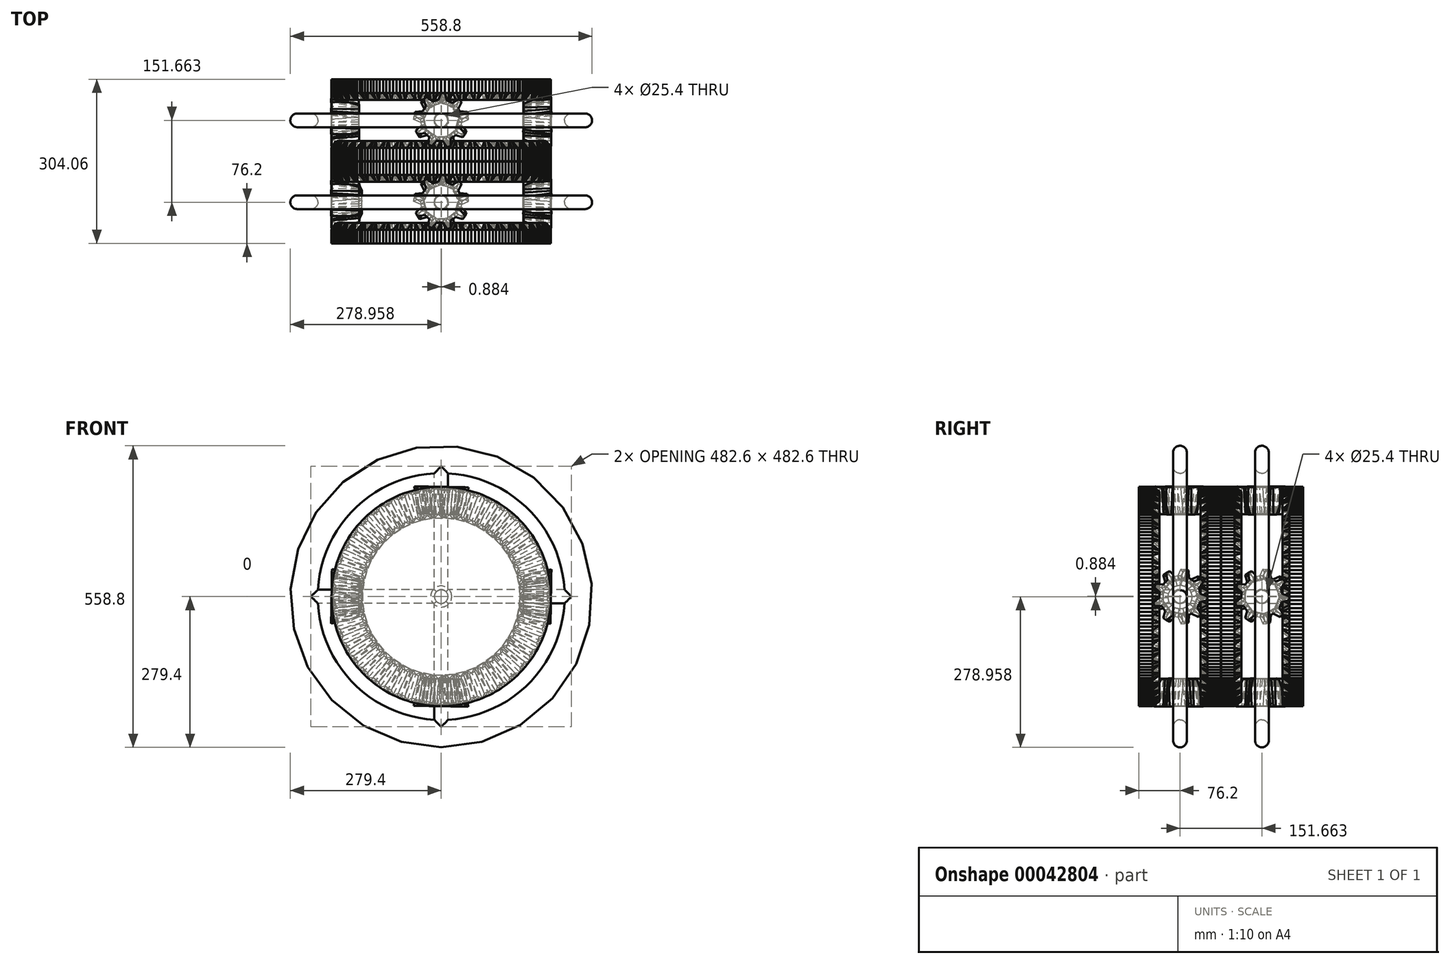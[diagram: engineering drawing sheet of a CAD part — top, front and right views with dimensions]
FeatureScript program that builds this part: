
annotation { "Feature Type Name" : "Feature", "Feature Type Description" : "" }
export const myFeature = defineFeature(function(context is Context, id is Id, definition is map)
    precondition{}
    {
        {
            var Q0;
            Q0=qCreatedBy(makeId("Front.planeOp"),FACE);
            var sketch = newSketch(context, id + "F0", { "sketchPlane" : qUnion([Q0])});
            skLineSegment(sketch, "E0", {"start": v(0, 0) * mm, "end": v(-203.2, 0) * mm, "construction": true});
            skLineSegment(sketch, "E1", {"start": v(-203.2, 0) * mm, "end": v(-152.4, 0) * mm});
            skLineSegment(sketch, "E2.1.0", {"start": v(-203.08, -7.1) * mm, "end": v(-152.3, -5.32) * mm});
            skLineSegment(sketch, "E2.2.0", {"start": v(-202.7, -14.17) * mm, "end": v(-152.03, -10.63) * mm});
            skLineSegment(sketch, "E2.3.0", {"start": v(-202.09, -21.24) * mm, "end": v(-151.57, -15.93) * mm});
            skLineSegment(sketch, "E2.4.0", {"start": v(-201.22, -28.28) * mm, "end": v(-150.92, -21.2) * mm});
            skLineSegment(sketch, "E2.5.0", {"start": v(-200.11, -35.29) * mm, "end": v(-150.08, -26.46) * mm});
            skLineSegment(sketch, "E2.6.0", {"start": v(-198.76, -42.25) * mm, "end": v(-149.07, -31.69) * mm});
            skLineSegment(sketch, "E2.7.0", {"start": v(-197.16, -49.16) * mm, "end": v(-147.87, -36.87) * mm});
            skLineSegment(sketch, "E2.8.0", {"start": v(-195.33, -56) * mm, "end": v(-146.5, -42) * mm});
            skLineSegment(sketch, "E2.9.0", {"start": v(-193.25, -62.8) * mm, "end": v(-144.94, -47.1) * mm});
            skLineSegment(sketch, "E2.10.0", {"start": v(-190.95, -69.5) * mm, "end": v(-143.2, -52.12) * mm});
            skLineSegment(sketch, "E2.11.0", {"start": v(-188.4, -76.12) * mm, "end": v(-141.3, -57.1) * mm});
            skLineSegment(sketch, "E2.12.0", {"start": v(-185.63, -82.65) * mm, "end": v(-139.22, -61.99) * mm});
            skLineSegment(sketch, "E2.13.0", {"start": v(-182.63, -89.08) * mm, "end": v(-136.98, -66.8) * mm});
            skLineSegment(sketch, "E2.14.0", {"start": v(-179.41, -95.4) * mm, "end": v(-134.56, -71.55) * mm});
            skLineSegment(sketch, "E2.15.0", {"start": v(-175.98, -101.6) * mm, "end": v(-131.98, -76.2) * mm});
            skLineSegment(sketch, "E2.16.0", {"start": v(-172.32, -107.68) * mm, "end": v(-129.24, -80.76) * mm});
            skLineSegment(sketch, "E2.17.0", {"start": v(-168.46, -113.63) * mm, "end": v(-126.35, -85.22) * mm});
            skLineSegment(sketch, "E2.18.0", {"start": v(-164.4, -119.44) * mm, "end": v(-123.3, -89.58) * mm});
            skLineSegment(sketch, "E2.19.0", {"start": v(-160.12, -125.1) * mm, "end": v(-120.1, -93.83) * mm});
            skLineSegment(sketch, "E2.20.0", {"start": v(-155.66, -130.61) * mm, "end": v(-116.75, -97.96) * mm});
            skLineSegment(sketch, "E2.21.0", {"start": v(-151, -135.97) * mm, "end": v(-113.26, -101.98) * mm});
            skLineSegment(sketch, "E2.22.0", {"start": v(-146.17, -141.15) * mm, "end": v(-109.63, -105.87) * mm});
            skLineSegment(sketch, "E2.23.0", {"start": v(-141.15, -146.17) * mm, "end": v(-105.87, -109.63) * mm});
            skLineSegment(sketch, "E2.24.0", {"start": v(-135.97, -151) * mm, "end": v(-101.98, -113.26) * mm});
            skLineSegment(sketch, "E2.25.0", {"start": v(-130.61, -155.66) * mm, "end": v(-97.96, -116.75) * mm});
            skLineSegment(sketch, "E2.26.0", {"start": v(-125.1, -160.12) * mm, "end": v(-93.83, -120.1) * mm});
            skLineSegment(sketch, "E2.27.0", {"start": v(-119.44, -164.4) * mm, "end": v(-89.58, -123.3) * mm});
            skLineSegment(sketch, "E2.28.0", {"start": v(-113.63, -168.46) * mm, "end": v(-85.22, -126.35) * mm});
            skLineSegment(sketch, "E2.29.0", {"start": v(-107.68, -172.32) * mm, "end": v(-80.76, -129.24) * mm});
            skLineSegment(sketch, "E2.30.0", {"start": v(-101.6, -175.98) * mm, "end": v(-76.2, -131.98) * mm});
            skLineSegment(sketch, "E2.31.0", {"start": v(-95.4, -179.41) * mm, "end": v(-71.55, -134.56) * mm});
            skLineSegment(sketch, "E2.32.0", {"start": v(-89.08, -182.63) * mm, "end": v(-66.8, -136.98) * mm});
            skLineSegment(sketch, "E2.33.0", {"start": v(-82.65, -185.63) * mm, "end": v(-61.99, -139.22) * mm});
            skLineSegment(sketch, "E2.34.0", {"start": v(-76.12, -188.4) * mm, "end": v(-57.1, -141.3) * mm});
            skLineSegment(sketch, "E2.35.0", {"start": v(-69.5, -190.95) * mm, "end": v(-52.12, -143.2) * mm});
            skLineSegment(sketch, "E2.36.0", {"start": v(-62.8, -193.25) * mm, "end": v(-47.1, -144.94) * mm});
            skLineSegment(sketch, "E2.37.0", {"start": v(-56, -195.33) * mm, "end": v(-42, -146.5) * mm});
            skLineSegment(sketch, "E2.38.0", {"start": v(-49.16, -197.16) * mm, "end": v(-36.87, -147.87) * mm});
            skLineSegment(sketch, "E2.39.0", {"start": v(-42.25, -198.76) * mm, "end": v(-31.69, -149.07) * mm});
            skLineSegment(sketch, "E2.40.0", {"start": v(-35.29, -200.11) * mm, "end": v(-26.46, -150.08) * mm});
            skLineSegment(sketch, "E2.41.0", {"start": v(-28.28, -201.22) * mm, "end": v(-21.2, -150.92) * mm});
            skLineSegment(sketch, "E2.42.0", {"start": v(-21.24, -202.09) * mm, "end": v(-15.93, -151.57) * mm});
            skLineSegment(sketch, "E2.43.0", {"start": v(-14.17, -202.7) * mm, "end": v(-10.63, -152.03) * mm});
            skLineSegment(sketch, "E2.44.0", {"start": v(-7.1, -203.08) * mm, "end": v(-5.32, -152.3) * mm});
            skLineSegment(sketch, "E2.45.0", {"start": v(0, -203.2) * mm, "end": v(0, -152.4) * mm});
            skLineSegment(sketch, "E2.46.0", {"start": v(7.1, -203.08) * mm, "end": v(5.32, -152.3) * mm});
            skLineSegment(sketch, "E2.47.0", {"start": v(14.17, -202.7) * mm, "end": v(10.63, -152.03) * mm});
            skLineSegment(sketch, "E2.48.0", {"start": v(21.24, -202.09) * mm, "end": v(15.93, -151.57) * mm});
            skLineSegment(sketch, "E2.49.0", {"start": v(28.28, -201.22) * mm, "end": v(21.2, -150.92) * mm});
            skLineSegment(sketch, "E2.50.0", {"start": v(35.29, -200.11) * mm, "end": v(26.46, -150.08) * mm});
            skLineSegment(sketch, "E2.51.0", {"start": v(42.25, -198.76) * mm, "end": v(31.69, -149.07) * mm});
            skLineSegment(sketch, "E2.52.0", {"start": v(49.16, -197.16) * mm, "end": v(36.87, -147.87) * mm});
            skLineSegment(sketch, "E2.53.0", {"start": v(56, -195.33) * mm, "end": v(42, -146.5) * mm});
            skLineSegment(sketch, "E2.54.0", {"start": v(62.8, -193.25) * mm, "end": v(47.1, -144.94) * mm});
            skLineSegment(sketch, "E2.55.0", {"start": v(69.5, -190.95) * mm, "end": v(52.12, -143.2) * mm});
            skLineSegment(sketch, "E2.56.0", {"start": v(76.12, -188.4) * mm, "end": v(57.1, -141.3) * mm});
            skLineSegment(sketch, "E2.57.0", {"start": v(82.65, -185.63) * mm, "end": v(61.99, -139.22) * mm});
            skLineSegment(sketch, "E2.58.0", {"start": v(89.08, -182.63) * mm, "end": v(66.8, -136.98) * mm});
            skLineSegment(sketch, "E2.59.0", {"start": v(95.4, -179.41) * mm, "end": v(71.55, -134.56) * mm});
            skLineSegment(sketch, "E2.60.0", {"start": v(101.6, -175.98) * mm, "end": v(76.2, -131.98) * mm});
            skLineSegment(sketch, "E2.61.0", {"start": v(107.68, -172.32) * mm, "end": v(80.76, -129.24) * mm});
            skLineSegment(sketch, "E2.62.0", {"start": v(113.63, -168.46) * mm, "end": v(85.22, -126.35) * mm});
            skLineSegment(sketch, "E2.63.0", {"start": v(119.44, -164.4) * mm, "end": v(89.58, -123.3) * mm});
            skLineSegment(sketch, "E2.64.0", {"start": v(125.1, -160.12) * mm, "end": v(93.83, -120.1) * mm});
            skLineSegment(sketch, "E2.65.0", {"start": v(130.61, -155.66) * mm, "end": v(97.96, -116.75) * mm});
            skLineSegment(sketch, "E2.66.0", {"start": v(135.97, -151) * mm, "end": v(101.98, -113.26) * mm});
            skLineSegment(sketch, "E2.67.0", {"start": v(141.15, -146.17) * mm, "end": v(105.87, -109.63) * mm});
            skLineSegment(sketch, "E2.68.0", {"start": v(146.17, -141.15) * mm, "end": v(109.63, -105.87) * mm});
            skLineSegment(sketch, "E2.69.0", {"start": v(151, -135.97) * mm, "end": v(113.26, -101.98) * mm});
            skLineSegment(sketch, "E2.70.0", {"start": v(155.66, -130.61) * mm, "end": v(116.75, -97.96) * mm});
            skLineSegment(sketch, "E2.71.0", {"start": v(160.12, -125.1) * mm, "end": v(120.1, -93.83) * mm});
            skLineSegment(sketch, "E2.72.0", {"start": v(164.4, -119.44) * mm, "end": v(123.3, -89.58) * mm});
            skLineSegment(sketch, "E2.73.0", {"start": v(168.46, -113.63) * mm, "end": v(126.35, -85.22) * mm});
            skLineSegment(sketch, "E2.74.0", {"start": v(172.32, -107.68) * mm, "end": v(129.24, -80.76) * mm});
            skLineSegment(sketch, "E2.75.0", {"start": v(175.98, -101.6) * mm, "end": v(131.98, -76.2) * mm});
            skLineSegment(sketch, "E2.76.0", {"start": v(179.41, -95.4) * mm, "end": v(134.56, -71.55) * mm});
            skLineSegment(sketch, "E2.77.0", {"start": v(182.63, -89.08) * mm, "end": v(136.98, -66.8) * mm});
            skLineSegment(sketch, "E2.78.0", {"start": v(185.63, -82.65) * mm, "end": v(139.22, -61.99) * mm});
            skLineSegment(sketch, "E2.79.0", {"start": v(188.4, -76.12) * mm, "end": v(141.3, -57.1) * mm});
            skLineSegment(sketch, "E2.80.0", {"start": v(190.95, -69.5) * mm, "end": v(143.2, -52.12) * mm});
            skLineSegment(sketch, "E2.81.0", {"start": v(193.25, -62.8) * mm, "end": v(144.94, -47.1) * mm});
            skLineSegment(sketch, "E2.82.0", {"start": v(195.33, -56) * mm, "end": v(146.5, -42) * mm});
            skLineSegment(sketch, "E2.83.0", {"start": v(197.16, -49.16) * mm, "end": v(147.87, -36.87) * mm});
            skLineSegment(sketch, "E2.84.0", {"start": v(198.76, -42.25) * mm, "end": v(149.07, -31.69) * mm});
            skLineSegment(sketch, "E2.85.0", {"start": v(200.11, -35.29) * mm, "end": v(150.08, -26.46) * mm});
            skLineSegment(sketch, "E2.86.0", {"start": v(201.22, -28.28) * mm, "end": v(150.92, -21.2) * mm});
            skLineSegment(sketch, "E2.87.0", {"start": v(202.09, -21.24) * mm, "end": v(151.57, -15.93) * mm});
            skLineSegment(sketch, "E2.88.0", {"start": v(202.7, -14.17) * mm, "end": v(152.03, -10.63) * mm});
            skLineSegment(sketch, "E2.89.0", {"start": v(203.08, -7.1) * mm, "end": v(152.3, -5.32) * mm});
            skLineSegment(sketch, "E2.90.0", {"start": v(203.2, 0) * mm, "end": v(152.4, 0) * mm});
            skLineSegment(sketch, "E2.91.0", {"start": v(203.08, 7.1) * mm, "end": v(152.3, 5.32) * mm});
            skLineSegment(sketch, "E2.92.0", {"start": v(202.7, 14.17) * mm, "end": v(152.03, 10.63) * mm});
            skLineSegment(sketch, "E2.93.0", {"start": v(202.09, 21.24) * mm, "end": v(151.57, 15.93) * mm});
            skLineSegment(sketch, "E2.94.0", {"start": v(201.22, 28.28) * mm, "end": v(150.92, 21.2) * mm});
            skLineSegment(sketch, "E2.95.0", {"start": v(200.11, 35.29) * mm, "end": v(150.08, 26.46) * mm});
            skLineSegment(sketch, "E2.96.0", {"start": v(198.76, 42.25) * mm, "end": v(149.07, 31.69) * mm});
            skLineSegment(sketch, "E2.97.0", {"start": v(197.16, 49.16) * mm, "end": v(147.87, 36.87) * mm});
            skLineSegment(sketch, "E2.98.0", {"start": v(195.33, 56) * mm, "end": v(146.5, 42) * mm});
            skLineSegment(sketch, "E2.99.0", {"start": v(193.25, 62.8) * mm, "end": v(144.94, 47.1) * mm});
            skLineSegment(sketch, "E2.100.0", {"start": v(190.95, 69.5) * mm, "end": v(143.2, 52.12) * mm});
            skLineSegment(sketch, "E2.101.0", {"start": v(188.4, 76.12) * mm, "end": v(141.3, 57.1) * mm});
            skLineSegment(sketch, "E2.102.0", {"start": v(185.63, 82.65) * mm, "end": v(139.22, 61.99) * mm});
            skLineSegment(sketch, "E2.103.0", {"start": v(182.63, 89.08) * mm, "end": v(136.98, 66.8) * mm});
            skLineSegment(sketch, "E2.104.0", {"start": v(179.41, 95.4) * mm, "end": v(134.56, 71.55) * mm});
            skLineSegment(sketch, "E2.105.0", {"start": v(175.98, 101.6) * mm, "end": v(131.98, 76.2) * mm});
            skLineSegment(sketch, "E2.106.0", {"start": v(172.32, 107.68) * mm, "end": v(129.24, 80.76) * mm});
            skLineSegment(sketch, "E2.107.0", {"start": v(168.46, 113.63) * mm, "end": v(126.35, 85.22) * mm});
            skLineSegment(sketch, "E2.108.0", {"start": v(164.4, 119.44) * mm, "end": v(123.3, 89.58) * mm});
            skLineSegment(sketch, "E2.109.0", {"start": v(160.12, 125.1) * mm, "end": v(120.1, 93.83) * mm});
            skLineSegment(sketch, "E2.110.0", {"start": v(155.66, 130.61) * mm, "end": v(116.75, 97.96) * mm});
            skLineSegment(sketch, "E2.111.0", {"start": v(151, 135.97) * mm, "end": v(113.26, 101.98) * mm});
            skLineSegment(sketch, "E2.112.0", {"start": v(146.17, 141.15) * mm, "end": v(109.63, 105.87) * mm});
            skLineSegment(sketch, "E2.113.0", {"start": v(141.15, 146.17) * mm, "end": v(105.87, 109.63) * mm});
            skLineSegment(sketch, "E2.114.0", {"start": v(135.97, 151) * mm, "end": v(101.98, 113.26) * mm});
            skLineSegment(sketch, "E2.115.0", {"start": v(130.61, 155.66) * mm, "end": v(97.96, 116.75) * mm});
            skLineSegment(sketch, "E2.116.0", {"start": v(125.1, 160.12) * mm, "end": v(93.83, 120.1) * mm});
            skLineSegment(sketch, "E2.117.0", {"start": v(119.44, 164.4) * mm, "end": v(89.58, 123.3) * mm});
            skLineSegment(sketch, "E2.118.0", {"start": v(113.63, 168.46) * mm, "end": v(85.22, 126.35) * mm});
            skLineSegment(sketch, "E2.119.0", {"start": v(107.68, 172.32) * mm, "end": v(80.76, 129.24) * mm});
            skLineSegment(sketch, "E2.120.0", {"start": v(101.6, 175.98) * mm, "end": v(76.2, 131.98) * mm});
            skLineSegment(sketch, "E2.121.0", {"start": v(95.4, 179.41) * mm, "end": v(71.55, 134.56) * mm});
            skLineSegment(sketch, "E2.122.0", {"start": v(89.08, 182.63) * mm, "end": v(66.8, 136.98) * mm});
            skLineSegment(sketch, "E2.123.0", {"start": v(82.65, 185.63) * mm, "end": v(61.99, 139.22) * mm});
            skLineSegment(sketch, "E2.124.0", {"start": v(76.12, 188.4) * mm, "end": v(57.1, 141.3) * mm});
            skLineSegment(sketch, "E2.125.0", {"start": v(69.5, 190.95) * mm, "end": v(52.12, 143.2) * mm});
            skLineSegment(sketch, "E2.126.0", {"start": v(62.8, 193.25) * mm, "end": v(47.1, 144.94) * mm});
            skLineSegment(sketch, "E2.127.0", {"start": v(56, 195.33) * mm, "end": v(42, 146.5) * mm});
            skLineSegment(sketch, "E2.128.0", {"start": v(49.16, 197.16) * mm, "end": v(36.87, 147.87) * mm});
            skLineSegment(sketch, "E2.129.0", {"start": v(42.25, 198.76) * mm, "end": v(31.69, 149.07) * mm});
            skLineSegment(sketch, "E2.130.0", {"start": v(35.29, 200.11) * mm, "end": v(26.46, 150.08) * mm});
            skLineSegment(sketch, "E2.131.0", {"start": v(28.28, 201.22) * mm, "end": v(21.2, 150.92) * mm});
            skLineSegment(sketch, "E2.132.0", {"start": v(21.24, 202.09) * mm, "end": v(15.93, 151.57) * mm});
            skLineSegment(sketch, "E2.133.0", {"start": v(14.17, 202.7) * mm, "end": v(10.63, 152.03) * mm});
            skLineSegment(sketch, "E2.134.0", {"start": v(7.1, 203.08) * mm, "end": v(5.32, 152.3) * mm});
            skLineSegment(sketch, "E2.135.0", {"start": v(0, 203.2) * mm, "end": v(0, 152.4) * mm});
            skLineSegment(sketch, "E2.136.0", {"start": v(-7.1, 203.08) * mm, "end": v(-5.32, 152.3) * mm});
            skLineSegment(sketch, "E2.137.0", {"start": v(-14.17, 202.7) * mm, "end": v(-10.63, 152.03) * mm});
            skLineSegment(sketch, "E2.138.0", {"start": v(-21.24, 202.09) * mm, "end": v(-15.93, 151.57) * mm});
            skLineSegment(sketch, "E2.139.0", {"start": v(-28.28, 201.22) * mm, "end": v(-21.2, 150.92) * mm});
            skLineSegment(sketch, "E2.140.0", {"start": v(-35.29, 200.11) * mm, "end": v(-26.46, 150.08) * mm});
            skLineSegment(sketch, "E2.141.0", {"start": v(-42.25, 198.76) * mm, "end": v(-31.69, 149.07) * mm});
            skLineSegment(sketch, "E2.142.0", {"start": v(-49.16, 197.16) * mm, "end": v(-36.87, 147.87) * mm});
            skLineSegment(sketch, "E2.143.0", {"start": v(-56, 195.33) * mm, "end": v(-42, 146.5) * mm});
            skLineSegment(sketch, "E2.144.0", {"start": v(-62.8, 193.25) * mm, "end": v(-47.1, 144.94) * mm});
            skLineSegment(sketch, "E2.145.0", {"start": v(-69.5, 190.95) * mm, "end": v(-52.12, 143.2) * mm});
            skLineSegment(sketch, "E2.146.0", {"start": v(-76.12, 188.4) * mm, "end": v(-57.1, 141.3) * mm});
            skLineSegment(sketch, "E2.147.0", {"start": v(-82.65, 185.63) * mm, "end": v(-61.99, 139.22) * mm});
            skLineSegment(sketch, "E2.148.0", {"start": v(-89.08, 182.63) * mm, "end": v(-66.8, 136.98) * mm});
            skLineSegment(sketch, "E2.149.0", {"start": v(-95.4, 179.41) * mm, "end": v(-71.55, 134.56) * mm});
            skLineSegment(sketch, "E2.150.0", {"start": v(-101.6, 175.98) * mm, "end": v(-76.2, 131.98) * mm});
            skLineSegment(sketch, "E2.151.0", {"start": v(-107.68, 172.32) * mm, "end": v(-80.76, 129.24) * mm});
            skLineSegment(sketch, "E2.152.0", {"start": v(-113.63, 168.46) * mm, "end": v(-85.22, 126.35) * mm});
            skLineSegment(sketch, "E2.153.0", {"start": v(-119.44, 164.4) * mm, "end": v(-89.58, 123.3) * mm});
            skLineSegment(sketch, "E2.154.0", {"start": v(-125.1, 160.12) * mm, "end": v(-93.83, 120.1) * mm});
            skLineSegment(sketch, "E2.155.0", {"start": v(-130.61, 155.66) * mm, "end": v(-97.96, 116.75) * mm});
            skLineSegment(sketch, "E2.156.0", {"start": v(-135.97, 151) * mm, "end": v(-101.98, 113.26) * mm});
            skLineSegment(sketch, "E2.157.0", {"start": v(-141.15, 146.17) * mm, "end": v(-105.87, 109.63) * mm});
            skLineSegment(sketch, "E2.158.0", {"start": v(-146.17, 141.15) * mm, "end": v(-109.63, 105.87) * mm});
            skLineSegment(sketch, "E2.159.0", {"start": v(-151, 135.97) * mm, "end": v(-113.26, 101.98) * mm});
            skLineSegment(sketch, "E2.160.0", {"start": v(-155.66, 130.61) * mm, "end": v(-116.75, 97.96) * mm});
            skLineSegment(sketch, "E2.161.0", {"start": v(-160.12, 125.1) * mm, "end": v(-120.1, 93.83) * mm});
            skLineSegment(sketch, "E2.162.0", {"start": v(-164.4, 119.44) * mm, "end": v(-123.3, 89.58) * mm});
            skLineSegment(sketch, "E2.163.0", {"start": v(-168.46, 113.63) * mm, "end": v(-126.35, 85.22) * mm});
            skLineSegment(sketch, "E2.164.0", {"start": v(-172.32, 107.68) * mm, "end": v(-129.24, 80.76) * mm});
            skLineSegment(sketch, "E2.165.0", {"start": v(-175.98, 101.6) * mm, "end": v(-131.98, 76.2) * mm});
            skLineSegment(sketch, "E2.166.0", {"start": v(-179.41, 95.4) * mm, "end": v(-134.56, 71.55) * mm});
            skLineSegment(sketch, "E2.167.0", {"start": v(-182.63, 89.08) * mm, "end": v(-136.98, 66.8) * mm});
            skLineSegment(sketch, "E2.168.0", {"start": v(-185.63, 82.65) * mm, "end": v(-139.22, 61.99) * mm});
            skLineSegment(sketch, "E2.169.0", {"start": v(-188.4, 76.12) * mm, "end": v(-141.3, 57.1) * mm});
            skLineSegment(sketch, "E2.170.0", {"start": v(-190.95, 69.5) * mm, "end": v(-143.2, 52.12) * mm});
            skLineSegment(sketch, "E2.171.0", {"start": v(-193.25, 62.8) * mm, "end": v(-144.94, 47.1) * mm});
            skLineSegment(sketch, "E2.172.0", {"start": v(-195.33, 56) * mm, "end": v(-146.5, 42) * mm});
            skLineSegment(sketch, "E2.173.0", {"start": v(-197.16, 49.16) * mm, "end": v(-147.87, 36.87) * mm});
            skLineSegment(sketch, "E2.174.0", {"start": v(-198.76, 42.25) * mm, "end": v(-149.07, 31.69) * mm});
            skLineSegment(sketch, "E2.175.0", {"start": v(-200.11, 35.29) * mm, "end": v(-150.08, 26.46) * mm});
            skLineSegment(sketch, "E2.176.0", {"start": v(-201.22, 28.28) * mm, "end": v(-150.92, 21.2) * mm});
            skLineSegment(sketch, "E2.177.0", {"start": v(-202.09, 21.24) * mm, "end": v(-151.57, 15.93) * mm});
            skLineSegment(sketch, "E2.178.0", {"start": v(-202.7, 14.17) * mm, "end": v(-152.03, 10.63) * mm});
            skLineSegment(sketch, "E2.179.0", {"start": v(-203.08, 7.1) * mm, "end": v(-152.3, 5.32) * mm});
            skPoint(sketch, "E2.center", {"position": v(0, 0) * mm});
            skLineSegment(sketch, "E3", {"start": v(-203.2, 0) * mm, "end": v(-203.08, 7.1) * mm});
            skLineSegment(sketch, "E4.1.0", {"start": v(-203.08, -7.1) * mm, "end": v(-203.2, 0) * mm});
            skLineSegment(sketch, "E4.2.0", {"start": v(-202.7, -14.17) * mm, "end": v(-203.08, -7.1) * mm});
            skLineSegment(sketch, "E4.3.0", {"start": v(-202.09, -21.24) * mm, "end": v(-202.7, -14.17) * mm});
            skLineSegment(sketch, "E4.4.0", {"start": v(-201.22, -28.28) * mm, "end": v(-202.09, -21.24) * mm});
            skLineSegment(sketch, "E4.5.0", {"start": v(-200.11, -35.29) * mm, "end": v(-201.22, -28.28) * mm});
            skLineSegment(sketch, "E4.6.0", {"start": v(-198.76, -42.25) * mm, "end": v(-200.11, -35.29) * mm});
            skLineSegment(sketch, "E4.7.0", {"start": v(-197.16, -49.16) * mm, "end": v(-198.76, -42.25) * mm});
            skLineSegment(sketch, "E4.8.0", {"start": v(-195.33, -56) * mm, "end": v(-197.16, -49.16) * mm});
            skLineSegment(sketch, "E4.9.0", {"start": v(-193.25, -62.8) * mm, "end": v(-195.33, -56) * mm});
            skLineSegment(sketch, "E4.10.0", {"start": v(-190.95, -69.5) * mm, "end": v(-193.25, -62.8) * mm});
            skLineSegment(sketch, "E4.11.0", {"start": v(-188.4, -76.12) * mm, "end": v(-190.95, -69.5) * mm});
            skLineSegment(sketch, "E4.12.0", {"start": v(-185.63, -82.65) * mm, "end": v(-188.4, -76.12) * mm});
            skLineSegment(sketch, "E4.13.0", {"start": v(-182.63, -89.08) * mm, "end": v(-185.63, -82.65) * mm});
            skLineSegment(sketch, "E4.14.0", {"start": v(-179.41, -95.4) * mm, "end": v(-182.63, -89.08) * mm});
            skLineSegment(sketch, "E4.15.0", {"start": v(-175.98, -101.6) * mm, "end": v(-179.41, -95.4) * mm});
            skLineSegment(sketch, "E4.16.0", {"start": v(-172.32, -107.68) * mm, "end": v(-175.98, -101.6) * mm});
            skLineSegment(sketch, "E4.17.0", {"start": v(-168.46, -113.63) * mm, "end": v(-172.32, -107.68) * mm});
            skLineSegment(sketch, "E4.18.0", {"start": v(-164.4, -119.44) * mm, "end": v(-168.46, -113.63) * mm});
            skLineSegment(sketch, "E4.19.0", {"start": v(-160.12, -125.1) * mm, "end": v(-164.4, -119.44) * mm});
            skLineSegment(sketch, "E4.20.0", {"start": v(-155.66, -130.61) * mm, "end": v(-160.12, -125.1) * mm});
            skLineSegment(sketch, "E4.21.0", {"start": v(-151, -135.97) * mm, "end": v(-155.66, -130.61) * mm});
            skLineSegment(sketch, "E4.22.0", {"start": v(-146.17, -141.15) * mm, "end": v(-151, -135.97) * mm});
            skLineSegment(sketch, "E4.23.0", {"start": v(-141.15, -146.17) * mm, "end": v(-146.17, -141.15) * mm});
            skLineSegment(sketch, "E4.24.0", {"start": v(-135.97, -151) * mm, "end": v(-141.15, -146.17) * mm});
            skLineSegment(sketch, "E4.25.0", {"start": v(-130.61, -155.66) * mm, "end": v(-135.97, -151) * mm});
            skLineSegment(sketch, "E4.26.0", {"start": v(-125.1, -160.12) * mm, "end": v(-130.61, -155.66) * mm});
            skLineSegment(sketch, "E4.27.0", {"start": v(-119.44, -164.4) * mm, "end": v(-125.1, -160.12) * mm});
            skLineSegment(sketch, "E4.28.0", {"start": v(-113.63, -168.46) * mm, "end": v(-119.44, -164.4) * mm});
            skLineSegment(sketch, "E4.29.0", {"start": v(-107.68, -172.32) * mm, "end": v(-113.63, -168.46) * mm});
            skLineSegment(sketch, "E4.30.0", {"start": v(-101.6, -175.98) * mm, "end": v(-107.68, -172.32) * mm});
            skLineSegment(sketch, "E4.31.0", {"start": v(-95.4, -179.41) * mm, "end": v(-101.6, -175.98) * mm});
            skLineSegment(sketch, "E4.32.0", {"start": v(-89.08, -182.63) * mm, "end": v(-95.4, -179.41) * mm});
            skLineSegment(sketch, "E4.33.0", {"start": v(-82.65, -185.63) * mm, "end": v(-89.08, -182.63) * mm});
            skLineSegment(sketch, "E4.34.0", {"start": v(-76.12, -188.4) * mm, "end": v(-82.65, -185.63) * mm});
            skLineSegment(sketch, "E4.35.0", {"start": v(-69.5, -190.95) * mm, "end": v(-76.12, -188.4) * mm});
            skLineSegment(sketch, "E4.36.0", {"start": v(-62.8, -193.25) * mm, "end": v(-69.5, -190.95) * mm});
            skLineSegment(sketch, "E4.37.0", {"start": v(-56, -195.33) * mm, "end": v(-62.8, -193.25) * mm});
            skLineSegment(sketch, "E4.38.0", {"start": v(-49.16, -197.16) * mm, "end": v(-56, -195.33) * mm});
            skLineSegment(sketch, "E4.39.0", {"start": v(-42.25, -198.76) * mm, "end": v(-49.16, -197.16) * mm});
            skLineSegment(sketch, "E4.40.0", {"start": v(-35.29, -200.11) * mm, "end": v(-42.25, -198.76) * mm});
            skLineSegment(sketch, "E4.41.0", {"start": v(-28.28, -201.22) * mm, "end": v(-35.29, -200.11) * mm});
            skLineSegment(sketch, "E4.42.0", {"start": v(-21.24, -202.09) * mm, "end": v(-28.28, -201.22) * mm});
            skLineSegment(sketch, "E4.43.0", {"start": v(-14.17, -202.7) * mm, "end": v(-21.24, -202.09) * mm});
            skLineSegment(sketch, "E4.44.0", {"start": v(-7.1, -203.08) * mm, "end": v(-14.17, -202.7) * mm});
            skLineSegment(sketch, "E4.45.0", {"start": v(0, -203.2) * mm, "end": v(-7.1, -203.08) * mm});
            skLineSegment(sketch, "E4.46.0", {"start": v(7.1, -203.08) * mm, "end": v(0, -203.2) * mm});
            skLineSegment(sketch, "E4.47.0", {"start": v(14.17, -202.7) * mm, "end": v(7.1, -203.08) * mm});
            skLineSegment(sketch, "E4.48.0", {"start": v(21.24, -202.09) * mm, "end": v(14.17, -202.7) * mm});
            skLineSegment(sketch, "E4.49.0", {"start": v(28.28, -201.22) * mm, "end": v(21.24, -202.09) * mm});
            skLineSegment(sketch, "E4.50.0", {"start": v(35.29, -200.11) * mm, "end": v(28.28, -201.22) * mm});
            skLineSegment(sketch, "E4.51.0", {"start": v(42.25, -198.76) * mm, "end": v(35.29, -200.11) * mm});
            skLineSegment(sketch, "E4.52.0", {"start": v(49.16, -197.16) * mm, "end": v(42.25, -198.76) * mm});
            skLineSegment(sketch, "E4.53.0", {"start": v(56, -195.33) * mm, "end": v(49.16, -197.16) * mm});
            skLineSegment(sketch, "E4.54.0", {"start": v(62.8, -193.25) * mm, "end": v(56, -195.33) * mm});
            skLineSegment(sketch, "E4.55.0", {"start": v(69.5, -190.95) * mm, "end": v(62.8, -193.25) * mm});
            skLineSegment(sketch, "E4.56.0", {"start": v(76.12, -188.4) * mm, "end": v(69.5, -190.95) * mm});
            skLineSegment(sketch, "E4.57.0", {"start": v(82.65, -185.63) * mm, "end": v(76.12, -188.4) * mm});
            skLineSegment(sketch, "E4.58.0", {"start": v(89.08, -182.63) * mm, "end": v(82.65, -185.63) * mm});
            skLineSegment(sketch, "E4.59.0", {"start": v(95.4, -179.41) * mm, "end": v(89.08, -182.63) * mm});
            skLineSegment(sketch, "E4.60.0", {"start": v(101.6, -175.98) * mm, "end": v(95.4, -179.41) * mm});
            skLineSegment(sketch, "E4.61.0", {"start": v(107.68, -172.32) * mm, "end": v(101.6, -175.98) * mm});
            skLineSegment(sketch, "E4.62.0", {"start": v(113.63, -168.46) * mm, "end": v(107.68, -172.32) * mm});
            skLineSegment(sketch, "E4.63.0", {"start": v(119.44, -164.4) * mm, "end": v(113.63, -168.46) * mm});
            skLineSegment(sketch, "E4.64.0", {"start": v(125.1, -160.12) * mm, "end": v(119.44, -164.4) * mm});
            skLineSegment(sketch, "E4.65.0", {"start": v(130.61, -155.66) * mm, "end": v(125.1, -160.12) * mm});
            skLineSegment(sketch, "E4.66.0", {"start": v(135.97, -151) * mm, "end": v(130.61, -155.66) * mm});
            skLineSegment(sketch, "E4.67.0", {"start": v(141.15, -146.17) * mm, "end": v(135.97, -151) * mm});
            skLineSegment(sketch, "E4.68.0", {"start": v(146.17, -141.15) * mm, "end": v(141.15, -146.17) * mm});
            skLineSegment(sketch, "E4.69.0", {"start": v(151, -135.97) * mm, "end": v(146.17, -141.15) * mm});
            skLineSegment(sketch, "E4.70.0", {"start": v(155.66, -130.61) * mm, "end": v(151, -135.97) * mm});
            skLineSegment(sketch, "E4.71.0", {"start": v(160.12, -125.1) * mm, "end": v(155.66, -130.61) * mm});
            skLineSegment(sketch, "E4.72.0", {"start": v(164.4, -119.44) * mm, "end": v(160.12, -125.1) * mm});
            skLineSegment(sketch, "E4.73.0", {"start": v(168.46, -113.63) * mm, "end": v(164.4, -119.44) * mm});
            skLineSegment(sketch, "E4.74.0", {"start": v(172.32, -107.68) * mm, "end": v(168.46, -113.63) * mm});
            skLineSegment(sketch, "E4.75.0", {"start": v(175.98, -101.6) * mm, "end": v(172.32, -107.68) * mm});
            skLineSegment(sketch, "E4.76.0", {"start": v(179.41, -95.4) * mm, "end": v(175.98, -101.6) * mm});
            skLineSegment(sketch, "E4.77.0", {"start": v(182.63, -89.08) * mm, "end": v(179.41, -95.4) * mm});
            skLineSegment(sketch, "E4.78.0", {"start": v(185.63, -82.65) * mm, "end": v(182.63, -89.08) * mm});
            skLineSegment(sketch, "E4.79.0", {"start": v(188.4, -76.12) * mm, "end": v(185.63, -82.65) * mm});
            skLineSegment(sketch, "E4.80.0", {"start": v(190.95, -69.5) * mm, "end": v(188.4, -76.12) * mm});
            skLineSegment(sketch, "E4.81.0", {"start": v(193.25, -62.8) * mm, "end": v(190.95, -69.5) * mm});
            skLineSegment(sketch, "E4.82.0", {"start": v(195.33, -56) * mm, "end": v(193.25, -62.8) * mm});
            skLineSegment(sketch, "E4.83.0", {"start": v(197.16, -49.16) * mm, "end": v(195.33, -56) * mm});
            skLineSegment(sketch, "E4.84.0", {"start": v(198.76, -42.25) * mm, "end": v(197.16, -49.16) * mm});
            skLineSegment(sketch, "E4.85.0", {"start": v(200.11, -35.29) * mm, "end": v(198.76, -42.25) * mm});
            skLineSegment(sketch, "E4.86.0", {"start": v(201.22, -28.28) * mm, "end": v(200.11, -35.29) * mm});
            skLineSegment(sketch, "E4.87.0", {"start": v(202.09, -21.24) * mm, "end": v(201.22, -28.28) * mm});
            skLineSegment(sketch, "E4.88.0", {"start": v(202.7, -14.17) * mm, "end": v(202.09, -21.24) * mm});
            skLineSegment(sketch, "E4.89.0", {"start": v(203.08, -7.1) * mm, "end": v(202.7, -14.17) * mm});
            skLineSegment(sketch, "E4.90.0", {"start": v(203.2, 0) * mm, "end": v(203.08, -7.1) * mm});
            skLineSegment(sketch, "E4.91.0", {"start": v(203.08, 7.1) * mm, "end": v(203.2, 0) * mm});
            skLineSegment(sketch, "E4.92.0", {"start": v(202.7, 14.17) * mm, "end": v(203.08, 7.1) * mm});
            skLineSegment(sketch, "E4.93.0", {"start": v(202.09, 21.24) * mm, "end": v(202.7, 14.17) * mm});
            skLineSegment(sketch, "E4.94.0", {"start": v(201.22, 28.28) * mm, "end": v(202.09, 21.24) * mm});
            skLineSegment(sketch, "E4.95.0", {"start": v(200.11, 35.29) * mm, "end": v(201.22, 28.28) * mm});
            skLineSegment(sketch, "E4.96.0", {"start": v(198.76, 42.25) * mm, "end": v(200.11, 35.29) * mm});
            skLineSegment(sketch, "E4.97.0", {"start": v(197.16, 49.16) * mm, "end": v(198.76, 42.25) * mm});
            skLineSegment(sketch, "E4.98.0", {"start": v(195.33, 56) * mm, "end": v(197.16, 49.16) * mm});
            skLineSegment(sketch, "E4.99.0", {"start": v(193.25, 62.8) * mm, "end": v(195.33, 56) * mm});
            skLineSegment(sketch, "E4.100.0", {"start": v(190.95, 69.5) * mm, "end": v(193.25, 62.8) * mm});
            skLineSegment(sketch, "E4.101.0", {"start": v(188.4, 76.12) * mm, "end": v(190.95, 69.5) * mm});
            skLineSegment(sketch, "E4.102.0", {"start": v(185.63, 82.65) * mm, "end": v(188.4, 76.12) * mm});
            skLineSegment(sketch, "E4.103.0", {"start": v(182.63, 89.08) * mm, "end": v(185.63, 82.65) * mm});
            skLineSegment(sketch, "E4.104.0", {"start": v(179.41, 95.4) * mm, "end": v(182.63, 89.08) * mm});
            skLineSegment(sketch, "E4.105.0", {"start": v(175.98, 101.6) * mm, "end": v(179.41, 95.4) * mm});
            skLineSegment(sketch, "E4.106.0", {"start": v(172.32, 107.68) * mm, "end": v(175.98, 101.6) * mm});
            skLineSegment(sketch, "E4.107.0", {"start": v(168.46, 113.63) * mm, "end": v(172.32, 107.68) * mm});
            skLineSegment(sketch, "E4.108.0", {"start": v(164.4, 119.44) * mm, "end": v(168.46, 113.63) * mm});
            skLineSegment(sketch, "E4.109.0", {"start": v(160.12, 125.1) * mm, "end": v(164.4, 119.44) * mm});
            skLineSegment(sketch, "E4.110.0", {"start": v(155.66, 130.61) * mm, "end": v(160.12, 125.1) * mm});
            skLineSegment(sketch, "E4.111.0", {"start": v(151, 135.97) * mm, "end": v(155.66, 130.61) * mm});
            skLineSegment(sketch, "E4.112.0", {"start": v(146.17, 141.15) * mm, "end": v(151, 135.97) * mm});
            skLineSegment(sketch, "E4.113.0", {"start": v(141.15, 146.17) * mm, "end": v(146.17, 141.15) * mm});
            skLineSegment(sketch, "E4.114.0", {"start": v(135.97, 151) * mm, "end": v(141.15, 146.17) * mm});
            skLineSegment(sketch, "E4.115.0", {"start": v(130.61, 155.66) * mm, "end": v(135.97, 151) * mm});
            skLineSegment(sketch, "E4.116.0", {"start": v(125.1, 160.12) * mm, "end": v(130.61, 155.66) * mm});
            skLineSegment(sketch, "E4.117.0", {"start": v(119.44, 164.4) * mm, "end": v(125.1, 160.12) * mm});
            skLineSegment(sketch, "E4.118.0", {"start": v(113.63, 168.46) * mm, "end": v(119.44, 164.4) * mm});
            skLineSegment(sketch, "E4.119.0", {"start": v(107.68, 172.32) * mm, "end": v(113.63, 168.46) * mm});
            skLineSegment(sketch, "E4.120.0", {"start": v(101.6, 175.98) * mm, "end": v(107.68, 172.32) * mm});
            skLineSegment(sketch, "E4.121.0", {"start": v(95.4, 179.41) * mm, "end": v(101.6, 175.98) * mm});
            skLineSegment(sketch, "E4.122.0", {"start": v(89.08, 182.63) * mm, "end": v(95.4, 179.41) * mm});
            skLineSegment(sketch, "E4.123.0", {"start": v(82.65, 185.63) * mm, "end": v(89.08, 182.63) * mm});
            skLineSegment(sketch, "E4.124.0", {"start": v(76.12, 188.4) * mm, "end": v(82.65, 185.63) * mm});
            skLineSegment(sketch, "E4.125.0", {"start": v(69.5, 190.95) * mm, "end": v(76.12, 188.4) * mm});
            skLineSegment(sketch, "E4.126.0", {"start": v(62.8, 193.25) * mm, "end": v(69.5, 190.95) * mm});
            skLineSegment(sketch, "E4.127.0", {"start": v(56, 195.33) * mm, "end": v(62.8, 193.25) * mm});
            skLineSegment(sketch, "E4.128.0", {"start": v(49.16, 197.16) * mm, "end": v(56, 195.33) * mm});
            skLineSegment(sketch, "E4.129.0", {"start": v(42.25, 198.76) * mm, "end": v(49.16, 197.16) * mm});
            skLineSegment(sketch, "E4.130.0", {"start": v(35.29, 200.11) * mm, "end": v(42.25, 198.76) * mm});
            skLineSegment(sketch, "E4.131.0", {"start": v(28.28, 201.22) * mm, "end": v(35.29, 200.11) * mm});
            skLineSegment(sketch, "E4.132.0", {"start": v(21.24, 202.09) * mm, "end": v(28.28, 201.22) * mm});
            skLineSegment(sketch, "E4.133.0", {"start": v(14.17, 202.7) * mm, "end": v(21.24, 202.09) * mm});
            skLineSegment(sketch, "E4.134.0", {"start": v(7.1, 203.08) * mm, "end": v(14.17, 202.7) * mm});
            skLineSegment(sketch, "E4.135.0", {"start": v(0, 203.2) * mm, "end": v(7.1, 203.08) * mm});
            skLineSegment(sketch, "E4.136.0", {"start": v(-7.1, 203.08) * mm, "end": v(0, 203.2) * mm});
            skLineSegment(sketch, "E4.137.0", {"start": v(-14.17, 202.7) * mm, "end": v(-7.1, 203.08) * mm});
            skLineSegment(sketch, "E4.138.0", {"start": v(-21.24, 202.09) * mm, "end": v(-14.17, 202.7) * mm});
            skLineSegment(sketch, "E4.139.0", {"start": v(-28.28, 201.22) * mm, "end": v(-21.24, 202.09) * mm});
            skLineSegment(sketch, "E4.140.0", {"start": v(-35.29, 200.11) * mm, "end": v(-28.28, 201.22) * mm});
            skLineSegment(sketch, "E4.141.0", {"start": v(-42.25, 198.76) * mm, "end": v(-35.29, 200.11) * mm});
            skLineSegment(sketch, "E4.142.0", {"start": v(-49.16, 197.16) * mm, "end": v(-42.25, 198.76) * mm});
            skLineSegment(sketch, "E4.143.0", {"start": v(-56, 195.33) * mm, "end": v(-49.16, 197.16) * mm});
            skLineSegment(sketch, "E4.144.0", {"start": v(-62.8, 193.25) * mm, "end": v(-56, 195.33) * mm});
            skLineSegment(sketch, "E4.145.0", {"start": v(-69.5, 190.95) * mm, "end": v(-62.8, 193.25) * mm});
            skLineSegment(sketch, "E4.146.0", {"start": v(-76.12, 188.4) * mm, "end": v(-69.5, 190.95) * mm});
            skLineSegment(sketch, "E4.147.0", {"start": v(-82.65, 185.63) * mm, "end": v(-76.12, 188.4) * mm});
            skLineSegment(sketch, "E4.148.0", {"start": v(-89.08, 182.63) * mm, "end": v(-82.65, 185.63) * mm});
            skLineSegment(sketch, "E4.149.0", {"start": v(-95.4, 179.41) * mm, "end": v(-89.08, 182.63) * mm});
            skLineSegment(sketch, "E4.150.0", {"start": v(-101.6, 175.98) * mm, "end": v(-95.4, 179.41) * mm});
            skLineSegment(sketch, "E4.151.0", {"start": v(-107.68, 172.32) * mm, "end": v(-101.6, 175.98) * mm});
            skLineSegment(sketch, "E4.152.0", {"start": v(-113.63, 168.46) * mm, "end": v(-107.68, 172.32) * mm});
            skLineSegment(sketch, "E4.153.0", {"start": v(-119.44, 164.4) * mm, "end": v(-113.63, 168.46) * mm});
            skLineSegment(sketch, "E4.154.0", {"start": v(-125.1, 160.12) * mm, "end": v(-119.44, 164.4) * mm});
            skLineSegment(sketch, "E4.155.0", {"start": v(-130.61, 155.66) * mm, "end": v(-125.1, 160.12) * mm});
            skLineSegment(sketch, "E4.156.0", {"start": v(-135.97, 151) * mm, "end": v(-130.61, 155.66) * mm});
            skLineSegment(sketch, "E4.157.0", {"start": v(-141.15, 146.17) * mm, "end": v(-135.97, 151) * mm});
            skLineSegment(sketch, "E4.158.0", {"start": v(-146.17, 141.15) * mm, "end": v(-141.15, 146.17) * mm});
            skLineSegment(sketch, "E4.159.0", {"start": v(-151, 135.97) * mm, "end": v(-146.17, 141.15) * mm});
            skLineSegment(sketch, "E4.160.0", {"start": v(-155.66, 130.61) * mm, "end": v(-151, 135.97) * mm});
            skLineSegment(sketch, "E4.161.0", {"start": v(-160.12, 125.1) * mm, "end": v(-155.66, 130.61) * mm});
            skLineSegment(sketch, "E4.162.0", {"start": v(-164.4, 119.44) * mm, "end": v(-160.12, 125.1) * mm});
            skLineSegment(sketch, "E4.163.0", {"start": v(-168.46, 113.63) * mm, "end": v(-164.4, 119.44) * mm});
            skLineSegment(sketch, "E4.164.0", {"start": v(-172.32, 107.68) * mm, "end": v(-168.46, 113.63) * mm});
            skLineSegment(sketch, "E4.165.0", {"start": v(-175.98, 101.6) * mm, "end": v(-172.32, 107.68) * mm});
            skLineSegment(sketch, "E4.166.0", {"start": v(-179.41, 95.4) * mm, "end": v(-175.98, 101.6) * mm});
            skLineSegment(sketch, "E4.167.0", {"start": v(-182.63, 89.08) * mm, "end": v(-179.41, 95.4) * mm});
            skLineSegment(sketch, "E4.168.0", {"start": v(-185.63, 82.65) * mm, "end": v(-182.63, 89.08) * mm});
            skLineSegment(sketch, "E4.169.0", {"start": v(-188.4, 76.12) * mm, "end": v(-185.63, 82.65) * mm});
            skLineSegment(sketch, "E4.170.0", {"start": v(-190.95, 69.5) * mm, "end": v(-188.4, 76.12) * mm});
            skLineSegment(sketch, "E4.171.0", {"start": v(-193.25, 62.8) * mm, "end": v(-190.95, 69.5) * mm});
            skLineSegment(sketch, "E4.172.0", {"start": v(-195.33, 56) * mm, "end": v(-193.25, 62.8) * mm});
            skLineSegment(sketch, "E4.173.0", {"start": v(-197.16, 49.16) * mm, "end": v(-195.33, 56) * mm});
            skLineSegment(sketch, "E4.174.0", {"start": v(-198.76, 42.25) * mm, "end": v(-197.16, 49.16) * mm});
            skLineSegment(sketch, "E4.175.0", {"start": v(-200.11, 35.29) * mm, "end": v(-198.76, 42.25) * mm});
            skLineSegment(sketch, "E4.176.0", {"start": v(-201.22, 28.28) * mm, "end": v(-200.11, 35.29) * mm});
            skLineSegment(sketch, "E4.177.0", {"start": v(-202.09, 21.24) * mm, "end": v(-201.22, 28.28) * mm});
            skLineSegment(sketch, "E4.178.0", {"start": v(-202.7, 14.17) * mm, "end": v(-202.09, 21.24) * mm});
            skLineSegment(sketch, "E4.179.0", {"start": v(-203.08, 7.1) * mm, "end": v(-202.7, 14.17) * mm});
            skLineSegment(sketch, "E5", {"start": v(-152.4, 0) * mm, "end": v(-152.3, 5.32) * mm});
            skLineSegment(sketch, "E6.1.0", {"start": v(-150.92, -21.2) * mm, "end": v(-151.57, -15.93) * mm});
            skLineSegment(sketch, "E6.2.0", {"start": v(-146.5, -42) * mm, "end": v(-147.87, -36.87) * mm});
            skLineSegment(sketch, "E6.3.0", {"start": v(-139.22, -61.99) * mm, "end": v(-141.3, -57.1) * mm});
            skLineSegment(sketch, "E6.4.0", {"start": v(-129.24, -80.76) * mm, "end": v(-131.98, -76.2) * mm});
            skLineSegment(sketch, "E6.5.0", {"start": v(-116.75, -97.96) * mm, "end": v(-120.1, -93.83) * mm});
            skLineSegment(sketch, "E6.6.0", {"start": v(-101.98, -113.26) * mm, "end": v(-105.87, -109.63) * mm});
            skLineSegment(sketch, "E6.7.0", {"start": v(-85.22, -126.35) * mm, "end": v(-89.58, -123.3) * mm});
            skLineSegment(sketch, "E6.8.0", {"start": v(-66.8, -136.98) * mm, "end": v(-71.55, -134.56) * mm});
            skLineSegment(sketch, "E6.9.0", {"start": v(-47.1, -144.94) * mm, "end": v(-52.12, -143.2) * mm});
            skLineSegment(sketch, "E6.10.0", {"start": v(-26.46, -150.08) * mm, "end": v(-31.69, -149.07) * mm});
            skLineSegment(sketch, "E6.11.0", {"start": v(-5.32, -152.3) * mm, "end": v(-10.63, -152.03) * mm});
            skLineSegment(sketch, "E6.12.0", {"start": v(15.93, -151.57) * mm, "end": v(10.63, -152.03) * mm});
            skLineSegment(sketch, "E6.13.0", {"start": v(36.87, -147.87) * mm, "end": v(31.69, -149.07) * mm});
            skLineSegment(sketch, "E6.14.0", {"start": v(57.1, -141.3) * mm, "end": v(52.12, -143.2) * mm});
            skLineSegment(sketch, "E6.15.0", {"start": v(76.2, -131.98) * mm, "end": v(71.55, -134.56) * mm});
            skLineSegment(sketch, "E6.16.0", {"start": v(93.83, -120.1) * mm, "end": v(89.58, -123.3) * mm});
            skLineSegment(sketch, "E6.17.0", {"start": v(109.63, -105.87) * mm, "end": v(105.87, -109.63) * mm});
            skLineSegment(sketch, "E6.18.0", {"start": v(123.3, -89.58) * mm, "end": v(120.1, -93.83) * mm});
            skLineSegment(sketch, "E6.19.0", {"start": v(134.56, -71.55) * mm, "end": v(131.98, -76.2) * mm});
            skLineSegment(sketch, "E6.20.0", {"start": v(143.2, -52.12) * mm, "end": v(141.3, -57.1) * mm});
            skLineSegment(sketch, "E6.21.0", {"start": v(149.07, -31.69) * mm, "end": v(147.87, -36.87) * mm});
            skLineSegment(sketch, "E6.22.0", {"start": v(152.03, -10.63) * mm, "end": v(151.57, -15.93) * mm});
            skLineSegment(sketch, "E6.23.0", {"start": v(152.03, 10.63) * mm, "end": v(152.3, 5.32) * mm});
            skLineSegment(sketch, "E6.24.0", {"start": v(149.07, 31.69) * mm, "end": v(150.08, 26.46) * mm});
            skLineSegment(sketch, "E6.25.0", {"start": v(143.2, 52.12) * mm, "end": v(144.94, 47.1) * mm});
            skLineSegment(sketch, "E6.26.0", {"start": v(134.56, 71.55) * mm, "end": v(136.98, 66.8) * mm});
            skLineSegment(sketch, "E6.27.0", {"start": v(123.3, 89.58) * mm, "end": v(126.35, 85.22) * mm});
            skLineSegment(sketch, "E6.28.0", {"start": v(109.63, 105.87) * mm, "end": v(113.26, 101.98) * mm});
            skLineSegment(sketch, "E6.29.0", {"start": v(93.83, 120.1) * mm, "end": v(97.96, 116.75) * mm});
            skLineSegment(sketch, "E6.30.0", {"start": v(76.2, 131.98) * mm, "end": v(80.76, 129.24) * mm});
            skLineSegment(sketch, "E6.31.0", {"start": v(57.1, 141.3) * mm, "end": v(61.99, 139.22) * mm});
            skLineSegment(sketch, "E6.32.0", {"start": v(36.87, 147.87) * mm, "end": v(42, 146.5) * mm});
            skLineSegment(sketch, "E6.33.0", {"start": v(15.93, 151.57) * mm, "end": v(21.2, 150.92) * mm});
            skLineSegment(sketch, "E6.34.0", {"start": v(-5.32, 152.3) * mm, "end": v(0, 152.4) * mm});
            skLineSegment(sketch, "E6.35.0", {"start": v(-26.46, 150.08) * mm, "end": v(-21.2, 150.92) * mm});
            skLineSegment(sketch, "E6.36.0", {"start": v(-47.1, 144.94) * mm, "end": v(-42, 146.5) * mm});
            skLineSegment(sketch, "E6.37.0", {"start": v(-66.8, 136.98) * mm, "end": v(-61.99, 139.22) * mm});
            skLineSegment(sketch, "E6.38.0", {"start": v(-85.22, 126.35) * mm, "end": v(-80.76, 129.24) * mm});
            skLineSegment(sketch, "E6.39.0", {"start": v(-101.98, 113.26) * mm, "end": v(-97.96, 116.75) * mm});
            skLineSegment(sketch, "E6.40.0", {"start": v(-116.75, 97.96) * mm, "end": v(-113.26, 101.98) * mm});
            skLineSegment(sketch, "E6.41.0", {"start": v(-129.24, 80.76) * mm, "end": v(-126.35, 85.22) * mm});
            skLineSegment(sketch, "E6.42.0", {"start": v(-139.22, 61.99) * mm, "end": v(-136.98, 66.8) * mm});
            skLineSegment(sketch, "E6.43.0", {"start": v(-146.5, 42) * mm, "end": v(-144.94, 47.1) * mm});
            skLineSegment(sketch, "E6.44.0", {"start": v(-150.92, 21.2) * mm, "end": v(-150.08, 26.46) * mm});
            skCircle(sketch, "E7", {"center": v(0, 0) * mm, "radius": 12.7 * mm});
            skSolve(sketch);
        }
        {
            var Q0;
            Q0=makeQuery(id+"F0.imprint","IMPRINT",FACE,{"disambiguationData":[TD([[makeQuery(id+"F0.imprint","IMPRINT",EDGE,{"derivedFrom":sQuery(id+"F0.wireOp",EDGE,"E1")}),-1.0]])]});
            extrude(context, id + "F1", {"entities" : qUnion([Q0]), "depth" : 12.7 * mm, "hasDraft" : true, "draftAngle" : 28.35 * degree, "draftPullDirection" : true});
        }
        {
            var Q0;
            Q0=makeQuery(id+"F0.imprint","IMPRINT",FACE,{"disambiguationData":[TD([[makeQuery(id+"F0.imprint","IMPRINT",EDGE,{"derivedFrom":sQuery(id+"F0.wireOp",EDGE,"E1")}),-1.0]])]});
            var Q1;
            Q1=makeQuery(id+"F1.opExtrude","CAP_FACE",FACE,{"disambiguationData":[OSD([sQuery(id+"F0.wireOp",EDGE,"E1"),sQuery(id+"F0.wireOp",EDGE,"E2.3.0"),sQuery(id+"F0.wireOp",EDGE,"E2.4.0"),sQuery(id+"F0.wireOp",EDGE,"E2.7.0"),sQuery(id+"F0.wireOp",EDGE,"E2.8.0"),sQuery(id+"F0.wireOp",EDGE,"E2.11.0"),sQuery(id+"F0.wireOp",EDGE,"E2.12.0"),sQuery(id+"F0.wireOp",EDGE,"E2.15.0"),sQuery(id+"F0.wireOp",EDGE,"E2.16.0"),sQuery(id+"F0.wireOp",EDGE,"E2.19.0"),sQuery(id+"F0.wireOp",EDGE,"E2.20.0"),sQuery(id+"F0.wireOp",EDGE,"E2.23.0"),sQuery(id+"F0.wireOp",EDGE,"E2.24.0"),sQuery(id+"F0.wireOp",EDGE,"E2.27.0"),sQuery(id+"F0.wireOp",EDGE,"E2.28.0"),sQuery(id+"F0.wireOp",EDGE,"E2.31.0"),sQuery(id+"F0.wireOp",EDGE,"E2.32.0"),sQuery(id+"F0.wireOp",EDGE,"E2.35.0"),sQuery(id+"F0.wireOp",EDGE,"E2.36.0"),sQuery(id+"F0.wireOp",EDGE,"E2.39.0"),sQuery(id+"F0.wireOp",EDGE,"E2.40.0"),sQuery(id+"F0.wireOp",EDGE,"E2.43.0"),sQuery(id+"F0.wireOp",EDGE,"E2.44.0"),sQuery(id+"F0.wireOp",EDGE,"E2.47.0"),sQuery(id+"F0.wireOp",EDGE,"E2.48.0"),sQuery(id+"F0.wireOp",EDGE,"E2.51.0"),sQuery(id+"F0.wireOp",EDGE,"E2.52.0"),sQuery(id+"F0.wireOp",EDGE,"E2.55.0"),sQuery(id+"F0.wireOp",EDGE,"E2.56.0"),sQuery(id+"F0.wireOp",EDGE,"E2.59.0"),sQuery(id+"F0.wireOp",EDGE,"E2.60.0"),sQuery(id+"F0.wireOp",EDGE,"E2.63.0"),sQuery(id+"F0.wireOp",EDGE,"E2.64.0"),sQuery(id+"F0.wireOp",EDGE,"E2.67.0"),sQuery(id+"F0.wireOp",EDGE,"E2.68.0"),sQuery(id+"F0.wireOp",EDGE,"E2.71.0"),sQuery(id+"F0.wireOp",EDGE,"E2.72.0"),sQuery(id+"F0.wireOp",EDGE,"E2.75.0"),sQuery(id+"F0.wireOp",EDGE,"E2.76.0"),sQuery(id+"F0.wireOp",EDGE,"E2.79.0"),sQuery(id+"F0.wireOp",EDGE,"E2.80.0"),sQuery(id+"F0.wireOp",EDGE,"E2.83.0"),sQuery(id+"F0.wireOp",EDGE,"E2.84.0"),sQuery(id+"F0.wireOp",EDGE,"E2.87.0"),sQuery(id+"F0.wireOp",EDGE,"E2.88.0"),sQuery(id+"F0.wireOp",EDGE,"E2.91.0"),sQuery(id+"F0.wireOp",EDGE,"E2.92.0"),sQuery(id+"F0.wireOp",EDGE,"E2.95.0"),sQuery(id+"F0.wireOp",EDGE,"E2.96.0"),sQuery(id+"F0.wireOp",EDGE,"E2.99.0"),sQuery(id+"F0.wireOp",EDGE,"E2.100.0"),sQuery(id+"F0.wireOp",EDGE,"E2.103.0"),sQuery(id+"F0.wireOp",EDGE,"E2.104.0"),sQuery(id+"F0.wireOp",EDGE,"E2.107.0"),sQuery(id+"F0.wireOp",EDGE,"E2.108.0"),sQuery(id+"F0.wireOp",EDGE,"E2.111.0"),sQuery(id+"F0.wireOp",EDGE,"E2.112.0"),sQuery(id+"F0.wireOp",EDGE,"E2.115.0"),sQuery(id+"F0.wireOp",EDGE,"E2.116.0"),sQuery(id+"F0.wireOp",EDGE,"E2.119.0"),sQuery(id+"F0.wireOp",EDGE,"E2.120.0"),sQuery(id+"F0.wireOp",EDGE,"E2.123.0"),sQuery(id+"F0.wireOp",EDGE,"E2.124.0"),sQuery(id+"F0.wireOp",EDGE,"E2.127.0"),sQuery(id+"F0.wireOp",EDGE,"E2.128.0"),sQuery(id+"F0.wireOp",EDGE,"E2.131.0"),sQuery(id+"F0.wireOp",EDGE,"E2.132.0"),sQuery(id+"F0.wireOp",EDGE,"E2.135.0"),sQuery(id+"F0.wireOp",EDGE,"E2.136.0"),sQuery(id+"F0.wireOp",EDGE,"E2.139.0"),sQuery(id+"F0.wireOp",EDGE,"E2.140.0"),sQuery(id+"F0.wireOp",EDGE,"E2.143.0"),sQuery(id+"F0.wireOp",EDGE,"E2.144.0"),sQuery(id+"F0.wireOp",EDGE,"E2.147.0"),sQuery(id+"F0.wireOp",EDGE,"E2.148.0"),sQuery(id+"F0.wireOp",EDGE,"E2.151.0"),sQuery(id+"F0.wireOp",EDGE,"E2.152.0"),sQuery(id+"F0.wireOp",EDGE,"E2.155.0"),sQuery(id+"F0.wireOp",EDGE,"E2.156.0"),sQuery(id+"F0.wireOp",EDGE,"E2.159.0"),sQuery(id+"F0.wireOp",EDGE,"E2.160.0"),sQuery(id+"F0.wireOp",EDGE,"E2.163.0"),sQuery(id+"F0.wireOp",EDGE,"E2.164.0"),sQuery(id+"F0.wireOp",EDGE,"E2.167.0"),sQuery(id+"F0.wireOp",EDGE,"E2.168.0"),sQuery(id+"F0.wireOp",EDGE,"E2.171.0"),sQuery(id+"F0.wireOp",EDGE,"E2.172.0"),sQuery(id+"F0.wireOp",EDGE,"E2.175.0"),sQuery(id+"F0.wireOp",EDGE,"E2.176.0"),sQuery(id+"F0.wireOp",EDGE,"E2.179.0"),sQuery(id+"F0.wireOp",EDGE,"E4.1.0"),sQuery(id+"F0.wireOp",EDGE,"E4.2.0"),sQuery(id+"F0.wireOp",EDGE,"E4.3.0"),sQuery(id+"F0.wireOp",EDGE,"E4.5.0"),sQuery(id+"F0.wireOp",EDGE,"E4.6.0"),sQuery(id+"F0.wireOp",EDGE,"E4.7.0"),sQuery(id+"F0.wireOp",EDGE,"E4.9.0"),sQuery(id+"F0.wireOp",EDGE,"E4.10.0"),sQuery(id+"F0.wireOp",EDGE,"E4.11.0"),sQuery(id+"F0.wireOp",EDGE,"E4.13.0"),sQuery(id+"F0.wireOp",EDGE,"E4.14.0"),sQuery(id+"F0.wireOp",EDGE,"E4.15.0"),sQuery(id+"F0.wireOp",EDGE,"E4.17.0"),sQuery(id+"F0.wireOp",EDGE,"E4.18.0"),sQuery(id+"F0.wireOp",EDGE,"E4.19.0"),sQuery(id+"F0.wireOp",EDGE,"E4.21.0"),sQuery(id+"F0.wireOp",EDGE,"E4.22.0"),sQuery(id+"F0.wireOp",EDGE,"E4.23.0"),sQuery(id+"F0.wireOp",EDGE,"E4.25.0"),sQuery(id+"F0.wireOp",EDGE,"E4.26.0"),sQuery(id+"F0.wireOp",EDGE,"E4.27.0"),sQuery(id+"F0.wireOp",EDGE,"E4.29.0"),sQuery(id+"F0.wireOp",EDGE,"E4.30.0"),sQuery(id+"F0.wireOp",EDGE,"E4.31.0"),sQuery(id+"F0.wireOp",EDGE,"E4.33.0"),sQuery(id+"F0.wireOp",EDGE,"E4.34.0"),sQuery(id+"F0.wireOp",EDGE,"E4.35.0"),sQuery(id+"F0.wireOp",EDGE,"E4.37.0"),sQuery(id+"F0.wireOp",EDGE,"E4.38.0"),sQuery(id+"F0.wireOp",EDGE,"E4.39.0"),sQuery(id+"F0.wireOp",EDGE,"E4.41.0"),sQuery(id+"F0.wireOp",EDGE,"E4.42.0"),sQuery(id+"F0.wireOp",EDGE,"E4.43.0"),sQuery(id+"F0.wireOp",EDGE,"E4.45.0"),sQuery(id+"F0.wireOp",EDGE,"E4.46.0"),sQuery(id+"F0.wireOp",EDGE,"E4.47.0"),sQuery(id+"F0.wireOp",EDGE,"E4.49.0"),sQuery(id+"F0.wireOp",EDGE,"E4.50.0"),sQuery(id+"F0.wireOp",EDGE,"E4.51.0"),sQuery(id+"F0.wireOp",EDGE,"E4.53.0"),sQuery(id+"F0.wireOp",EDGE,"E4.54.0"),sQuery(id+"F0.wireOp",EDGE,"E4.55.0"),sQuery(id+"F0.wireOp",EDGE,"E4.57.0"),sQuery(id+"F0.wireOp",EDGE,"E4.58.0"),sQuery(id+"F0.wireOp",EDGE,"E4.59.0"),sQuery(id+"F0.wireOp",EDGE,"E4.61.0"),sQuery(id+"F0.wireOp",EDGE,"E4.62.0"),sQuery(id+"F0.wireOp",EDGE,"E4.63.0"),sQuery(id+"F0.wireOp",EDGE,"E4.65.0"),sQuery(id+"F0.wireOp",EDGE,"E4.66.0"),sQuery(id+"F0.wireOp",EDGE,"E4.67.0"),sQuery(id+"F0.wireOp",EDGE,"E4.69.0"),sQuery(id+"F0.wireOp",EDGE,"E4.70.0"),sQuery(id+"F0.wireOp",EDGE,"E4.71.0"),sQuery(id+"F0.wireOp",EDGE,"E4.73.0"),sQuery(id+"F0.wireOp",EDGE,"E4.74.0"),sQuery(id+"F0.wireOp",EDGE,"E4.75.0"),sQuery(id+"F0.wireOp",EDGE,"E4.77.0"),sQuery(id+"F0.wireOp",EDGE,"E4.78.0"),sQuery(id+"F0.wireOp",EDGE,"E4.79.0"),sQuery(id+"F0.wireOp",EDGE,"E4.81.0"),sQuery(id+"F0.wireOp",EDGE,"E4.82.0"),sQuery(id+"F0.wireOp",EDGE,"E4.83.0"),sQuery(id+"F0.wireOp",EDGE,"E4.85.0"),sQuery(id+"F0.wireOp",EDGE,"E4.86.0"),sQuery(id+"F0.wireOp",EDGE,"E4.87.0"),sQuery(id+"F0.wireOp",EDGE,"E4.89.0"),sQuery(id+"F0.wireOp",EDGE,"E4.90.0"),sQuery(id+"F0.wireOp",EDGE,"E4.91.0"),sQuery(id+"F0.wireOp",EDGE,"E4.93.0"),sQuery(id+"F0.wireOp",EDGE,"E4.94.0"),sQuery(id+"F0.wireOp",EDGE,"E4.95.0"),sQuery(id+"F0.wireOp",EDGE,"E4.97.0"),sQuery(id+"F0.wireOp",EDGE,"E4.98.0"),sQuery(id+"F0.wireOp",EDGE,"E4.99.0"),sQuery(id+"F0.wireOp",EDGE,"E4.101.0"),sQuery(id+"F0.wireOp",EDGE,"E4.102.0"),sQuery(id+"F0.wireOp",EDGE,"E4.103.0"),sQuery(id+"F0.wireOp",EDGE,"E4.105.0"),sQuery(id+"F0.wireOp",EDGE,"E4.106.0"),sQuery(id+"F0.wireOp",EDGE,"E4.107.0"),sQuery(id+"F0.wireOp",EDGE,"E4.109.0"),sQuery(id+"F0.wireOp",EDGE,"E4.110.0"),sQuery(id+"F0.wireOp",EDGE,"E4.111.0"),sQuery(id+"F0.wireOp",EDGE,"E4.113.0"),sQuery(id+"F0.wireOp",EDGE,"E4.114.0"),sQuery(id+"F0.wireOp",EDGE,"E4.115.0"),sQuery(id+"F0.wireOp",EDGE,"E4.117.0"),sQuery(id+"F0.wireOp",EDGE,"E4.118.0"),sQuery(id+"F0.wireOp",EDGE,"E4.119.0"),sQuery(id+"F0.wireOp",EDGE,"E4.121.0"),sQuery(id+"F0.wireOp",EDGE,"E4.122.0"),sQuery(id+"F0.wireOp",EDGE,"E4.123.0"),sQuery(id+"F0.wireOp",EDGE,"E4.125.0"),sQuery(id+"F0.wireOp",EDGE,"E4.126.0"),sQuery(id+"F0.wireOp",EDGE,"E4.127.0"),sQuery(id+"F0.wireOp",EDGE,"E4.129.0"),sQuery(id+"F0.wireOp",EDGE,"E4.130.0"),sQuery(id+"F0.wireOp",EDGE,"E4.131.0"),sQuery(id+"F0.wireOp",EDGE,"E4.133.0"),sQuery(id+"F0.wireOp",EDGE,"E4.134.0"),sQuery(id+"F0.wireOp",EDGE,"E4.135.0"),sQuery(id+"F0.wireOp",EDGE,"E4.137.0"),sQuery(id+"F0.wireOp",EDGE,"E4.138.0"),sQuery(id+"F0.wireOp",EDGE,"E4.139.0"),sQuery(id+"F0.wireOp",EDGE,"E4.141.0"),sQuery(id+"F0.wireOp",EDGE,"E4.142.0"),sQuery(id+"F0.wireOp",EDGE,"E4.143.0"),sQuery(id+"F0.wireOp",EDGE,"E4.145.0"),sQuery(id+"F0.wireOp",EDGE,"E4.146.0"),sQuery(id+"F0.wireOp",EDGE,"E4.147.0"),sQuery(id+"F0.wireOp",EDGE,"E4.149.0"),sQuery(id+"F0.wireOp",EDGE,"E4.150.0"),sQuery(id+"F0.wireOp",EDGE,"E4.151.0"),sQuery(id+"F0.wireOp",EDGE,"E4.153.0"),sQuery(id+"F0.wireOp",EDGE,"E4.154.0"),sQuery(id+"F0.wireOp",EDGE,"E4.155.0"),sQuery(id+"F0.wireOp",EDGE,"E4.157.0"),sQuery(id+"F0.wireOp",EDGE,"E4.158.0"),sQuery(id+"F0.wireOp",EDGE,"E4.159.0"),sQuery(id+"F0.wireOp",EDGE,"E4.161.0"),sQuery(id+"F0.wireOp",EDGE,"E4.162.0"),sQuery(id+"F0.wireOp",EDGE,"E4.163.0"),sQuery(id+"F0.wireOp",EDGE,"E4.165.0"),sQuery(id+"F0.wireOp",EDGE,"E4.166.0"),sQuery(id+"F0.wireOp",EDGE,"E4.167.0"),sQuery(id+"F0.wireOp",EDGE,"E4.169.0"),sQuery(id+"F0.wireOp",EDGE,"E4.170.0"),sQuery(id+"F0.wireOp",EDGE,"E4.171.0"),sQuery(id+"F0.wireOp",EDGE,"E4.173.0"),sQuery(id+"F0.wireOp",EDGE,"E4.174.0"),sQuery(id+"F0.wireOp",EDGE,"E4.175.0"),sQuery(id+"F0.wireOp",EDGE,"E4.177.0"),sQuery(id+"F0.wireOp",EDGE,"E4.178.0"),sQuery(id+"F0.wireOp",EDGE,"E4.179.0"),sQuery(id+"F0.wireOp",EDGE,"E5"),sQuery(id+"F0.wireOp",EDGE,"E6.1.0"),sQuery(id+"F0.wireOp",EDGE,"E6.2.0"),sQuery(id+"F0.wireOp",EDGE,"E6.3.0"),sQuery(id+"F0.wireOp",EDGE,"E6.4.0"),sQuery(id+"F0.wireOp",EDGE,"E6.5.0"),sQuery(id+"F0.wireOp",EDGE,"E6.6.0"),sQuery(id+"F0.wireOp",EDGE,"E6.7.0"),sQuery(id+"F0.wireOp",EDGE,"E6.8.0"),sQuery(id+"F0.wireOp",EDGE,"E6.9.0"),sQuery(id+"F0.wireOp",EDGE,"E6.10.0"),sQuery(id+"F0.wireOp",EDGE,"E6.11.0"),sQuery(id+"F0.wireOp",EDGE,"E6.12.0"),sQuery(id+"F0.wireOp",EDGE,"E6.13.0"),sQuery(id+"F0.wireOp",EDGE,"E6.14.0"),sQuery(id+"F0.wireOp",EDGE,"E6.15.0"),sQuery(id+"F0.wireOp",EDGE,"E6.16.0"),sQuery(id+"F0.wireOp",EDGE,"E6.17.0"),sQuery(id+"F0.wireOp",EDGE,"E6.18.0"),sQuery(id+"F0.wireOp",EDGE,"E6.19.0"),sQuery(id+"F0.wireOp",EDGE,"E6.20.0"),sQuery(id+"F0.wireOp",EDGE,"E6.21.0"),sQuery(id+"F0.wireOp",EDGE,"E6.22.0"),sQuery(id+"F0.wireOp",EDGE,"E6.23.0"),sQuery(id+"F0.wireOp",EDGE,"E6.24.0"),sQuery(id+"F0.wireOp",EDGE,"E6.25.0"),sQuery(id+"F0.wireOp",EDGE,"E6.26.0"),sQuery(id+"F0.wireOp",EDGE,"E6.27.0"),sQuery(id+"F0.wireOp",EDGE,"E6.28.0"),sQuery(id+"F0.wireOp",EDGE,"E6.29.0"),sQuery(id+"F0.wireOp",EDGE,"E6.30.0"),sQuery(id+"F0.wireOp",EDGE,"E6.31.0"),sQuery(id+"F0.wireOp",EDGE,"E6.32.0"),sQuery(id+"F0.wireOp",EDGE,"E6.33.0"),sQuery(id+"F0.wireOp",EDGE,"E6.34.0"),sQuery(id+"F0.wireOp",EDGE,"E6.35.0"),sQuery(id+"F0.wireOp",EDGE,"E6.36.0"),sQuery(id+"F0.wireOp",EDGE,"E6.37.0"),sQuery(id+"F0.wireOp",EDGE,"E6.38.0"),sQuery(id+"F0.wireOp",EDGE,"E6.39.0"),sQuery(id+"F0.wireOp",EDGE,"E6.40.0"),sQuery(id+"F0.wireOp",EDGE,"E6.41.0"),sQuery(id+"F0.wireOp",EDGE,"E6.42.0"),sQuery(id+"F0.wireOp",EDGE,"E6.43.0"),sQuery(id+"F0.wireOp",EDGE,"E6.44.0")])],"isStart":true});
            var Q2;
            Q2=makeQuery(id+"F1.opExtrude","SWEPT_FACE",FACE,{"disambiguationData":[OSD([sQuery(id+"F0.wireOp",EDGE,"E4.94.0")])]});
            var Q3;
            Q3=makeQuery(id+"F0.imprint","IMPRINT",FACE,{"disambiguationData":[TD([[makeQuery(id+"F0.imprint","IMPRINT",EDGE,{"derivedFrom":sQuery(id+"F0.wireOp",EDGE,"E1")}),1.0]])]});
            var Q4;
            Q4=makeQuery(id+"F0.imprint","IMPRINT",FACE,{"disambiguationData":[TD([[makeQuery(id+"F0.imprint","IMPRINT",EDGE,{"derivedFrom":sQuery(id+"F0.wireOp",EDGE,"E2.175.0")}),-1.0]])]});
            var Q5;
            Q5=makeQuery(id+"F0.imprint","IMPRINT",FACE,{"disambiguationData":[TD([[makeQuery(id+"F0.imprint","IMPRINT",EDGE,{"derivedFrom":sQuery(id+"F0.wireOp",EDGE,"E2.87.0")}),-1.0]])]});
            var Q6;
            Q6=makeQuery(id+"F1.opExtrude","SWEPT_FACE",FACE,{"disambiguationData":[OSD([sQuery(id+"F0.wireOp",EDGE,"E4.95.0")])]});
            var Q7;
            Q7=makeQuery(id+"F0.imprint","IMPRINT",FACE,{"disambiguationData":[TD([[makeQuery(id+"F0.imprint","IMPRINT",EDGE,{"derivedFrom":sQuery(id+"F0.wireOp",EDGE,"E2.95.0")}),-1.0]])]});
            var Q8;
            Q8=makeQuery(id+"F0.imprint","IMPRINT",FACE,{"disambiguationData":[TD([[makeQuery(id+"F0.imprint","IMPRINT",EDGE,{"derivedFrom":sQuery(id+"F0.wireOp",EDGE,"E2.91.0")}),-1.0]])]});
            var Q9;
            Q9=makeQuery(id+"F1.opExtrude","SWEPT_FACE",FACE,{"disambiguationData":[OSD([sQuery(id+"F0.wireOp",EDGE,"E4.178.0")])]});
            var Q10;
            Q10=makeQuery(id+"F1.opExtrude","SWEPT_FACE",FACE,{"disambiguationData":[OSD([sQuery(id+"F0.wireOp",EDGE,"E2.96.0")])]});
            var Q11;
            Q11=makeQuery(id+"F1.opExtrude","SWEPT_FACE",FACE,{"disambiguationData":[OSD([sQuery(id+"F0.wireOp",EDGE,"E2.175.0")])]});
            var Q12;
            Q12=makeQuery(id+"F1.opExtrude","SWEPT_FACE",FACE,{"disambiguationData":[OSD([sQuery(id+"F0.wireOp",EDGE,"E4.2.0")])]});
            var Q13;
            Q13=makeQuery(id+"F1.opExtrude","SWEPT_FACE",FACE,{"disambiguationData":[OSD([sQuery(id+"F0.wireOp",EDGE,"E5")])]});
            var Q14;
            Q14=makeQuery(id+"F1.opExtrude","SWEPT_FACE",FACE,{"disambiguationData":[OSD([sQuery(id+"F0.wireOp",EDGE,"E4.90.0")])]});
            var Q15;
            Q15=makeQuery(id+"F1.opExtrude","SWEPT_FACE",FACE,{"disambiguationData":[OSD([sQuery(id+"F0.wireOp",EDGE,"E4.6.0")])]});
            var Q16;
            Q16=makeQuery(id+"F1.opExtrude","SWEPT_FACE",FACE,{"disambiguationData":[OSD([sQuery(id+"F0.wireOp",EDGE,"E2.3.0")])]});
            var Q17;
            Q17=makeQuery(id+"F0.imprint","IMPRINT",FACE,{"disambiguationData":[TD([[makeQuery(id+"F0.imprint","IMPRINT",EDGE,{"derivedFrom":sQuery(id+"F0.wireOp",EDGE,"E2.75.0")}),-1.0]])]});
            var Q18;
            Q18=makeQuery(id+"F0.imprint","IMPRINT",FACE,{"disambiguationData":[TD([[makeQuery(id+"F0.imprint","IMPRINT",EDGE,{"derivedFrom":sQuery(id+"F0.wireOp",EDGE,"E2.83.0")}),-1.0]])]});
            var Q19;
            Q19=makeQuery(id+"F0.imprint","IMPRINT",FACE,{"disambiguationData":[TD([[makeQuery(id+"F0.imprint","IMPRINT",EDGE,{"derivedFrom":sQuery(id+"F0.wireOp",EDGE,"E2.107.0")}),-1.0]])]});
            var Q20;
            Q20=makeQuery(id+"F0.imprint","IMPRINT",FACE,{"disambiguationData":[TD([[makeQuery(id+"F0.imprint","IMPRINT",EDGE,{"derivedFrom":sQuery(id+"F0.wireOp",EDGE,"E2.171.0")}),-1.0]])]});
            var Q21;
            Q21=makeQuery(id+"F0.imprint","IMPRINT",FACE,{"disambiguationData":[TD([[makeQuery(id+"F0.imprint","IMPRINT",EDGE,{"derivedFrom":sQuery(id+"F0.wireOp",EDGE,"E2.111.0")}),-1.0]])]});
            var Q22;
            Q22=makeQuery(id+"F1.opExtrude","SWEPT_FACE",FACE,{"disambiguationData":[OSD([sQuery(id+"F0.wireOp",EDGE,"E4.74.0")])]});
            var Q23;
            Q23=makeQuery(id+"F1.opExtrude","SWEPT_FACE",FACE,{"disambiguationData":[OSD([sQuery(id+"F0.wireOp",EDGE,"E2.95.0")])]});
            var Q24;
            Q24=makeQuery(id+"F1.opExtrude","SWEPT_FACE",FACE,{"disambiguationData":[OSD([sQuery(id+"F0.wireOp",EDGE,"E6.5.0")])]});
            var Q25;
            Q25=makeQuery(id+"F1.opExtrude","SWEPT_FACE",FACE,{"disambiguationData":[OSD([sQuery(id+"F0.wireOp",EDGE,"E4.10.0")])]});
            var Q26;
            Q26=makeQuery(id+"F0.imprint","IMPRINT",FACE,{"disambiguationData":[TD([[makeQuery(id+"F0.imprint","IMPRINT",EDGE,{"derivedFrom":sQuery(id+"F0.wireOp",EDGE,"E2.167.0")}),-1.0]])]});
            var Q27;
            Q27=makeQuery(id+"F0.imprint","IMPRINT",FACE,{"disambiguationData":[TD([[makeQuery(id+"F0.imprint","IMPRINT",EDGE,{"derivedFrom":sQuery(id+"F0.wireOp",EDGE,"E2.79.0")}),-1.0]])]});
            var Q28;
            Q28=makeQuery(id+"F1.opExtrude","SWEPT_FACE",FACE,{"disambiguationData":[OSD([sQuery(id+"F0.wireOp",EDGE,"E4.179.0")])]});
            var Q29;
            Q29=makeQuery(id+"F1.opExtrude","SWEPT_FACE",FACE,{"disambiguationData":[OSD([sQuery(id+"F0.wireOp",EDGE,"E6.20.0")])]});
            var Q30;
            Q30=makeQuery(id+"F1.opExtrude","SWEPT_FACE",FACE,{"disambiguationData":[OSD([sQuery(id+"F0.wireOp",EDGE,"E2.92.0")])]});
            var Q31;
            Q31=makeQuery(id+"F0.imprint","IMPRINT",FACE,{"disambiguationData":[TD([[makeQuery(id+"F0.imprint","IMPRINT",EDGE,{"derivedFrom":sQuery(id+"F0.wireOp",EDGE,"E2.159.0")}),-1.0]])]});
            var Q32;
            Q32=makeQuery(id+"F1.opExtrude","SWEPT_FACE",FACE,{"disambiguationData":[OSD([sQuery(id+"F0.wireOp",EDGE,"E4.93.0")])]});
            var Q33;
            Q33=makeQuery(id+"F1.opExtrude","SWEPT_FACE",FACE,{"disambiguationData":[OSD([sQuery(id+"F0.wireOp",EDGE,"E6.3.0")])]});
            var Q34;
            Q34=makeQuery(id+"F1.opExtrude","SWEPT_FACE",FACE,{"disambiguationData":[OSD([sQuery(id+"F0.wireOp",EDGE,"E6.22.0")])]});
            var Q35;
            Q35=makeQuery(id+"F1.opExtrude","SWEPT_FACE",FACE,{"disambiguationData":[OSD([sQuery(id+"F0.wireOp",EDGE,"E4.97.0")])]});
            var Q36;
            Q36=makeQuery(id+"F1.opExtrude","SWEPT_FACE",FACE,{"disambiguationData":[OSD([sQuery(id+"F0.wireOp",EDGE,"E4.75.0")])]});
            var Q37;
            Q37=makeQuery(id+"F1.opExtrude","SWEPT_FACE",FACE,{"disambiguationData":[OSD([sQuery(id+"F0.wireOp",EDGE,"E4.13.0")])]});
            var Q38;
            Q38=makeQuery(id+"F1.opExtrude","SWEPT_FACE",FACE,{"disambiguationData":[OSD([sQuery(id+"F0.wireOp",EDGE,"E6.23.0")])]});
            var Q39;
            Q39=makeQuery(id+"F1.opExtrude","SWEPT_FACE",FACE,{"disambiguationData":[OSD([sQuery(id+"F0.wireOp",EDGE,"E4.98.0")])]});
            var Q40;
            Q40=makeQuery(id+"F1.opExtrude","SWEPT_FACE",FACE,{"disambiguationData":[OSD([sQuery(id+"F0.wireOp",EDGE,"E2.100.0")])]});
            var Q41;
            Q41=makeQuery(id+"F1.opExtrude","SWEPT_FACE",FACE,{"disambiguationData":[OSD([sQuery(id+"F0.wireOp",EDGE,"E6.24.0")])]});
            var Q42;
            Q42=makeQuery(id+"F1.opExtrude","SWEPT_FACE",FACE,{"disambiguationData":[OSD([sQuery(id+"F0.wireOp",EDGE,"E2.167.0")])]});
            var Q43;
            Q43=makeQuery(id+"F1.opExtrude","SWEPT_FACE",FACE,{"disambiguationData":[OSD([sQuery(id+"F0.wireOp",EDGE,"E4.101.0")])]});
            var Q44;
            Q44=makeQuery(id+"F1.opExtrude","SWEPT_FACE",FACE,{"disambiguationData":[OSD([sQuery(id+"F0.wireOp",EDGE,"E2.72.0")])]});
            var Q45;
            Q45=makeQuery(id+"F1.opExtrude","SWEPT_FACE",FACE,{"disambiguationData":[OSD([sQuery(id+"F0.wireOp",EDGE,"E2.104.0")])]});
            var Q46;
            Q46=makeQuery(id+"F1.opExtrude","SWEPT_FACE",FACE,{"disambiguationData":[OSD([sQuery(id+"F0.wireOp",EDGE,"E4.81.0")])]});
            var Q47;
            Q47=makeQuery(id+"F1.opExtrude","SWEPT_FACE",FACE,{"disambiguationData":[OSD([sQuery(id+"F0.wireOp",EDGE,"E2.171.0")])]});
            var Q48;
            Q48=makeQuery(id+"F1.opExtrude","SWEPT_FACE",FACE,{"disambiguationData":[OSD([sQuery(id+"F0.wireOp",EDGE,"E6.43.0")])]});
            var Q49;
            Q49=makeQuery(id+"F1.opExtrude","SWEPT_FACE",FACE,{"disambiguationData":[OSD([sQuery(id+"F0.wireOp",EDGE,"E4.103.0")])]});
            var Q50;
            Q50=makeQuery(id+"F1.opExtrude","SWEPT_FACE",FACE,{"disambiguationData":[OSD([sQuery(id+"F0.wireOp",EDGE,"E2.76.0")])]});
            var Q51;
            Q51=makeQuery(id+"F1.opExtrude","SWEPT_FACE",FACE,{"disambiguationData":[OSD([sQuery(id+"F0.wireOp",EDGE,"E6.44.0")])]});
            var Q52;
            Q52=makeQuery(id+"F1.opExtrude","SWEPT_FACE",FACE,{"disambiguationData":[OSD([sQuery(id+"F0.wireOp",EDGE,"E4.83.0")])]});
            var Q53;
            Q53=makeQuery(id+"F1.opExtrude","SWEPT_FACE",FACE,{"disambiguationData":[OSD([sQuery(id+"F0.wireOp",EDGE,"E4.105.0")])]});
            var Q54;
            Q54=makeQuery(id+"F1.opExtrude","SWEPT_FACE",FACE,{"disambiguationData":[OSD([sQuery(id+"F0.wireOp",EDGE,"E4.106.0")])]});
            var Q55;
            Q55=makeQuery(id+"F1.opExtrude","SWEPT_FACE",FACE,{"disambiguationData":[OSD([sQuery(id+"F0.wireOp",EDGE,"E4.86.0")])]});
            var Q56;
            Q56=makeQuery(id+"F1.opExtrude","SWEPT_FACE",FACE,{"disambiguationData":[OSD([sQuery(id+"F0.wireOp",EDGE,"E2.112.0")])]});
            var Q57;
            Q57=makeQuery(id+"F1.opExtrude","SWEPT_FACE",FACE,{"disambiguationData":[OSD([sQuery(id+"F0.wireOp",EDGE,"E4.1.0")])]});
            var Q58;
            Q58=makeQuery(id+"F1.opExtrude","SWEPT_FACE",FACE,{"disambiguationData":[OSD([sQuery(id+"F0.wireOp",EDGE,"E2.176.0")])]});
            var Q59;
            Q59=makeQuery(id+"F1.opExtrude","SWEPT_FACE",FACE,{"disambiguationData":[OSD([sQuery(id+"F0.wireOp",EDGE,"E4.109.0")])]});
            var Q60;
            Q60=makeQuery(id+"F1.opExtrude","SWEPT_FACE",FACE,{"disambiguationData":[OSD([sQuery(id+"F0.wireOp",EDGE,"E2.179.0")])]});
            var Q61;
            Q61=makeQuery(id+"F1.opExtrude","SWEPT_FACE",FACE,{"disambiguationData":[OSD([sQuery(id+"F0.wireOp",EDGE,"E4.87.0")])]});
            var Q62;
            Q62=makeQuery(id+"F1.opExtrude","SWEPT_FACE",FACE,{"disambiguationData":[OSD([sQuery(id+"F0.wireOp",EDGE,"E4.3.0")])]});
            var Q63;
            Q63=makeQuery(id+"F1.opExtrude","SWEPT_FACE",FACE,{"disambiguationData":[OSD([sQuery(id+"F0.wireOp",EDGE,"E4.89.0")])]});
            var Q64;
            Q64=makeQuery(id+"F1.opExtrude","SWEPT_FACE",FACE,{"disambiguationData":[OSD([sQuery(id+"F0.wireOp",EDGE,"E4.110.0")])]});
            var Q65;
            Q65=makeQuery(id+"F1.opExtrude","SWEPT_FACE",FACE,{"disambiguationData":[OSD([sQuery(id+"F0.wireOp",EDGE,"E2.87.0")])]});
            var Q66;
            Q66=makeQuery(id+"F1.opExtrude","SWEPT_FACE",FACE,{"disambiguationData":[OSD([sQuery(id+"F0.wireOp",EDGE,"E4.5.0")])]});
            var Q67;
            Q67=makeQuery(id+"F1.opExtrude","SWEPT_FACE",FACE,{"disambiguationData":[OSD([sQuery(id+"F0.wireOp",EDGE,"E6.1.0")])]});
            var Q68;
            Q68=makeQuery(id+"F1.opExtrude","SWEPT_FACE",FACE,{"disambiguationData":[OSD([sQuery(id+"F0.wireOp",EDGE,"E4.175.0")])]});
            var Q69;
            Q69=makeQuery(id+"F1.opExtrude","SWEPT_FACE",FACE,{"disambiguationData":[OSD([sQuery(id+"F0.wireOp",EDGE,"E6.2.0")])]});
            var Q70;
            Q70=makeQuery(id+"F1.opExtrude","SWEPT_FACE",FACE,{"disambiguationData":[OSD([sQuery(id+"F0.wireOp",EDGE,"E4.91.0")])]});
            var Q71;
            Q71=makeQuery(id+"F1.opExtrude","SWEPT_FACE",FACE,{"disambiguationData":[OSD([sQuery(id+"F0.wireOp",EDGE,"E2.4.0")])]});
            var Q72;
            Q72=makeQuery(id+"F1.opExtrude","SWEPT_FACE",FACE,{"disambiguationData":[OSD([sQuery(id+"F0.wireOp",EDGE,"E2.11.0")])]});
            var Q73;
            Q73=makeQuery(id+"F1.opExtrude","SWEPT_FACE",FACE,{"disambiguationData":[OSD([sQuery(id+"F0.wireOp",EDGE,"E2.15.0")])]});
            var Q74;
            Q74=makeQuery(id+"F1.opExtrude","SWEPT_FACE",FACE,{"disambiguationData":[OSD([sQuery(id+"F0.wireOp",EDGE,"E2.19.0")])]});
            var Q75;
            Q75=makeQuery(id+"F0.imprint","IMPRINT",FACE,{"disambiguationData":[TD([[makeQuery(id+"F0.imprint","IMPRINT",EDGE,{"derivedFrom":sQuery(id+"F0.wireOp",EDGE,"E2.3.0")}),-1.0]])]});
            var Q76;
            Q76=makeQuery(id+"F0.imprint","IMPRINT",FACE,{"disambiguationData":[TD([[makeQuery(id+"F0.imprint","IMPRINT",EDGE,{"derivedFrom":sQuery(id+"F0.wireOp",EDGE,"E2.71.0")}),-1.0]])]});
            var Q77;
            Q77=makeQuery(id+"F0.imprint","IMPRINT",FACE,{"disambiguationData":[TD([[makeQuery(id+"F0.imprint","IMPRINT",EDGE,{"derivedFrom":sQuery(id+"F0.wireOp",EDGE,"E2.7.0")}),-1.0]])]});
            var Q78;
            Q78=makeQuery(id+"F0.imprint","IMPRINT",FACE,{"disambiguationData":[TD([[makeQuery(id+"F0.imprint","IMPRINT",EDGE,{"derivedFrom":sQuery(id+"F0.wireOp",EDGE,"E2.103.0")}),-1.0]])]});
            var Q79;
            Q79=makeQuery(id+"F1.opExtrude","SWEPT_FACE",FACE,{"disambiguationData":[OSD([sQuery(id+"F0.wireOp",EDGE,"E4.73.0")])]});
            var Q80;
            Q80=makeQuery(id+"F1.opExtrude","SWEPT_FACE",FACE,{"disambiguationData":[OSD([sQuery(id+"F0.wireOp",EDGE,"E4.9.0")])]});
            var Q81;
            Q81=makeQuery(id+"F0.imprint","IMPRINT",FACE,{"disambiguationData":[TD([[makeQuery(id+"F0.imprint","IMPRINT",EDGE,{"derivedFrom":sQuery(id+"F0.wireOp",EDGE,"E2.163.0")}),-1.0]])]});
            var Q82;
            Q82=makeQuery(id+"F1.opExtrude","SWEPT_FACE",FACE,{"disambiguationData":[OSD([sQuery(id+"F0.wireOp",EDGE,"E6.4.0")])]});
            var Q83;
            Q83=makeQuery(id+"F1.opExtrude","SWEPT_FACE",FACE,{"disambiguationData":[OSD([sQuery(id+"F0.wireOp",EDGE,"E4.71.0")])]});
            var Q84;
            Q84=makeQuery(id+"F1.opExtrude","SWEPT_FACE",FACE,{"disambiguationData":[OSD([sQuery(id+"F0.wireOp",EDGE,"E4.7.0")])]});
            var Q85;
            Q85=makeQuery(id+"F1.opExtrude","SWEPT_FACE",FACE,{"disambiguationData":[OSD([sQuery(id+"F0.wireOp",EDGE,"E4.11.0")])]});
            var Q86;
            Q86=makeQuery(id+"F1.opExtrude","SWEPT_FACE",FACE,{"disambiguationData":[OSD([sQuery(id+"F0.wireOp",EDGE,"E2.163.0")])]});
            var Q87;
            Q87=makeQuery(id+"F1.opExtrude","SWEPT_FACE",FACE,{"disambiguationData":[OSD([sQuery(id+"F0.wireOp",EDGE,"E4.77.0")])]});
            var Q88;
            Q88=makeQuery(id+"F1.opExtrude","SWEPT_FACE",FACE,{"disambiguationData":[OSD([sQuery(id+"F0.wireOp",EDGE,"E6.40.0")])]});
            var Q89;
            Q89=makeQuery(id+"F1.opExtrude","SWEPT_FACE",FACE,{"disambiguationData":[OSD([sQuery(id+"F0.wireOp",EDGE,"E4.99.0")])]});
            var Q90;
            Q90=makeQuery(id+"F1.opExtrude","SWEPT_FACE",FACE,{"disambiguationData":[OSD([sQuery(id+"F0.wireOp",EDGE,"E4.78.0")])]});
            var Q91;
            Q91=makeQuery(id+"F1.opExtrude","SWEPT_FACE",FACE,{"disambiguationData":[OSD([sQuery(id+"F0.wireOp",EDGE,"E4.57.0")])]});
            var Q92;
            Q92=makeQuery(id+"F1.opExtrude","SWEPT_FACE",FACE,{"disambiguationData":[OSD([sQuery(id+"F0.wireOp",EDGE,"E2.71.0")])]});
            var Q93;
            Q93=makeQuery(id+"F1.opExtrude","SWEPT_FACE",FACE,{"disambiguationData":[OSD([sQuery(id+"F0.wireOp",EDGE,"E4.79.0")])]});
            var Q94;
            Q94=makeQuery(id+"F1.opExtrude","SWEPT_FACE",FACE,{"disambiguationData":[OSD([sQuery(id+"F0.wireOp",EDGE,"E2.168.0")])]});
            var Q95;
            Q95=makeQuery(id+"F1.opExtrude","SWEPT_FACE",FACE,{"disambiguationData":[OSD([sQuery(id+"F0.wireOp",EDGE,"E4.17.0")])]});
            var Q96;
            Q96=makeQuery(id+"F1.opExtrude","SWEPT_FACE",FACE,{"disambiguationData":[OSD([sQuery(id+"F0.wireOp",EDGE,"E6.42.0")])]});
            var Q97;
            Q97=makeQuery(id+"F1.opExtrude","SWEPT_FACE",FACE,{"disambiguationData":[OSD([sQuery(id+"F0.wireOp",EDGE,"E4.102.0")])]});
            var Q98;
            Q98=makeQuery(id+"F1.opExtrude","SWEPT_FACE",FACE,{"disambiguationData":[OSD([sQuery(id+"F0.wireOp",EDGE,"E4.59.0")])]});
            var Q99;
            Q99=makeQuery(id+"F1.opExtrude","SWEPT_FACE",FACE,{"disambiguationData":[OSD([sQuery(id+"F0.wireOp",EDGE,"E2.75.0")])]});
            var Q100;
            Q100=makeQuery(id+"F1.opExtrude","SWEPT_FACE",FACE,{"disambiguationData":[OSD([sQuery(id+"F0.wireOp",EDGE,"E6.27.0")])]});
            var Q101;
            Q101=makeQuery(id+"F1.opExtrude","SWEPT_FACE",FACE,{"disambiguationData":[OSD([sQuery(id+"F0.wireOp",EDGE,"E4.125.0")])]});
            var Q102;
            Q102=makeQuery(id+"F1.opExtrude","SWEPT_FACE",FACE,{"disambiguationData":[OSD([sQuery(id+"F0.wireOp",EDGE,"E4.82.0")])]});
            var Q103;
            Q103=makeQuery(id+"F1.opExtrude","SWEPT_FACE",FACE,{"disambiguationData":[OSD([sQuery(id+"F0.wireOp",EDGE,"E2.108.0")])]});
            var Q104;
            Q104=makeQuery(id+"F1.opExtrude","SWEPT_FACE",FACE,{"disambiguationData":[OSD([sQuery(id+"F0.wireOp",EDGE,"E2.172.0")])]});
            var Q105;
            Q105=makeQuery(id+"F1.opExtrude","SWEPT_FACE",FACE,{"disambiguationData":[OSD([sQuery(id+"F0.wireOp",EDGE,"E4.169.0")])]});
            var Q106;
            Q106=makeQuery(id+"F1.opExtrude","SWEPT_FACE",FACE,{"disambiguationData":[OSD([sQuery(id+"F0.wireOp",EDGE,"E4.126.0")])]});
            var Q107;
            Q107=makeQuery(id+"F1.opExtrude","SWEPT_FACE",FACE,{"disambiguationData":[OSD([sQuery(id+"F0.wireOp",EDGE,"E4.85.0")])]});
            var Q108;
            Q108=makeQuery(id+"F1.opExtrude","SWEPT_FACE",FACE,{"disambiguationData":[OSD([sQuery(id+"F0.wireOp",EDGE,"E4.170.0")])]});
            var Q109;
            Q109=makeQuery(id+"F1.opExtrude","SWEPT_FACE",FACE,{"disambiguationData":[OSD([sQuery(id+"F0.wireOp",EDGE,"E2.111.0")])]});
            var Q110;
            Q110=makeQuery(id+"F1.opExtrude","SWEPT_FACE",FACE,{"disambiguationData":[OSD([sQuery(id+"F0.wireOp",EDGE,"E4.171.0")])]});
            var Q111;
            Q111=makeQuery(id+"F1.opExtrude","SWEPT_FACE",FACE,{"disambiguationData":[OSD([sQuery(id+"F0.wireOp",EDGE,"E2.80.0")])]});
            var Q112;
            Q112=makeQuery(id+"F1.opExtrude","SWEPT_FACE",FACE,{"disambiguationData":[OSD([sQuery(id+"F0.wireOp",EDGE,"E4.173.0")])]});
            var Q113;
            Q113=makeQuery(id+"F1.opExtrude","SWEPT_FACE",FACE,{"disambiguationData":[OSD([sQuery(id+"F0.wireOp",EDGE,"E2.115.0")])]});
            var Q114;
            Q114=makeQuery(id+"F1.opExtrude","SWEPT_FACE",FACE,{"disambiguationData":[OSD([sQuery(id+"F0.wireOp",EDGE,"E2.83.0")])]});
            var Q115;
            Q115=makeQuery(id+"F1.opExtrude","SWEPT_FACE",FACE,{"disambiguationData":[OSD([sQuery(id+"F0.wireOp",EDGE,"E4.174.0")])]});
            var Q116;
            Q116=makeQuery(id+"F1.opExtrude","SWEPT_FACE",FACE,{"disambiguationData":[OSD([sQuery(id+"F0.wireOp",EDGE,"E4.111.0")])]});
            var Q117;
            Q117=makeQuery(id+"F1.opExtrude","SWEPT_FACE",FACE,{"disambiguationData":[OSD([sQuery(id+"F0.wireOp",EDGE,"E2.88.0")])]});
            var Q118;
            Q118=makeQuery(id+"F1.opExtrude","SWEPT_FACE",FACE,{"disambiguationData":[OSD([sQuery(id+"F0.wireOp",EDGE,"E4.177.0")])]});
            var Q119;
            Q119=makeQuery(id+"F1.opExtrude","SWEPT_FACE",FACE,{"disambiguationData":[OSD([sQuery(id+"F0.wireOp",EDGE,"E4.113.0")])]});
            var Q120;
            Q120=makeQuery(id+"F1.opExtrude","SWEPT_FACE",FACE,{"disambiguationData":[OSD([sQuery(id+"F0.wireOp",EDGE,"E1")])]});
            var Q121;
            Q121=makeQuery(id+"F1.opExtrude","SWEPT_FACE",FACE,{"disambiguationData":[OSD([sQuery(id+"F0.wireOp",EDGE,"E2.7.0")])]});
            var Q122;
            Q122=makeQuery(id+"F1.opExtrude","SWEPT_FACE",FACE,{"disambiguationData":[OSD([sQuery(id+"F0.wireOp",EDGE,"E2.8.0")])]});
            var Q123;
            Q123=makeQuery(id+"F1.opExtrude","SWEPT_FACE",FACE,{"disambiguationData":[OSD([sQuery(id+"F0.wireOp",EDGE,"E2.12.0")])]});
            var Q124;
            Q124=makeQuery(id+"F1.opExtrude","SWEPT_FACE",FACE,{"disambiguationData":[OSD([sQuery(id+"F0.wireOp",EDGE,"E2.16.0")])]});
            var Q125;
            Q125=makeQuery(id+"F1.opExtrude","SWEPT_FACE",FACE,{"disambiguationData":[OSD([sQuery(id+"F0.wireOp",EDGE,"E2.20.0")])]});
            var Q126;
            Q126=makeQuery(id+"F0.imprint","IMPRINT",FACE,{"disambiguationData":[TD([[makeQuery(id+"F0.imprint","IMPRINT",EDGE,{"derivedFrom":sQuery(id+"F0.wireOp",EDGE,"E2.15.0")}),-1.0]])]});
            var Q127;
            Q127=makeQuery(id+"F0.imprint","IMPRINT",FACE,{"disambiguationData":[TD([[makeQuery(id+"F0.imprint","IMPRINT",EDGE,{"derivedFrom":sQuery(id+"F0.wireOp",EDGE,"E2.11.0")}),-1.0]])]});
            var Q128;
            Q128=makeQuery(id+"F0.imprint","IMPRINT",FACE,{"disambiguationData":[TD([[makeQuery(id+"F0.imprint","IMPRINT",EDGE,{"derivedFrom":sQuery(id+"F0.wireOp",EDGE,"E2.115.0")}),-1.0]])]});
            var Q129;
            Q129=makeQuery(id+"F1.opExtrude","SWEPT_FACE",FACE,{"disambiguationData":[OSD([sQuery(id+"F0.wireOp",EDGE,"E2.159.0")])]});
            var Q130;
            Q130=makeQuery(id+"F1.opExtrude","SWEPT_FACE",FACE,{"disambiguationData":[OSD([sQuery(id+"F0.wireOp",EDGE,"E2.127.0")])]});
            var Q131;
            Q131=makeQuery(id+"F0.imprint","IMPRINT",FACE,{"disambiguationData":[TD([[makeQuery(id+"F0.imprint","IMPRINT",EDGE,{"derivedFrom":sQuery(id+"F0.wireOp",EDGE,"E2.99.0")}),-1.0]])]});
            var Q132;
            Q132=makeQuery(id+"F1.opExtrude","SWEPT_FACE",FACE,{"disambiguationData":[OSD([sQuery(id+"F0.wireOp",EDGE,"E2.124.0")])]});
            var Q133;
            Q133=makeQuery(id+"F0.imprint","IMPRINT",FACE,{"disambiguationData":[TD([[makeQuery(id+"F0.imprint","IMPRINT",EDGE,{"derivedFrom":sQuery(id+"F0.wireOp",EDGE,"E2.19.0")}),-1.0]])]});
            var Q134;
            Q134=makeQuery(id+"F1.opExtrude","SWEPT_FACE",FACE,{"disambiguationData":[OSD([sQuery(id+"F0.wireOp",EDGE,"E4.114.0")])]});
            var Q135;
            Q135=makeQuery(id+"F1.opExtrude","SWEPT_FACE",FACE,{"disambiguationData":[OSD([sQuery(id+"F0.wireOp",EDGE,"E6.19.0")])]});
            var Q136;
            Q136=makeQuery(id+"F1.opExtrude","SWEPT_FACE",FACE,{"disambiguationData":[OSD([sQuery(id+"F0.wireOp",EDGE,"E2.91.0")])]});
            var Q137;
            Q137=makeQuery(id+"F1.opExtrude","SWEPT_FACE",FACE,{"disambiguationData":[OSD([sQuery(id+"F0.wireOp",EDGE,"E6.6.0")])]});
            var Q138;
            Q138=makeQuery(id+"F1.opExtrude","SWEPT_FACE",FACE,{"disambiguationData":[OSD([sQuery(id+"F0.wireOp",EDGE,"E2.160.0")])]});
            var Q139;
            Q139=makeQuery(id+"F1.opExtrude","SWEPT_FACE",FACE,{"disambiguationData":[OSD([sQuery(id+"F0.wireOp",EDGE,"E2.68.0")])]});
            var Q140;
            Q140=makeQuery(id+"F1.opExtrude","SWEPT_FACE",FACE,{"disambiguationData":[OSD([sQuery(id+"F0.wireOp",EDGE,"E2.164.0")])]});
            var Q141;
            Q141=makeQuery(id+"F1.opExtrude","SWEPT_FACE",FACE,{"disambiguationData":[OSD([sQuery(id+"F0.wireOp",EDGE,"E4.14.0")])]});
            var Q142;
            Q142=makeQuery(id+"F1.opExtrude","SWEPT_FACE",FACE,{"disambiguationData":[OSD([sQuery(id+"F0.wireOp",EDGE,"E2.103.0")])]});
            var Q143;
            Q143=makeQuery(id+"F1.opExtrude","SWEPT_FACE",FACE,{"disambiguationData":[OSD([sQuery(id+"F0.wireOp",EDGE,"E4.15.0")])]});
            var Q144;
            Q144=makeQuery(id+"F1.opExtrude","SWEPT_FACE",FACE,{"disambiguationData":[OSD([sQuery(id+"F0.wireOp",EDGE,"E6.41.0")])]});
            var Q145;
            Q145=makeQuery(id+"F1.opExtrude","SWEPT_FACE",FACE,{"disambiguationData":[OSD([sQuery(id+"F0.wireOp",EDGE,"E4.58.0")])]});
            var Q146;
            Q146=makeQuery(id+"F1.opExtrude","SWEPT_FACE",FACE,{"disambiguationData":[OSD([sQuery(id+"F0.wireOp",EDGE,"E4.165.0")])]});
            var Q147;
            Q147=makeQuery(id+"F1.opExtrude","SWEPT_FACE",FACE,{"disambiguationData":[OSD([sQuery(id+"F0.wireOp",EDGE,"E2.107.0")])]});
            var Q148;
            Q148=makeQuery(id+"F1.opExtrude","SWEPT_FACE",FACE,{"disambiguationData":[OSD([sQuery(id+"F0.wireOp",EDGE,"E4.18.0")])]});
            var Q149;
            Q149=makeQuery(id+"F1.opExtrude","SWEPT_FACE",FACE,{"disambiguationData":[OSD([sQuery(id+"F0.wireOp",EDGE,"E6.28.0")])]});
            var Q150;
            Q150=makeQuery(id+"F1.opExtrude","SWEPT_FACE",FACE,{"disambiguationData":[OSD([sQuery(id+"F0.wireOp",EDGE,"E6.29.0")])]});
            var Q151;
            Q151=makeQuery(id+"F1.opExtrude","SWEPT_FACE",FACE,{"disambiguationData":[OSD([sQuery(id+"F0.wireOp",EDGE,"E4.127.0")])]});
            var Q152;
            Q152=makeQuery(id+"F1.opExtrude","SWEPT_FACE",FACE,{"disambiguationData":[OSD([sQuery(id+"F0.wireOp",EDGE,"E2.79.0")])]});
            var Q153;
            Q153=makeQuery(id+"F1.opExtrude","SWEPT_FACE",FACE,{"disambiguationData":[OSD([sQuery(id+"F0.wireOp",EDGE,"E4.107.0")])]});
            var Q154;
            Q154=makeQuery(id+"F1.opExtrude","SWEPT_FACE",FACE,{"disambiguationData":[OSD([sQuery(id+"F0.wireOp",EDGE,"E2.116.0")])]});
            var Q155;
            Q155=makeQuery(id+"F1.opExtrude","SWEPT_FACE",FACE,{"disambiguationData":[OSD([sQuery(id+"F0.wireOp",EDGE,"E2.84.0")])]});
            var Q156;
            Q156=makeQuery(id+"F1.opExtrude","SWEPT_FACE",FACE,{"disambiguationData":[OSD([sQuery(id+"F0.wireOp",EDGE,"E4.69.0")])]});
            var Q157;
            Q157=makeQuery(id+"F1.opExtrude","SWEPT_FACE",FACE,{"disambiguationData":[OSD([sQuery(id+"F0.wireOp",EDGE,"E2.56.0")])]});
            var Q158;
            Q158=makeQuery(id+"F1.opExtrude","SWEPT_FACE",FACE,{"disambiguationData":[OSD([sQuery(id+"F0.wireOp",EDGE,"E6.18.0")])]});
            var Q159;
            Q159=makeQuery(id+"F1.opExtrude","SWEPT_FACE",FACE,{"disambiguationData":[OSD([sQuery(id+"F0.wireOp",EDGE,"E4.70.0")])]});
            var Q160;
            Q160=makeQuery(id+"F1.opExtrude","SWEPT_FACE",FACE,{"disambiguationData":[OSD([sQuery(id+"F0.wireOp",EDGE,"E2.24.0")])]});
            var Q161;
            Q161=makeQuery(id+"F1.opExtrude","SWEPT_FACE",FACE,{"disambiguationData":[OSD([sQuery(id+"F0.wireOp",EDGE,"E4.117.0")])]});
            var Q162;
            Q162=makeQuery(id+"F1.opExtrude","SWEPT_FACE",FACE,{"disambiguationData":[OSD([sQuery(id+"F0.wireOp",EDGE,"E6.21.0")])]});
            var Q163;
            Q163=makeQuery(id+"F1.opExtrude","SWEPT_FACE",FACE,{"disambiguationData":[OSD([sQuery(id+"F0.wireOp",EDGE,"E4.115.0")])]});
            var Q164;
            Q164=makeQuery(id+"F0.imprint","IMPRINT",FACE,{"disambiguationData":[TD([[makeQuery(id+"F0.imprint","IMPRINT",EDGE,{"derivedFrom":sQuery(id+"F0.wireOp",EDGE,"E2.155.0")}),-1.0]])]});
            var Q165;
            Q165=makeQuery(id+"F0.imprint","IMPRINT",FACE,{"disambiguationData":[TD([[makeQuery(id+"F0.imprint","IMPRINT",EDGE,{"derivedFrom":sQuery(id+"F0.wireOp",EDGE,"E2.23.0")}),-1.0]])]});
            var Q166;
            Q166=makeQuery(id+"F0.imprint","IMPRINT",FACE,{"disambiguationData":[TD([[makeQuery(id+"F0.imprint","IMPRINT",EDGE,{"derivedFrom":sQuery(id+"F0.wireOp",EDGE,"E2.67.0")}),-1.0]])]});
            var Q167;
            Q167=makeQuery(id+"F1.opExtrude","SWEPT_FACE",FACE,{"disambiguationData":[OSD([sQuery(id+"F0.wireOp",EDGE,"E2.155.0")])]});
            var Q168;
            Q168=makeQuery(id+"F1.opExtrude","SWEPT_FACE",FACE,{"disambiguationData":[OSD([sQuery(id+"F0.wireOp",EDGE,"E2.128.0")])]});
            var Q169;
            Q169=makeQuery(id+"F1.opExtrude","SWEPT_FACE",FACE,{"disambiguationData":[OSD([sQuery(id+"F0.wireOp",EDGE,"E4.118.0")])]});
            var Q170;
            Q170=makeQuery(id+"F1.opExtrude","SWEPT_FACE",FACE,{"disambiguationData":[OSD([sQuery(id+"F0.wireOp",EDGE,"E4.161.0")])]});
            var Q171;
            Q171=makeQuery(id+"F1.opExtrude","SWEPT_FACE",FACE,{"disambiguationData":[OSD([sQuery(id+"F0.wireOp",EDGE,"E2.67.0")])]});
            var Q172;
            Q172=makeQuery(id+"F1.opExtrude","SWEPT_FACE",FACE,{"disambiguationData":[OSD([sQuery(id+"F0.wireOp",EDGE,"E6.7.0")])]});
            var Q173;
            Q173=makeQuery(id+"F1.opExtrude","SWEPT_FACE",FACE,{"disambiguationData":[OSD([sQuery(id+"F0.wireOp",EDGE,"E2.99.0")])]});
            var Q174;
            Q174=makeQuery(id+"F1.opExtrude","SWEPT_FACE",FACE,{"disambiguationData":[OSD([sQuery(id+"F0.wireOp",EDGE,"E6.39.0")])]});
            var Q175;
            Q175=makeQuery(id+"F1.opExtrude","SWEPT_FACE",FACE,{"disambiguationData":[OSD([sQuery(id+"F0.wireOp",EDGE,"E4.162.0")])]});
            var Q176;
            Q176=makeQuery(id+"F1.opExtrude","SWEPT_FACE",FACE,{"disambiguationData":[OSD([sQuery(id+"F0.wireOp",EDGE,"E4.163.0")])]});
            var Q177;
            Q177=makeQuery(id+"F1.opExtrude","SWEPT_FACE",FACE,{"disambiguationData":[OSD([sQuery(id+"F0.wireOp",EDGE,"E6.26.0")])]});
            var Q178;
            Q178=makeQuery(id+"F1.opExtrude","SWEPT_FACE",FACE,{"disambiguationData":[OSD([sQuery(id+"F0.wireOp",EDGE,"E4.166.0")])]});
            var Q179;
            Q179=makeQuery(id+"F1.opExtrude","SWEPT_FACE",FACE,{"disambiguationData":[OSD([sQuery(id+"F0.wireOp",EDGE,"E4.167.0")])]});
            var Q180;
            Q180=makeQuery(id+"F1.opExtrude","SWEPT_FACE",FACE,{"disambiguationData":[OSD([sQuery(id+"F0.wireOp",EDGE,"E4.19.0")])]});
            var Q181;
            Q181=makeQuery(id+"F1.opExtrude","SWEPT_FACE",FACE,{"disambiguationData":[OSD([sQuery(id+"F0.wireOp",EDGE,"E4.65.0")])]});
            var Q182;
            Q182=makeQuery(id+"F1.opExtrude","SWEPT_FACE",FACE,{"disambiguationData":[OSD([sQuery(id+"F0.wireOp",EDGE,"E4.66.0")])]});
            var Q183;
            Q183=makeQuery(id+"F1.opExtrude","SWEPT_FACE",FACE,{"disambiguationData":[OSD([sQuery(id+"F0.wireOp",EDGE,"E4.67.0")])]});
            var Q184;
            Q184=makeQuery(id+"F1.opExtrude","SWEPT_FACE",FACE,{"disambiguationData":[OSD([sQuery(id+"F0.wireOp",EDGE,"E2.119.0")])]});
            var Q185;
            Q185=makeQuery(id+"F1.opExtrude","SWEPT_FACE",FACE,{"disambiguationData":[OSD([sQuery(id+"F0.wireOp",EDGE,"E2.55.0")])]});
            var Q186;
            Q186=makeQuery(id+"F1.opExtrude","SWEPT_FACE",FACE,{"disambiguationData":[OSD([sQuery(id+"F0.wireOp",EDGE,"E6.17.0")])]});
            var Q187;
            Q187=makeQuery(id+"F1.opExtrude","SWEPT_FACE",FACE,{"disambiguationData":[OSD([sQuery(id+"F0.wireOp",EDGE,"E2.27.0")])]});
            var Q188;
            Q188=makeQuery(id+"F1.opExtrude","SWEPT_FACE",FACE,{"disambiguationData":[OSD([sQuery(id+"F0.wireOp",EDGE,"E2.23.0")])]});
            var Q189;
            Q189=makeQuery(id+"F0.imprint","IMPRINT",FACE,{"disambiguationData":[TD([[makeQuery(id+"F0.imprint","IMPRINT",EDGE,{"derivedFrom":sQuery(id+"F0.wireOp",EDGE,"E2.119.0")}),-1.0]])]});
            var Q190;
            Q190=makeQuery(id+"F0.imprint","IMPRINT",FACE,{"disambiguationData":[TD([[makeQuery(id+"F0.imprint","IMPRINT",EDGE,{"derivedFrom":sQuery(id+"F0.wireOp",EDGE,"E2.151.0")}),-1.0]])]});
            var Q191;
            Q191=makeQuery(id+"F1.opExtrude","SWEPT_FACE",FACE,{"disambiguationData":[OSD([sQuery(id+"F0.wireOp",EDGE,"E2.156.0")])]});
            var Q192;
            Q192=makeQuery(id+"F1.opExtrude","SWEPT_FACE",FACE,{"disambiguationData":[OSD([sQuery(id+"F0.wireOp",EDGE,"E2.64.0")])]});
            var Q193;
            Q193=makeQuery(id+"F1.opExtrude","SWEPT_FACE",FACE,{"disambiguationData":[OSD([sQuery(id+"F0.wireOp",EDGE,"E2.131.0")])]});
            var Q194;
            Q194=makeQuery(id+"F1.opExtrude","SWEPT_FACE",FACE,{"disambiguationData":[OSD([sQuery(id+"F0.wireOp",EDGE,"E4.119.0")])]});
            var Q195;
            Q195=makeQuery(id+"F1.opExtrude","SWEPT_FACE",FACE,{"disambiguationData":[OSD([sQuery(id+"F0.wireOp",EDGE,"E6.8.0")])]});
            var Q196;
            Q196=makeQuery(id+"F1.opExtrude","SWEPT_FACE",FACE,{"disambiguationData":[OSD([sQuery(id+"F0.wireOp",EDGE,"E6.25.0")])]});
            var Q197;
            Q197=makeQuery(id+"F1.opExtrude","SWEPT_FACE",FACE,{"disambiguationData":[OSD([sQuery(id+"F0.wireOp",EDGE,"E4.21.0")])]});
            var Q198;
            Q198=makeQuery(id+"F1.opExtrude","SWEPT_FACE",FACE,{"disambiguationData":[OSD([sQuery(id+"F0.wireOp",EDGE,"E4.22.0")])]});
            var Q199;
            Q199=makeQuery(id+"F1.opExtrude","SWEPT_FACE",FACE,{"disambiguationData":[OSD([sQuery(id+"F0.wireOp",EDGE,"E4.129.0")])]});
            var Q200;
            Q200=makeQuery(id+"F1.opExtrude","SWEPT_FACE",FACE,{"disambiguationData":[OSD([sQuery(id+"F0.wireOp",EDGE,"E6.30.0")])]});
            var Q201;
            Q201=makeQuery(id+"F1.opExtrude","SWEPT_FACE",FACE,{"disambiguationData":[OSD([sQuery(id+"F0.wireOp",EDGE,"E4.23.0")])]});
            var Q202;
            Q202=makeQuery(id+"F1.opExtrude","SWEPT_FACE",FACE,{"disambiguationData":[OSD([sQuery(id+"F0.wireOp",EDGE,"E2.52.0")])]});
            var Q203;
            Q203=makeQuery(id+"F1.opExtrude","SWEPT_FACE",FACE,{"disambiguationData":[OSD([sQuery(id+"F0.wireOp",EDGE,"E2.120.0")])]});
            var Q204;
            Q204=makeQuery(id+"F1.opExtrude","SWEPT_FACE",FACE,{"disambiguationData":[OSD([sQuery(id+"F0.wireOp",EDGE,"E2.28.0")])]});
            var Q205;
            Q205=makeQuery(id+"F0.imprint","IMPRINT",FACE,{"disambiguationData":[TD([[makeQuery(id+"F0.imprint","IMPRINT",EDGE,{"derivedFrom":sQuery(id+"F0.wireOp",EDGE,"E2.63.0")}),-1.0]])]});
            var Q206;
            Q206=makeQuery(id+"F1.opExtrude","SWEPT_FACE",FACE,{"disambiguationData":[OSD([sQuery(id+"F0.wireOp",EDGE,"E4.159.0")])]});
            var Q207;
            Q207=makeQuery(id+"F1.opExtrude","SWEPT_FACE",FACE,{"disambiguationData":[OSD([sQuery(id+"F0.wireOp",EDGE,"E2.63.0")])]});
            var Q208;
            Q208=makeQuery(id+"F1.opExtrude","SWEPT_FACE",FACE,{"disambiguationData":[OSD([sQuery(id+"F0.wireOp",EDGE,"E4.158.0")])]});
            var Q209;
            Q209=makeQuery(id+"F0.imprint","IMPRINT",FACE,{"disambiguationData":[TD([[makeQuery(id+"F0.imprint","IMPRINT",EDGE,{"derivedFrom":sQuery(id+"F0.wireOp",EDGE,"E2.27.0")}),-1.0]])]});
            var Q210;
            Q210=makeQuery(id+"F1.opExtrude","SWEPT_FACE",FACE,{"disambiguationData":[OSD([sQuery(id+"F0.wireOp",EDGE,"E2.123.0")])]});
            var Q211;
            Q211=makeQuery(id+"F1.opExtrude","SWEPT_FACE",FACE,{"disambiguationData":[OSD([sQuery(id+"F0.wireOp",EDGE,"E2.59.0")])]});
            var Q212;
            Q212=makeQuery(id+"F1.opExtrude","SWEPT_FACE",FACE,{"disambiguationData":[OSD([sQuery(id+"F0.wireOp",EDGE,"E2.32.0")])]});
            var Q213;
            Q213=makeQuery(id+"F1.opExtrude","SWEPT_FACE",FACE,{"disambiguationData":[OSD([sQuery(id+"F0.wireOp",EDGE,"E6.38.0")])]});
            var Q214;
            Q214=makeQuery(id+"F1.opExtrude","SWEPT_FACE",FACE,{"disambiguationData":[OSD([sQuery(id+"F0.wireOp",EDGE,"E4.55.0")])]});
            var Q215;
            Q215=makeQuery(id+"F1.opExtrude","SWEPT_FACE",FACE,{"disambiguationData":[OSD([sQuery(id+"F0.wireOp",EDGE,"E2.132.0")])]});
            var Q216;
            Q216=makeQuery(id+"F1.opExtrude","SWEPT_FACE",FACE,{"disambiguationData":[OSD([sQuery(id+"F0.wireOp",EDGE,"E4.121.0")])]});
            var Q217;
            Q217=makeQuery(id+"F1.opExtrude","SWEPT_FACE",FACE,{"disambiguationData":[OSD([sQuery(id+"F0.wireOp",EDGE,"E2.51.0")])]});
            var Q218;
            Q218=makeQuery(id+"F1.opExtrude","SWEPT_FACE",FACE,{"disambiguationData":[OSD([sQuery(id+"F0.wireOp",EDGE,"E6.16.0")])]});
            var Q219;
            Q219=makeQuery(id+"F1.opExtrude","SWEPT_FACE",FACE,{"disambiguationData":[OSD([sQuery(id+"F0.wireOp",EDGE,"E2.151.0")])]});
            var Q220;
            Q220=makeQuery(id+"F1.opExtrude","SWEPT_FACE",FACE,{"disambiguationData":[OSD([sQuery(id+"F0.wireOp",EDGE,"E2.60.0")])]});
            var Q221;
            Q221=makeQuery(id+"F0.imprint","IMPRINT",FACE,{"disambiguationData":[TD([[makeQuery(id+"F0.imprint","IMPRINT",EDGE,{"derivedFrom":sQuery(id+"F0.wireOp",EDGE,"E2.31.0")}),-1.0]])]});
            var Q222;
            Q222=makeQuery(id+"F1.opExtrude","SWEPT_FACE",FACE,{"disambiguationData":[OSD([sQuery(id+"F0.wireOp",EDGE,"E2.135.0")])]});
            var Q223;
            Q223=makeQuery(id+"F1.opExtrude","SWEPT_FACE",FACE,{"disambiguationData":[OSD([sQuery(id+"F0.wireOp",EDGE,"E4.122.0")])]});
            var Q224;
            Q224=makeQuery(id+"F1.opExtrude","SWEPT_FACE",FACE,{"disambiguationData":[OSD([sQuery(id+"F0.wireOp",EDGE,"E4.123.0")])]});
            var Q225;
            Q225=makeQuery(id+"F1.opExtrude","SWEPT_FACE",FACE,{"disambiguationData":[OSD([sQuery(id+"F0.wireOp",EDGE,"E4.61.0")])]});
            var Q226;
            Q226=makeQuery(id+"F1.opExtrude","SWEPT_FACE",FACE,{"disambiguationData":[OSD([sQuery(id+"F0.wireOp",EDGE,"E4.63.0")])]});
            var Q227;
            Q227=makeQuery(id+"F1.opExtrude","SWEPT_FACE",FACE,{"disambiguationData":[OSD([sQuery(id+"F0.wireOp",EDGE,"E2.48.0")])]});
            var Q228;
            Q228=makeQuery(id+"F1.opExtrude","SWEPT_FACE",FACE,{"disambiguationData":[OSD([sQuery(id+"F0.wireOp",EDGE,"E4.130.0")])]});
            var Q229;
            Q229=makeQuery(id+"F1.opExtrude","SWEPT_FACE",FACE,{"disambiguationData":[OSD([sQuery(id+"F0.wireOp",EDGE,"E2.147.0")])]});
            var Q230;
            Q230=makeQuery(id+"F1.opExtrude","SWEPT_FACE",FACE,{"disambiguationData":[OSD([sQuery(id+"F0.wireOp",EDGE,"E6.31.0")])]});
            var Q231;
            Q231=makeQuery(id+"F1.opExtrude","SWEPT_FACE",FACE,{"disambiguationData":[OSD([sQuery(id+"F0.wireOp",EDGE,"E4.25.0")])]});
            var Q232;
            Q232=makeQuery(id+"F1.opExtrude","SWEPT_FACE",FACE,{"disambiguationData":[OSD([sQuery(id+"F0.wireOp",EDGE,"E2.152.0")])]});
            var Q233;
            Q233=makeQuery(id+"F1.opExtrude","SWEPT_FACE",FACE,{"disambiguationData":[OSD([sQuery(id+"F0.wireOp",EDGE,"E2.31.0")])]});
            var Q234;
            Q234=makeQuery(id+"F0.imprint","IMPRINT",FACE,{"disambiguationData":[TD([[makeQuery(id+"F0.imprint","IMPRINT",EDGE,{"derivedFrom":sQuery(id+"F0.wireOp",EDGE,"E2.59.0")}),-1.0]])]});
            var Q235;
            Q235=makeQuery(id+"F1.opExtrude","SWEPT_FACE",FACE,{"disambiguationData":[OSD([sQuery(id+"F0.wireOp",EDGE,"E6.37.0")])]});
            var Q236;
            Q236=makeQuery(id+"F0.imprint","IMPRINT",FACE,{"disambiguationData":[TD([[makeQuery(id+"F0.imprint","IMPRINT",EDGE,{"derivedFrom":sQuery(id+"F0.wireOp",EDGE,"E2.35.0")}),-1.0]])]});
            var Q237;
            Q237=makeQuery(id+"F0.imprint","IMPRINT",FACE,{"disambiguationData":[TD([[makeQuery(id+"F0.imprint","IMPRINT",EDGE,{"derivedFrom":sQuery(id+"F0.wireOp",EDGE,"E2.123.0")}),-1.0]])]});
            var Q238;
            Q238=makeQuery(id+"F1.opExtrude","SWEPT_FACE",FACE,{"disambiguationData":[OSD([sQuery(id+"F0.wireOp",EDGE,"E4.157.0")])]});
            var Q239;
            Q239=makeQuery(id+"F1.opExtrude","SWEPT_FACE",FACE,{"disambiguationData":[OSD([sQuery(id+"F0.wireOp",EDGE,"E4.54.0")])]});
            var Q240;
            Q240=makeQuery(id+"F1.opExtrude","SWEPT_FACE",FACE,{"disambiguationData":[OSD([sQuery(id+"F0.wireOp",EDGE,"E6.9.0")])]});
            var Q241;
            Q241=makeQuery(id+"F1.opExtrude","SWEPT_FACE",FACE,{"disambiguationData":[OSD([sQuery(id+"F0.wireOp",EDGE,"E6.10.0")])]});
            var Q242;
            Q242=makeQuery(id+"F1.opExtrude","SWEPT_FACE",FACE,{"disambiguationData":[OSD([sQuery(id+"F0.wireOp",EDGE,"E2.136.0")])]});
            var Q243;
            Q243=makeQuery(id+"F1.opExtrude","SWEPT_FACE",FACE,{"disambiguationData":[OSD([sQuery(id+"F0.wireOp",EDGE,"E4.62.0")])]});
            var Q244;
            Q244=makeQuery(id+"F1.opExtrude","SWEPT_FACE",FACE,{"disambiguationData":[OSD([sQuery(id+"F0.wireOp",EDGE,"E2.47.0")])]});
            var Q245;
            Q245=makeQuery(id+"F1.opExtrude","SWEPT_FACE",FACE,{"disambiguationData":[OSD([sQuery(id+"F0.wireOp",EDGE,"E6.15.0")])]});
            var Q246;
            Q246=makeQuery(id+"F1.opExtrude","SWEPT_FACE",FACE,{"disambiguationData":[OSD([sQuery(id+"F0.wireOp",EDGE,"E2.148.0")])]});
            var Q247;
            Q247=makeQuery(id+"F1.opExtrude","SWEPT_FACE",FACE,{"disambiguationData":[OSD([sQuery(id+"F0.wireOp",EDGE,"E6.32.0")])]});
            var Q248;
            Q248=makeQuery(id+"F1.opExtrude","SWEPT_FACE",FACE,{"disambiguationData":[OSD([sQuery(id+"F0.wireOp",EDGE,"E4.131.0")])]});
            var Q249;
            Q249=makeQuery(id+"F1.opExtrude","SWEPT_FACE",FACE,{"disambiguationData":[OSD([sQuery(id+"F0.wireOp",EDGE,"E6.33.0")])]});
            var Q250;
            Q250=makeQuery(id+"F1.opExtrude","SWEPT_FACE",FACE,{"disambiguationData":[OSD([sQuery(id+"F0.wireOp",EDGE,"E4.26.0")])]});
            var Q251;
            Q251=makeQuery(id+"F1.opExtrude","SWEPT_FACE",FACE,{"disambiguationData":[OSD([sQuery(id+"F0.wireOp",EDGE,"E4.27.0")])]});
            var Q252;
            Q252=makeQuery(id+"F1.opExtrude","SWEPT_FACE",FACE,{"disambiguationData":[OSD([sQuery(id+"F0.wireOp",EDGE,"E2.35.0")])]});
            var Q253;
            Q253=makeQuery(id+"F1.opExtrude","SWEPT_FACE",FACE,{"disambiguationData":[OSD([sQuery(id+"F0.wireOp",EDGE,"E2.36.0")])]});
            var Q254;
            Q254=makeQuery(id+"F1.opExtrude","SWEPT_FACE",FACE,{"disambiguationData":[OSD([sQuery(id+"F0.wireOp",EDGE,"E2.139.0")])]});
            var Q255;
            Q255=makeQuery(id+"F1.opExtrude","SWEPT_FACE",FACE,{"disambiguationData":[OSD([sQuery(id+"F0.wireOp",EDGE,"E2.44.0")])]});
            var Q256;
            Q256=makeQuery(id+"F1.opExtrude","SWEPT_FACE",FACE,{"disambiguationData":[OSD([sQuery(id+"F0.wireOp",EDGE,"E6.12.0")])]});
            var Q257;
            Q257=makeQuery(id+"F1.opExtrude","SWEPT_FACE",FACE,{"disambiguationData":[OSD([sQuery(id+"F0.wireOp",EDGE,"E2.143.0")])]});
            var Q258;
            Q258=makeQuery(id+"F1.opExtrude","SWEPT_FACE",FACE,{"disambiguationData":[OSD([sQuery(id+"F0.wireOp",EDGE,"E4.150.0")])]});
            var Q259;
            Q259=makeQuery(id+"F1.opExtrude","SWEPT_FACE",FACE,{"disambiguationData":[OSD([sQuery(id+"F0.wireOp",EDGE,"E6.14.0")])]});
            var Q260;
            Q260=makeQuery(id+"F1.opExtrude","SWEPT_FACE",FACE,{"disambiguationData":[OSD([sQuery(id+"F0.wireOp",EDGE,"E4.154.0")])]});
            var Q261;
            Q261=makeQuery(id+"F1.opExtrude","SWEPT_FACE",FACE,{"disambiguationData":[OSD([sQuery(id+"F0.wireOp",EDGE,"E4.155.0")])]});
            var Q262;
            Q262=makeQuery(id+"F0.imprint","IMPRINT",FACE,{"disambiguationData":[TD([[makeQuery(id+"F0.imprint","IMPRINT",EDGE,{"derivedFrom":sQuery(id+"F0.wireOp",EDGE,"E2.127.0")}),-1.0]])]});
            var Q263;
            Q263=makeQuery(id+"F0.imprint","IMPRINT",FACE,{"disambiguationData":[TD([[makeQuery(id+"F0.imprint","IMPRINT",EDGE,{"derivedFrom":sQuery(id+"F0.wireOp",EDGE,"E2.147.0")}),-1.0]])]});
            var Q264;
            Q264=makeQuery(id+"F0.imprint","IMPRINT",FACE,{"disambiguationData":[TD([[makeQuery(id+"F0.imprint","IMPRINT",EDGE,{"derivedFrom":sQuery(id+"F0.wireOp",EDGE,"E2.55.0")}),-1.0]])]});
            var Q265;
            Q265=makeQuery(id+"F1.opExtrude","SWEPT_FACE",FACE,{"disambiguationData":[OSD([sQuery(id+"F0.wireOp",EDGE,"E6.36.0")])]});
            var Q266;
            Q266=makeQuery(id+"F1.opExtrude","SWEPT_FACE",FACE,{"disambiguationData":[OSD([sQuery(id+"F0.wireOp",EDGE,"E4.30.0")])]});
            var Q267;
            Q267=makeQuery(id+"F0.imprint","IMPRINT",FACE,{"disambiguationData":[TD([[makeQuery(id+"F0.imprint","IMPRINT",EDGE,{"derivedFrom":sQuery(id+"F0.wireOp",EDGE,"E2.131.0")}),-1.0]])]});
            var Q268;
            Q268=makeQuery(id+"F1.opExtrude","SWEPT_FACE",FACE,{"disambiguationData":[OSD([sQuery(id+"F0.wireOp",EDGE,"E4.29.0")])]});
            var Q269;
            Q269=makeQuery(id+"F1.opExtrude","SWEPT_FACE",FACE,{"disambiguationData":[OSD([sQuery(id+"F0.wireOp",EDGE,"E2.39.0")])]});
            var Q270;
            Q270=makeQuery(id+"F1.opExtrude","SWEPT_FACE",FACE,{"disambiguationData":[OSD([sQuery(id+"F0.wireOp",EDGE,"E2.43.0")])]});
            var Q271;
            Q271=makeQuery(id+"F1.opExtrude","SWEPT_FACE",FACE,{"disambiguationData":[OSD([sQuery(id+"F0.wireOp",EDGE,"E2.140.0")])]});
            var Q272;
            Q272=makeQuery(id+"F1.opExtrude","SWEPT_FACE",FACE,{"disambiguationData":[OSD([sQuery(id+"F0.wireOp",EDGE,"E6.13.0")])]});
            var Q273;
            Q273=makeQuery(id+"F1.opExtrude","SWEPT_FACE",FACE,{"disambiguationData":[OSD([sQuery(id+"F0.wireOp",EDGE,"E2.144.0")])]});
            var Q274;
            Q274=makeQuery(id+"F1.opExtrude","SWEPT_FACE",FACE,{"disambiguationData":[OSD([sQuery(id+"F0.wireOp",EDGE,"E6.34.0")])]});
            var Q275;
            Q275=makeQuery(id+"F1.opExtrude","SWEPT_FACE",FACE,{"disambiguationData":[OSD([sQuery(id+"F0.wireOp",EDGE,"E4.53.0")])]});
            var Q276;
            Q276=makeQuery(id+"F1.opExtrude","SWEPT_FACE",FACE,{"disambiguationData":[OSD([sQuery(id+"F0.wireOp",EDGE,"E4.31.0")])]});
            var Q277;
            Q277=makeQuery(id+"F1.opExtrude","SWEPT_FACE",FACE,{"disambiguationData":[OSD([sQuery(id+"F0.wireOp",EDGE,"E6.35.0")])]});
            var Q278;
            Q278=makeQuery(id+"F1.opExtrude","SWEPT_FACE",FACE,{"disambiguationData":[OSD([sQuery(id+"F0.wireOp",EDGE,"E4.142.0")])]});
            var Q279;
            Q279=makeQuery(id+"F1.opExtrude","SWEPT_FACE",FACE,{"disambiguationData":[OSD([sQuery(id+"F0.wireOp",EDGE,"E2.40.0")])]});
            var Q280;
            Q280=makeQuery(id+"F1.opExtrude","SWEPT_FACE",FACE,{"disambiguationData":[OSD([sQuery(id+"F0.wireOp",EDGE,"E4.145.0")])]});
            var Q281;
            Q281=makeQuery(id+"F1.opExtrude","SWEPT_FACE",FACE,{"disambiguationData":[OSD([sQuery(id+"F0.wireOp",EDGE,"E6.11.0")])]});
            var Q282;
            Q282=makeQuery(id+"F1.opExtrude","SWEPT_FACE",FACE,{"disambiguationData":[OSD([sQuery(id+"F0.wireOp",EDGE,"E4.146.0")])]});
            var Q283;
            Q283=makeQuery(id+"F1.opExtrude","SWEPT_FACE",FACE,{"disambiguationData":[OSD([sQuery(id+"F0.wireOp",EDGE,"E4.149.0")])]});
            var Q284;
            Q284=makeQuery(id+"F1.opExtrude","SWEPT_FACE",FACE,{"disambiguationData":[OSD([sQuery(id+"F0.wireOp",EDGE,"E4.153.0")])]});
            var Q285;
            Q285=makeQuery(id+"F0.imprint","IMPRINT",FACE,{"disambiguationData":[TD([[makeQuery(id+"F0.imprint","IMPRINT",EDGE,{"derivedFrom":sQuery(id+"F0.wireOp",EDGE,"E2.143.0")}),-1.0]])]});
            var Q286;
            Q286=makeQuery(id+"F0.imprint","IMPRINT",FACE,{"disambiguationData":[TD([[makeQuery(id+"F0.imprint","IMPRINT",EDGE,{"derivedFrom":sQuery(id+"F0.wireOp",EDGE,"E2.39.0")}),-1.0]])]});
            var Q287;
            Q287=makeQuery(id+"F1.opExtrude","SWEPT_FACE",FACE,{"disambiguationData":[OSD([sQuery(id+"F0.wireOp",EDGE,"E4.33.0")])]});
            var Q288;
            Q288=makeQuery(id+"F1.opExtrude","SWEPT_FACE",FACE,{"disambiguationData":[OSD([sQuery(id+"F0.wireOp",EDGE,"E4.35.0")])]});
            var Q289;
            Q289=makeQuery(id+"F1.opExtrude","SWEPT_FACE",FACE,{"disambiguationData":[OSD([sQuery(id+"F0.wireOp",EDGE,"E4.37.0")])]});
            var Q290;
            Q290=makeQuery(id+"F1.opExtrude","SWEPT_FACE",FACE,{"disambiguationData":[OSD([sQuery(id+"F0.wireOp",EDGE,"E4.143.0")])]});
            var Q291;
            Q291=makeQuery(id+"F1.opExtrude","SWEPT_FACE",FACE,{"disambiguationData":[OSD([sQuery(id+"F0.wireOp",EDGE,"E4.147.0")])]});
            var Q292;
            Q292=makeQuery(id+"F1.opExtrude","SWEPT_FACE",FACE,{"disambiguationData":[OSD([sQuery(id+"F0.wireOp",EDGE,"E4.151.0")])]});
            var Q293;
            Q293=makeQuery(id+"F0.imprint","IMPRINT",FACE,{"disambiguationData":[TD([[makeQuery(id+"F0.imprint","IMPRINT",EDGE,{"derivedFrom":sQuery(id+"F0.wireOp",EDGE,"E2.135.0")}),-1.0]])]});
            var Q294;
            Q294=makeQuery(id+"F0.imprint","IMPRINT",FACE,{"disambiguationData":[TD([[makeQuery(id+"F0.imprint","IMPRINT",EDGE,{"derivedFrom":sQuery(id+"F0.wireOp",EDGE,"E2.51.0")}),-1.0]])]});
            var Q295;
            Q295=makeQuery(id+"F1.opExtrude","SWEPT_FACE",FACE,{"disambiguationData":[OSD([sQuery(id+"F0.wireOp",EDGE,"E4.34.0")])]});
            var Q296;
            Q296=makeQuery(id+"F1.opExtrude","SWEPT_FACE",FACE,{"disambiguationData":[OSD([sQuery(id+"F0.wireOp",EDGE,"E4.38.0")])]});
            var Q297;
            Q297=makeQuery(id+"F1.opExtrude","SWEPT_FACE",FACE,{"disambiguationData":[OSD([sQuery(id+"F0.wireOp",EDGE,"E4.39.0")])]});
            var Q298;
            Q298=makeQuery(id+"F1.opExtrude","SWEPT_FACE",FACE,{"disambiguationData":[OSD([sQuery(id+"F0.wireOp",EDGE,"E4.41.0")])]});
            var Q299;
            Q299=makeQuery(id+"F0.imprint","IMPRINT",FACE,{"disambiguationData":[TD([[makeQuery(id+"F0.imprint","IMPRINT",EDGE,{"derivedFrom":sQuery(id+"F0.wireOp",EDGE,"E2.139.0")}),-1.0]])]});
            var Q300;
            Q300=makeQuery(id+"F1.opExtrude","SWEPT_FACE",FACE,{"disambiguationData":[OSD([sQuery(id+"F0.wireOp",EDGE,"E4.51.0")])]});
            var Q301;
            Q301=makeQuery(id+"F1.opExtrude","SWEPT_FACE",FACE,{"disambiguationData":[OSD([sQuery(id+"F0.wireOp",EDGE,"E4.135.0")])]});
            var Q302;
            Q302=makeQuery(id+"F1.opExtrude","SWEPT_FACE",FACE,{"disambiguationData":[OSD([sQuery(id+"F0.wireOp",EDGE,"E4.133.0")])]});
            var Q303;
            Q303=makeQuery(id+"F0.imprint","IMPRINT",FACE,{"disambiguationData":[TD([[makeQuery(id+"F0.imprint","IMPRINT",EDGE,{"derivedFrom":sQuery(id+"F0.wireOp",EDGE,"E2.47.0")}),-1.0]])]});
            var Q304;
            Q304=makeQuery(id+"F1.opExtrude","SWEPT_FACE",FACE,{"disambiguationData":[OSD([sQuery(id+"F0.wireOp",EDGE,"E4.50.0")])]});
            var Q305;
            Q305=makeQuery(id+"F1.opExtrude","SWEPT_FACE",FACE,{"disambiguationData":[OSD([sQuery(id+"F0.wireOp",EDGE,"E4.49.0")])]});
            var Q306;
            Q306=makeQuery(id+"F1.opExtrude","SWEPT_FACE",FACE,{"disambiguationData":[OSD([sQuery(id+"F0.wireOp",EDGE,"E4.134.0")])]});
            var Q307;
            Q307=makeQuery(id+"F0.imprint","IMPRINT",FACE,{"disambiguationData":[TD([[makeQuery(id+"F0.imprint","IMPRINT",EDGE,{"derivedFrom":sQuery(id+"F0.wireOp",EDGE,"E2.43.0")}),-1.0]])]});
            var Q308;
            Q308=makeQuery(id+"F1.opExtrude","SWEPT_FACE",FACE,{"disambiguationData":[OSD([sQuery(id+"F0.wireOp",EDGE,"E4.47.0")])]});
            var Q309;
            Q309=makeQuery(id+"F1.opExtrude","SWEPT_FACE",FACE,{"disambiguationData":[OSD([sQuery(id+"F0.wireOp",EDGE,"E4.138.0")])]});
            var Q310;
            Q310=makeQuery(id+"F1.opExtrude","SWEPT_FACE",FACE,{"disambiguationData":[OSD([sQuery(id+"F0.wireOp",EDGE,"E4.137.0")])]});
            var Q311;
            Q311=makeQuery(id+"F1.opExtrude","SWEPT_FACE",FACE,{"disambiguationData":[OSD([sQuery(id+"F0.wireOp",EDGE,"E4.46.0")])]});
            var Q312;
            Q312=makeQuery(id+"F1.opExtrude","SWEPT_FACE",FACE,{"disambiguationData":[OSD([sQuery(id+"F0.wireOp",EDGE,"E4.139.0")])]});
            var Q313;
            Q313=makeQuery(id+"F1.opExtrude","SWEPT_FACE",FACE,{"disambiguationData":[OSD([sQuery(id+"F0.wireOp",EDGE,"E4.45.0")])]});
            var Q314;
            Q314=makeQuery(id+"F1.opExtrude","SWEPT_FACE",FACE,{"disambiguationData":[OSD([sQuery(id+"F0.wireOp",EDGE,"E4.141.0")])]});
            var Q315;
            Q315=makeQuery(id+"F1.opExtrude","SWEPT_FACE",FACE,{"disambiguationData":[OSD([sQuery(id+"F0.wireOp",EDGE,"E4.43.0")])]});
            var Q316;
            Q316=makeQuery(id+"F1.opExtrude","SWEPT_FACE",FACE,{"disambiguationData":[OSD([sQuery(id+"F0.wireOp",EDGE,"E4.42.0")])]});
            extrude(context, id + "F2", {"entities" : qUnion([Q0, Q1, Q2, Q3, Q4, Q5, Q6, Q7, Q8, Q9, Q10, Q11, Q12, Q13, Q14, Q15, Q16, Q17, Q18, Q19, Q20, Q21, Q22, Q23, Q24, Q25, Q26, Q27, Q28, Q29, Q30, Q31, Q32, Q33, Q34, Q35, Q36, Q37, Q38, Q39, Q40, Q41, Q42, Q43, Q44, Q45, Q46, Q47, Q48, Q49, Q50, Q51, Q52, Q53, Q54, Q55, Q56, Q57, Q58, Q59, Q60, Q61, Q62, Q63, Q64, Q65, Q66, Q67, Q68, Q69, Q70, Q71, Q72, Q73, Q74, Q75, Q76, Q77, Q78, Q79, Q80, Q81, Q82, Q83, Q84, Q85, Q86, Q87, Q88, Q89, Q90, Q91, Q92, Q93, Q94, Q95, Q96, Q97, Q98, Q99, Q100, Q101, Q102, Q103, Q104, Q105, Q106, Q107, Q108, Q109, Q110, Q111, Q112, Q113, Q114, Q115, Q116, Q117, Q118, Q119, Q120, Q121, Q122, Q123, Q124, Q125, Q126, Q127, Q128, Q129, Q130, Q131, Q132, Q133, Q134, Q135, Q136, Q137, Q138, Q139, Q140, Q141, Q142, Q143, Q144, Q145, Q146, Q147, Q148, Q149, Q150, Q151, Q152, Q153, Q154, Q155, Q156, Q157, Q158, Q159, Q160, Q161, Q162, Q163, Q164, Q165, Q166, Q167, Q168, Q169, Q170, Q171, Q172, Q173, Q174, Q175, Q176, Q177, Q178, Q179, Q180, Q181, Q182, Q183, Q184, Q185, Q186, Q187, Q188, Q189, Q190, Q191, Q192, Q193, Q194, Q195, Q196, Q197, Q198, Q199, Q200, Q201, Q202, Q203, Q204, Q205, Q206, Q207, Q208, Q209, Q210, Q211, Q212, Q213, Q214, Q215, Q216, Q217, Q218, Q219, Q220, Q221, Q222, Q223, Q224, Q225, Q226, Q227, Q228, Q229, Q230, Q231, Q232, Q233, Q234, Q235, Q236, Q237, Q238, Q239, Q240, Q241, Q242, Q243, Q244, Q245, Q246, Q247, Q248, Q249, Q250, Q251, Q252, Q253, Q254, Q255, Q256, Q257, Q258, Q259, Q260, Q261, Q262, Q263, Q264, Q265, Q266, Q267, Q268, Q269, Q270, Q271, Q272, Q273, Q274, Q275, Q276, Q277, Q278, Q279, Q280, Q281, Q282, Q283, Q284, Q285, Q286, Q287, Q288, Q289, Q290, Q291, Q292, Q293, Q294, Q295, Q296, Q297, Q298, Q299, Q300, Q301, Q302, Q303, Q304, Q305, Q306, Q307, Q308, Q309, Q310, Q311, Q312, Q313, Q314, Q315, Q316]), "operationType" : NewBodyOperationType.ADD, "oppositeDirection" : true, "depth" : 25.4 * mm});
        }
        {
            var Q0;
            Q0=makeQuery(id+"F2.opExtrude","SWEPT_FACE",FACE,{"disambiguationData":[OSD([sQuery(id+"F0.wireOp",EDGE,"E3")])]});
            cPlane(context, id + "F3", {"entities" : qUnion([Q0]), "cplaneType" : CPlaneType.OFFSET, "offset" : 0 * mm, "width" : 152.4 * mm, "height" : 152.4 * mm});
        }
        {
            var Q0;
            Q0=qCreatedBy(id+"F3.planeOp",FACE);
            var sketch = newSketch(context, id + "F4", { "sketchPlane" : qUnion([Q0])});
            skLineSegment(sketch, "E8", {"start": v(0, -3.55) * mm, "end": v(50.8, -3.55) * mm, "construction": true});
            skPoint(sketch, "E9.center", {"position": v(50.8, -3.55) * mm});
            skLineSegment(sketch, "E10", {"start": v(0, -3.55) * mm, "end": v(0.5, 3.52) * mm});
            skLineSegment(sketch, "E11.5.0", {"start": v(11.88, -36.2) * mm, "end": v(7.72, -30.47) * mm});
            skLineSegment(sketch, "E11.10.0", {"start": v(41.98, -53.57) * mm, "end": v(35.1, -51.86) * mm});
            skLineSegment(sketch, "E11.20.0", {"start": v(98.54, -20.92) * mm, "end": v(95.65, -27.4) * mm});
            skLineSegment(sketch, "E11.25.0", {"start": v(98.54, 13.83) * mm, "end": v(100.49, 7.02) * mm});
            skLineSegment(sketch, "E11.30.0", {"start": v(76.2, 40.45) * mm, "end": v(82.08, 36.48) * mm});
            skLineSegment(sketch, "E11.35.0", {"start": v(41.98, 46.48) * mm, "end": v(49.03, 47.22) * mm});
            skLineSegment(sketch, "E11.40.0", {"start": v(11.88, 29.1) * mm, "end": v(16.8, 34.2) * mm});
            skLineSegment(sketch, "E12", {"start": v(12.7, -3.55) * mm, "end": v(13.07, 1.76) * mm});
            skLineSegment(sketch, "E13.1.0", {"start": v(13.07, -8.85) * mm, "end": v(12.7, -3.55) * mm});
            skLineSegment(sketch, "E13.2.0", {"start": v(14.18, -14.05) * mm, "end": v(13.07, -8.85) * mm});
            skLineSegment(sketch, "E13.3.0", {"start": v(16, -19.04) * mm, "end": v(14.18, -14.05) * mm});
            skLineSegment(sketch, "E13.4.0", {"start": v(18.49, -23.74) * mm, "end": v(16, -19.04) * mm});
            skLineSegment(sketch, "E13.5.0", {"start": v(21.61, -28.04) * mm, "end": v(18.49, -23.74) * mm});
            skLineSegment(sketch, "E13.6.0", {"start": v(25.3, -31.86) * mm, "end": v(21.61, -28.04) * mm});
            skLineSegment(sketch, "E13.7.0", {"start": v(29.5, -35.13) * mm, "end": v(25.3, -31.86) * mm});
            skLineSegment(sketch, "E13.8.0", {"start": v(34.1, -37.8) * mm, "end": v(29.5, -35.13) * mm});
            skLineSegment(sketch, "E13.9.0", {"start": v(39.03, -39.78) * mm, "end": v(34.1, -37.8) * mm});
            skLineSegment(sketch, "E13.10.0", {"start": v(44.18, -41.07) * mm, "end": v(39.03, -39.78) * mm});
            skLineSegment(sketch, "E13.11.0", {"start": v(49.47, -41.62) * mm, "end": v(44.18, -41.07) * mm});
            skLineSegment(sketch, "E13.12.0", {"start": v(54.78, -41.44) * mm, "end": v(49.47, -41.62) * mm});
            skLineSegment(sketch, "E13.13.0", {"start": v(60.02, -40.51) * mm, "end": v(54.78, -41.44) * mm});
            skLineSegment(sketch, "E13.14.0", {"start": v(65.07, -38.87) * mm, "end": v(60.02, -40.51) * mm});
            skLineSegment(sketch, "E14.1.15.0", {"start": v(69.85, -36.54) * mm, "end": v(65.07, -38.87) * mm});
            skLineSegment(sketch, "E14.1.16.0", {"start": v(74.26, -33.57) * mm, "end": v(69.85, -36.54) * mm});
            skLineSegment(sketch, "E14.1.17.0", {"start": v(78.2, -30.01) * mm, "end": v(74.26, -33.57) * mm});
            skLineSegment(sketch, "E14.1.18.0", {"start": v(81.62, -25.94) * mm, "end": v(78.2, -30.01) * mm});
            skLineSegment(sketch, "E14.1.19.0", {"start": v(84.44, -21.43) * mm, "end": v(81.62, -25.94) * mm});
            skLineSegment(sketch, "E14.1.20.0", {"start": v(86.6, -16.58) * mm, "end": v(84.44, -21.43) * mm});
            skLineSegment(sketch, "E14.1.21.0", {"start": v(88.07, -11.47) * mm, "end": v(86.6, -16.58) * mm});
            skLineSegment(sketch, "E14.1.22.0", {"start": v(88.8, -6.2) * mm, "end": v(88.07, -11.47) * mm});
            skLineSegment(sketch, "E14.1.23.0", {"start": v(88.8, -0.89) * mm, "end": v(88.8, -6.2) * mm});
            skLineSegment(sketch, "E14.1.24.0", {"start": v(88.07, 4.38) * mm, "end": v(88.8, -0.89) * mm});
            skLineSegment(sketch, "E14.1.25.0", {"start": v(86.6, 9.48) * mm, "end": v(88.07, 4.38) * mm});
            skLineSegment(sketch, "E14.1.26.0", {"start": v(84.44, 14.34) * mm, "end": v(86.6, 9.48) * mm});
            skLineSegment(sketch, "E14.1.27.0", {"start": v(81.62, 18.85) * mm, "end": v(84.44, 14.34) * mm});
            skLineSegment(sketch, "E14.1.28.0", {"start": v(78.2, 22.92) * mm, "end": v(81.62, 18.85) * mm});
            skLineSegment(sketch, "E14.1.29.0", {"start": v(74.26, 26.48) * mm, "end": v(78.2, 22.92) * mm});
            skLineSegment(sketch, "E15.1.30.0", {"start": v(69.85, 29.45) * mm, "end": v(74.26, 26.48) * mm});
            skLineSegment(sketch, "E15.1.31.0", {"start": v(65.07, 31.78) * mm, "end": v(69.85, 29.45) * mm});
            skLineSegment(sketch, "E15.1.32.0", {"start": v(60.02, 33.42) * mm, "end": v(65.07, 31.78) * mm});
            skLineSegment(sketch, "E15.1.33.0", {"start": v(54.78, 34.34) * mm, "end": v(60.02, 33.42) * mm});
            skLineSegment(sketch, "E15.1.34.0", {"start": v(49.47, 34.53) * mm, "end": v(54.78, 34.34) * mm});
            skLineSegment(sketch, "E15.1.35.0", {"start": v(44.18, 33.97) * mm, "end": v(49.47, 34.53) * mm});
            skLineSegment(sketch, "E15.1.36.0", {"start": v(39.03, 32.69) * mm, "end": v(44.18, 33.97) * mm});
            skLineSegment(sketch, "E15.1.37.0", {"start": v(34.1, 30.7) * mm, "end": v(39.03, 32.69) * mm});
            skLineSegment(sketch, "E15.1.38.0", {"start": v(29.5, 28.04) * mm, "end": v(34.1, 30.7) * mm});
            skLineSegment(sketch, "E15.1.39.0", {"start": v(25.3, 24.77) * mm, "end": v(29.5, 28.04) * mm});
            skLineSegment(sketch, "E15.1.40.0", {"start": v(21.61, 20.94) * mm, "end": v(25.3, 24.77) * mm});
            skLineSegment(sketch, "E15.1.41.0", {"start": v(18.49, 16.64) * mm, "end": v(21.61, 20.94) * mm});
            skLineSegment(sketch, "E15.1.42.0", {"start": v(16, 11.95) * mm, "end": v(18.49, 16.64) * mm});
            skLineSegment(sketch, "E15.1.43.0", {"start": v(14.18, 6.96) * mm, "end": v(16, 11.95) * mm});
            skLineSegment(sketch, "E15.1.44.0", {"start": v(13.07, 1.76) * mm, "end": v(14.18, 6.96) * mm});
            skLineSegment(sketch, "E16", {"start": v(0.5, 3.52) * mm, "end": v(14.18, 6.96) * mm});
            skLineSegment(sketch, "E17", {"start": v(18.49, 16.64) * mm, "end": v(11.88, 29.1) * mm});
            skLineSegment(sketch, "E18", {"start": v(16.8, 34.2) * mm, "end": v(29.5, 28.04) * mm});
            skLineSegment(sketch, "E19", {"start": v(0, -3.55) * mm, "end": v(13.07, -8.85) * mm});
            skLineSegment(sketch, "E20", {"start": v(39.03, 32.69) * mm, "end": v(41.98, 46.48) * mm});
            skLineSegment(sketch, "E21", {"start": v(49.03, 47.22) * mm, "end": v(54.78, 34.34) * mm});
            skLineSegment(sketch, "E22", {"start": v(65.07, 31.78) * mm, "end": v(76.2, 40.45) * mm});
            skLineSegment(sketch, "E23", {"start": v(82.08, 36.48) * mm, "end": v(78.2, 22.92) * mm});
            skLineSegment(sketch, "E24", {"start": v(84.44, 14.34) * mm, "end": v(98.54, 13.83) * mm});
            skLineSegment(sketch, "E25", {"start": v(100.49, 7.02) * mm, "end": v(88.8, -0.89) * mm});
            skLineSegment(sketch, "E26", {"start": v(88.07, -11.47) * mm, "end": v(98.54, -20.92) * mm});
            skLineSegment(sketch, "E27", {"start": v(95.65, -27.4) * mm, "end": v(81.62, -25.94) * mm});
            skLineSegment(sketch, "E28", {"start": v(74.26, -33.57) * mm, "end": v(76.2, -47.54) * mm});
            skLineSegment(sketch, "E29", {"start": v(76.2, -47.54) * mm, "end": v(69.83, -50.65) * mm});
            skLineSegment(sketch, "E30", {"start": v(69.83, -50.65) * mm, "end": v(60.02, -40.51) * mm});
            skLineSegment(sketch, "E31", {"start": v(49.47, -41.62) * mm, "end": v(41.98, -53.57) * mm});
            skLineSegment(sketch, "E32", {"start": v(35.1, -51.86) * mm, "end": v(34.1, -37.8) * mm});
            skLineSegment(sketch, "E33", {"start": v(25.3, -31.86) * mm, "end": v(11.88, -36.2) * mm});
            skLineSegment(sketch, "E34", {"start": v(7.72, -30.47) * mm, "end": v(16, -19.04) * mm});
            skSolve(sketch);
        }
        {
            var Q0;
            Q0 = qSketchRegion(id + "F4", true);
            var Q1;
            Q1=makeQuery(id+"F4.imprint","IMPRINT",FACE,{"disambiguationData":[TD([[makeQuery(id+"F4.imprint","IMPRINT",EDGE,{"derivedFrom":sQuery(id+"F4.wireOp",EDGE,"E12")}),-1.0]])]});
            extrude(context, id + "F5", {"entities" : qUnion([Q0, Q1]), "oppositeDirection" : true, "depth" : 50.8 * mm, "hasDraft" : true, "draftAngle" : 8 * degree, "draftPullDirection" : true});
        }
        {
            var Q0;
            Q0=makeQuery(id+"F5.opExtrude","CAP_FACE",FACE,{"disambiguationData":[OSD([sQuery(id+"F4.wireOp",EDGE,"E10"),sQuery(id+"F4.wireOp",EDGE,"E11.5.0"),sQuery(id+"F4.wireOp",EDGE,"E11.10.0"),sQuery(id+"F4.wireOp",EDGE,"E11.20.0"),sQuery(id+"F4.wireOp",EDGE,"E11.25.0"),sQuery(id+"F4.wireOp",EDGE,"E11.30.0"),sQuery(id+"F4.wireOp",EDGE,"E11.35.0"),sQuery(id+"F4.wireOp",EDGE,"E11.40.0"),sQuery(id+"F4.wireOp",EDGE,"E13.2.0"),sQuery(id+"F4.wireOp",EDGE,"E13.3.0"),sQuery(id+"F4.wireOp",EDGE,"E13.7.0"),sQuery(id+"F4.wireOp",EDGE,"E13.8.0"),sQuery(id+"F4.wireOp",EDGE,"E13.12.0"),sQuery(id+"F4.wireOp",EDGE,"E13.13.0"),sQuery(id+"F4.wireOp",EDGE,"E14.1.17.0"),sQuery(id+"F4.wireOp",EDGE,"E14.1.18.0"),sQuery(id+"F4.wireOp",EDGE,"E14.1.22.0"),sQuery(id+"F4.wireOp",EDGE,"E14.1.23.0"),sQuery(id+"F4.wireOp",EDGE,"E14.1.27.0"),sQuery(id+"F4.wireOp",EDGE,"E14.1.28.0"),sQuery(id+"F4.wireOp",EDGE,"E15.1.32.0"),sQuery(id+"F4.wireOp",EDGE,"E15.1.33.0"),sQuery(id+"F4.wireOp",EDGE,"E15.1.37.0"),sQuery(id+"F4.wireOp",EDGE,"E15.1.38.0"),sQuery(id+"F4.wireOp",EDGE,"E15.1.42.0"),sQuery(id+"F4.wireOp",EDGE,"E15.1.43.0"),sQuery(id+"F4.wireOp",EDGE,"E16"),sQuery(id+"F4.wireOp",EDGE,"E17"),sQuery(id+"F4.wireOp",EDGE,"E18"),sQuery(id+"F4.wireOp",EDGE,"E19"),sQuery(id+"F4.wireOp",EDGE,"E20"),sQuery(id+"F4.wireOp",EDGE,"E21"),sQuery(id+"F4.wireOp",EDGE,"E22"),sQuery(id+"F4.wireOp",EDGE,"E23"),sQuery(id+"F4.wireOp",EDGE,"E24"),sQuery(id+"F4.wireOp",EDGE,"E25"),sQuery(id+"F4.wireOp",EDGE,"E26"),sQuery(id+"F4.wireOp",EDGE,"E27"),sQuery(id+"F4.wireOp",EDGE,"E28"),sQuery(id+"F4.wireOp",EDGE,"E29"),sQuery(id+"F4.wireOp",EDGE,"E30"),sQuery(id+"F4.wireOp",EDGE,"E31"),sQuery(id+"F4.wireOp",EDGE,"E32"),sQuery(id+"F4.wireOp",EDGE,"E33"),sQuery(id+"F4.wireOp",EDGE,"E34")])],"isStart":true});
            var sketch = newSketch(context, id + "F6", { "sketchPlane" : qUnion([Q0])});
            skCircle(sketch, "E35", {"center": v(50.8, -3.55) * mm, "radius": 12.7 * mm});
            skSolve(sketch);
        }
        {
            var Q0;
            Q0 = qSketchRegion(id + "F6", true);
            var Q1;
            Q1=makeQuery(id+"F5.opExtrude","CAP_FACE",FACE,{"disambiguationData":[OSD([sQuery(id+"F4.wireOp",EDGE,"E10"),sQuery(id+"F4.wireOp",EDGE,"E11.5.0"),sQuery(id+"F4.wireOp",EDGE,"E11.10.0"),sQuery(id+"F4.wireOp",EDGE,"E11.20.0"),sQuery(id+"F4.wireOp",EDGE,"E11.25.0"),sQuery(id+"F4.wireOp",EDGE,"E11.30.0"),sQuery(id+"F4.wireOp",EDGE,"E11.35.0"),sQuery(id+"F4.wireOp",EDGE,"E11.40.0"),sQuery(id+"F4.wireOp",EDGE,"E13.2.0"),sQuery(id+"F4.wireOp",EDGE,"E13.3.0"),sQuery(id+"F4.wireOp",EDGE,"E13.7.0"),sQuery(id+"F4.wireOp",EDGE,"E13.8.0"),sQuery(id+"F4.wireOp",EDGE,"E13.12.0"),sQuery(id+"F4.wireOp",EDGE,"E13.13.0"),sQuery(id+"F4.wireOp",EDGE,"E14.1.17.0"),sQuery(id+"F4.wireOp",EDGE,"E14.1.18.0"),sQuery(id+"F4.wireOp",EDGE,"E14.1.22.0"),sQuery(id+"F4.wireOp",EDGE,"E14.1.23.0"),sQuery(id+"F4.wireOp",EDGE,"E14.1.27.0"),sQuery(id+"F4.wireOp",EDGE,"E14.1.28.0"),sQuery(id+"F4.wireOp",EDGE,"E15.1.32.0"),sQuery(id+"F4.wireOp",EDGE,"E15.1.33.0"),sQuery(id+"F4.wireOp",EDGE,"E15.1.37.0"),sQuery(id+"F4.wireOp",EDGE,"E15.1.38.0"),sQuery(id+"F4.wireOp",EDGE,"E15.1.42.0"),sQuery(id+"F4.wireOp",EDGE,"E15.1.43.0"),sQuery(id+"F4.wireOp",EDGE,"E16"),sQuery(id+"F4.wireOp",EDGE,"E17"),sQuery(id+"F4.wireOp",EDGE,"E18"),sQuery(id+"F4.wireOp",EDGE,"E19"),sQuery(id+"F4.wireOp",EDGE,"E20"),sQuery(id+"F4.wireOp",EDGE,"E21"),sQuery(id+"F4.wireOp",EDGE,"E22"),sQuery(id+"F4.wireOp",EDGE,"E23"),sQuery(id+"F4.wireOp",EDGE,"E24"),sQuery(id+"F4.wireOp",EDGE,"E25"),sQuery(id+"F4.wireOp",EDGE,"E26"),sQuery(id+"F4.wireOp",EDGE,"E27"),sQuery(id+"F4.wireOp",EDGE,"E28"),sQuery(id+"F4.wireOp",EDGE,"E29"),sQuery(id+"F4.wireOp",EDGE,"E30"),sQuery(id+"F4.wireOp",EDGE,"E31"),sQuery(id+"F4.wireOp",EDGE,"E32"),sQuery(id+"F4.wireOp",EDGE,"E33"),sQuery(id+"F4.wireOp",EDGE,"E34")])],"isStart":false});
            extrude(context, id + "F7", {"entities" : qUnion([Q0]), "operationType" : NewBodyOperationType.REMOVE, "endBound" : BoundingType.UP_TO_SURFACE, "oppositeDirection" : true, "endBoundEntityFace" : qUnion([Q1]), "depth" : 25.4 * mm});
        }
        {
            var Q0;
            Q0=makeQuery(id+"F5.opExtrude","CAP_FACE",FACE,{"disambiguationData":[OSD([sQuery(id+"F4.wireOp",EDGE,"E10"),sQuery(id+"F4.wireOp",EDGE,"E11.5.0"),sQuery(id+"F4.wireOp",EDGE,"E11.10.0"),sQuery(id+"F4.wireOp",EDGE,"E11.20.0"),sQuery(id+"F4.wireOp",EDGE,"E11.25.0"),sQuery(id+"F4.wireOp",EDGE,"E11.30.0"),sQuery(id+"F4.wireOp",EDGE,"E11.35.0"),sQuery(id+"F4.wireOp",EDGE,"E11.40.0"),sQuery(id+"F4.wireOp",EDGE,"E13.2.0"),sQuery(id+"F4.wireOp",EDGE,"E13.3.0"),sQuery(id+"F4.wireOp",EDGE,"E13.7.0"),sQuery(id+"F4.wireOp",EDGE,"E13.8.0"),sQuery(id+"F4.wireOp",EDGE,"E13.12.0"),sQuery(id+"F4.wireOp",EDGE,"E13.13.0"),sQuery(id+"F4.wireOp",EDGE,"E14.1.17.0"),sQuery(id+"F4.wireOp",EDGE,"E14.1.18.0"),sQuery(id+"F4.wireOp",EDGE,"E14.1.22.0"),sQuery(id+"F4.wireOp",EDGE,"E14.1.23.0"),sQuery(id+"F4.wireOp",EDGE,"E14.1.27.0"),sQuery(id+"F4.wireOp",EDGE,"E14.1.28.0"),sQuery(id+"F4.wireOp",EDGE,"E15.1.32.0"),sQuery(id+"F4.wireOp",EDGE,"E15.1.33.0"),sQuery(id+"F4.wireOp",EDGE,"E15.1.37.0"),sQuery(id+"F4.wireOp",EDGE,"E15.1.38.0"),sQuery(id+"F4.wireOp",EDGE,"E15.1.42.0"),sQuery(id+"F4.wireOp",EDGE,"E15.1.43.0"),sQuery(id+"F4.wireOp",EDGE,"E16"),sQuery(id+"F4.wireOp",EDGE,"E17"),sQuery(id+"F4.wireOp",EDGE,"E18"),sQuery(id+"F4.wireOp",EDGE,"E19"),sQuery(id+"F4.wireOp",EDGE,"E20"),sQuery(id+"F4.wireOp",EDGE,"E21"),sQuery(id+"F4.wireOp",EDGE,"E22"),sQuery(id+"F4.wireOp",EDGE,"E23"),sQuery(id+"F4.wireOp",EDGE,"E24"),sQuery(id+"F4.wireOp",EDGE,"E25"),sQuery(id+"F4.wireOp",EDGE,"E26"),sQuery(id+"F4.wireOp",EDGE,"E27"),sQuery(id+"F4.wireOp",EDGE,"E28"),sQuery(id+"F4.wireOp",EDGE,"E29"),sQuery(id+"F4.wireOp",EDGE,"E30"),sQuery(id+"F4.wireOp",EDGE,"E31"),sQuery(id+"F4.wireOp",EDGE,"E32"),sQuery(id+"F4.wireOp",EDGE,"E33"),sQuery(id+"F4.wireOp",EDGE,"E34")])],"isStart":false});
            extrude(context, id + "F8", {"entities" : qUnion([Q0]), "depth" : 6.35 * mm, "hasDraft" : true, "draftAngle" : 60 * degree, "draftPullDirection" : true});
        }
        {
            var Q0;
            Q0=makeQuery(id+"F0.imprint","IMPRINT",FACE,{"disambiguationData":[TD([[makeQuery(id+"F0.imprint","IMPRINT",EDGE,{"derivedFrom":sQuery(id+"F0.wireOp",EDGE,"E1")}),-1.0]])]});
            cPlane(context, id + "F9", {"entities" : qUnion([Q0]), "cplaneType" : CPlaneType.OFFSET, "offset" : 50.8 * mm, "width" : 152.4 * mm, "height" : 152.4 * mm});
        }
        {
            var Q0;
            Q0=makeQuery(id+"F5.opExtrude","SWEPT_BODY",BODY,{"disambiguationData":[OSD([sQuery(id+"F4.wireOp",EDGE,"E10"),sQuery(id+"F4.wireOp",EDGE,"E11.5.0"),sQuery(id+"F4.wireOp",EDGE,"E11.10.0"),sQuery(id+"F4.wireOp",EDGE,"E11.20.0"),sQuery(id+"F4.wireOp",EDGE,"E11.25.0"),sQuery(id+"F4.wireOp",EDGE,"E11.30.0"),sQuery(id+"F4.wireOp",EDGE,"E11.35.0"),sQuery(id+"F4.wireOp",EDGE,"E11.40.0"),sQuery(id+"F4.wireOp",EDGE,"E13.2.0"),sQuery(id+"F4.wireOp",EDGE,"E13.3.0"),sQuery(id+"F4.wireOp",EDGE,"E13.7.0"),sQuery(id+"F4.wireOp",EDGE,"E13.8.0"),sQuery(id+"F4.wireOp",EDGE,"E13.12.0"),sQuery(id+"F4.wireOp",EDGE,"E13.13.0"),sQuery(id+"F4.wireOp",EDGE,"E14.1.17.0"),sQuery(id+"F4.wireOp",EDGE,"E14.1.18.0"),sQuery(id+"F4.wireOp",EDGE,"E14.1.22.0"),sQuery(id+"F4.wireOp",EDGE,"E14.1.23.0"),sQuery(id+"F4.wireOp",EDGE,"E14.1.27.0"),sQuery(id+"F4.wireOp",EDGE,"E14.1.28.0"),sQuery(id+"F4.wireOp",EDGE,"E15.1.32.0"),sQuery(id+"F4.wireOp",EDGE,"E15.1.33.0"),sQuery(id+"F4.wireOp",EDGE,"E15.1.37.0"),sQuery(id+"F4.wireOp",EDGE,"E15.1.38.0"),sQuery(id+"F4.wireOp",EDGE,"E15.1.42.0"),sQuery(id+"F4.wireOp",EDGE,"E15.1.43.0"),sQuery(id+"F4.wireOp",EDGE,"E16"),sQuery(id+"F4.wireOp",EDGE,"E17"),sQuery(id+"F4.wireOp",EDGE,"E18"),sQuery(id+"F4.wireOp",EDGE,"E19"),sQuery(id+"F4.wireOp",EDGE,"E20"),sQuery(id+"F4.wireOp",EDGE,"E21"),sQuery(id+"F4.wireOp",EDGE,"E22"),sQuery(id+"F4.wireOp",EDGE,"E23"),sQuery(id+"F4.wireOp",EDGE,"E24"),sQuery(id+"F4.wireOp",EDGE,"E25"),sQuery(id+"F4.wireOp",EDGE,"E26"),sQuery(id+"F4.wireOp",EDGE,"E27"),sQuery(id+"F4.wireOp",EDGE,"E28"),sQuery(id+"F4.wireOp",EDGE,"E29"),sQuery(id+"F4.wireOp",EDGE,"E30"),sQuery(id+"F4.wireOp",EDGE,"E31"),sQuery(id+"F4.wireOp",EDGE,"E32"),sQuery(id+"F4.wireOp",EDGE,"E33"),sQuery(id+"F4.wireOp",EDGE,"E34")])]});
            var Q1;
            Q1=makeQuery(id+"F1.opExtrude","CAP_EDGE",EDGE,{"disambiguationData":[OSD([sQuery(id+"F0.wireOp",EDGE,"E7")])],"isStart":false});
            transform(context, id + "F10", {"entities" : qUnion([Q0]), "transformType" : TransformType.ROTATION, "transformAxis" : qUnion([Q1]), "angle" : 180 * degree, "makeCopy" : true});
        }
        {
            var Q0;
            Q0=qCreatedBy(makeId("Right.planeOp"),FACE);
            var sketch = newSketch(context, id + "F11", { "sketchPlane" : qUnion([Q0])});
            skCircle(sketch, "E36", {"center": v(-50.8, 0) * mm, "radius": 12.7 * mm});
            skSolve(sketch);
        }
        {
            var Q0;
            Q0 = qSketchRegion(id + "F11", true);
            extrude(context, id + "F12", {"entities" : qUnion([Q0]), "endBound" : BoundingType.SYMMETRIC, "depth" : 457.2 * mm});
        }
        {
            var Q0;
            Q0=makeQuery(id+"F1.opExtrude","SWEPT_BODY",BODY,{"disambiguationData":[OSD([sQuery(id+"F0.wireOp",EDGE,"E1"),sQuery(id+"F0.wireOp",EDGE,"E2.3.0"),sQuery(id+"F0.wireOp",EDGE,"E2.4.0"),sQuery(id+"F0.wireOp",EDGE,"E2.7.0"),sQuery(id+"F0.wireOp",EDGE,"E2.8.0"),sQuery(id+"F0.wireOp",EDGE,"E2.11.0"),sQuery(id+"F0.wireOp",EDGE,"E2.12.0"),sQuery(id+"F0.wireOp",EDGE,"E2.15.0"),sQuery(id+"F0.wireOp",EDGE,"E2.16.0"),sQuery(id+"F0.wireOp",EDGE,"E2.19.0"),sQuery(id+"F0.wireOp",EDGE,"E2.20.0"),sQuery(id+"F0.wireOp",EDGE,"E2.23.0"),sQuery(id+"F0.wireOp",EDGE,"E2.24.0"),sQuery(id+"F0.wireOp",EDGE,"E2.27.0"),sQuery(id+"F0.wireOp",EDGE,"E2.28.0"),sQuery(id+"F0.wireOp",EDGE,"E2.31.0"),sQuery(id+"F0.wireOp",EDGE,"E2.32.0"),sQuery(id+"F0.wireOp",EDGE,"E2.35.0"),sQuery(id+"F0.wireOp",EDGE,"E2.36.0"),sQuery(id+"F0.wireOp",EDGE,"E2.39.0"),sQuery(id+"F0.wireOp",EDGE,"E2.40.0"),sQuery(id+"F0.wireOp",EDGE,"E2.43.0"),sQuery(id+"F0.wireOp",EDGE,"E2.44.0"),sQuery(id+"F0.wireOp",EDGE,"E2.47.0"),sQuery(id+"F0.wireOp",EDGE,"E2.48.0"),sQuery(id+"F0.wireOp",EDGE,"E2.51.0"),sQuery(id+"F0.wireOp",EDGE,"E2.52.0"),sQuery(id+"F0.wireOp",EDGE,"E2.55.0"),sQuery(id+"F0.wireOp",EDGE,"E2.56.0"),sQuery(id+"F0.wireOp",EDGE,"E2.59.0"),sQuery(id+"F0.wireOp",EDGE,"E2.60.0"),sQuery(id+"F0.wireOp",EDGE,"E2.63.0"),sQuery(id+"F0.wireOp",EDGE,"E2.64.0"),sQuery(id+"F0.wireOp",EDGE,"E2.67.0"),sQuery(id+"F0.wireOp",EDGE,"E2.68.0"),sQuery(id+"F0.wireOp",EDGE,"E2.71.0"),sQuery(id+"F0.wireOp",EDGE,"E2.72.0"),sQuery(id+"F0.wireOp",EDGE,"E2.75.0"),sQuery(id+"F0.wireOp",EDGE,"E2.76.0"),sQuery(id+"F0.wireOp",EDGE,"E2.79.0"),sQuery(id+"F0.wireOp",EDGE,"E2.80.0"),sQuery(id+"F0.wireOp",EDGE,"E2.83.0"),sQuery(id+"F0.wireOp",EDGE,"E2.84.0"),sQuery(id+"F0.wireOp",EDGE,"E2.87.0"),sQuery(id+"F0.wireOp",EDGE,"E2.88.0"),sQuery(id+"F0.wireOp",EDGE,"E2.91.0"),sQuery(id+"F0.wireOp",EDGE,"E2.92.0"),sQuery(id+"F0.wireOp",EDGE,"E2.95.0"),sQuery(id+"F0.wireOp",EDGE,"E2.96.0"),sQuery(id+"F0.wireOp",EDGE,"E2.99.0"),sQuery(id+"F0.wireOp",EDGE,"E2.100.0"),sQuery(id+"F0.wireOp",EDGE,"E2.103.0"),sQuery(id+"F0.wireOp",EDGE,"E2.104.0"),sQuery(id+"F0.wireOp",EDGE,"E2.107.0"),sQuery(id+"F0.wireOp",EDGE,"E2.108.0"),sQuery(id+"F0.wireOp",EDGE,"E2.111.0"),sQuery(id+"F0.wireOp",EDGE,"E2.112.0"),sQuery(id+"F0.wireOp",EDGE,"E2.115.0"),sQuery(id+"F0.wireOp",EDGE,"E2.116.0"),sQuery(id+"F0.wireOp",EDGE,"E2.119.0"),sQuery(id+"F0.wireOp",EDGE,"E2.120.0"),sQuery(id+"F0.wireOp",EDGE,"E2.123.0"),sQuery(id+"F0.wireOp",EDGE,"E2.124.0"),sQuery(id+"F0.wireOp",EDGE,"E2.127.0"),sQuery(id+"F0.wireOp",EDGE,"E2.128.0"),sQuery(id+"F0.wireOp",EDGE,"E2.131.0"),sQuery(id+"F0.wireOp",EDGE,"E2.132.0"),sQuery(id+"F0.wireOp",EDGE,"E2.135.0"),sQuery(id+"F0.wireOp",EDGE,"E2.136.0"),sQuery(id+"F0.wireOp",EDGE,"E2.139.0"),sQuery(id+"F0.wireOp",EDGE,"E2.140.0"),sQuery(id+"F0.wireOp",EDGE,"E2.143.0"),sQuery(id+"F0.wireOp",EDGE,"E2.144.0"),sQuery(id+"F0.wireOp",EDGE,"E2.147.0"),sQuery(id+"F0.wireOp",EDGE,"E2.148.0"),sQuery(id+"F0.wireOp",EDGE,"E2.151.0"),sQuery(id+"F0.wireOp",EDGE,"E2.152.0"),sQuery(id+"F0.wireOp",EDGE,"E2.155.0"),sQuery(id+"F0.wireOp",EDGE,"E2.156.0"),sQuery(id+"F0.wireOp",EDGE,"E2.159.0"),sQuery(id+"F0.wireOp",EDGE,"E2.160.0"),sQuery(id+"F0.wireOp",EDGE,"E2.163.0"),sQuery(id+"F0.wireOp",EDGE,"E2.164.0"),sQuery(id+"F0.wireOp",EDGE,"E2.167.0"),sQuery(id+"F0.wireOp",EDGE,"E2.168.0"),sQuery(id+"F0.wireOp",EDGE,"E2.171.0"),sQuery(id+"F0.wireOp",EDGE,"E2.172.0"),sQuery(id+"F0.wireOp",EDGE,"E2.175.0"),sQuery(id+"F0.wireOp",EDGE,"E2.176.0"),sQuery(id+"F0.wireOp",EDGE,"E2.179.0"),sQuery(id+"F0.wireOp",EDGE,"E4.1.0"),sQuery(id+"F0.wireOp",EDGE,"E4.2.0"),sQuery(id+"F0.wireOp",EDGE,"E4.3.0"),sQuery(id+"F0.wireOp",EDGE,"E4.5.0"),sQuery(id+"F0.wireOp",EDGE,"E4.6.0"),sQuery(id+"F0.wireOp",EDGE,"E4.7.0"),sQuery(id+"F0.wireOp",EDGE,"E4.9.0"),sQuery(id+"F0.wireOp",EDGE,"E4.10.0"),sQuery(id+"F0.wireOp",EDGE,"E4.11.0"),sQuery(id+"F0.wireOp",EDGE,"E4.13.0"),sQuery(id+"F0.wireOp",EDGE,"E4.14.0"),sQuery(id+"F0.wireOp",EDGE,"E4.15.0"),sQuery(id+"F0.wireOp",EDGE,"E4.17.0"),sQuery(id+"F0.wireOp",EDGE,"E4.18.0"),sQuery(id+"F0.wireOp",EDGE,"E4.19.0"),sQuery(id+"F0.wireOp",EDGE,"E4.21.0"),sQuery(id+"F0.wireOp",EDGE,"E4.22.0"),sQuery(id+"F0.wireOp",EDGE,"E4.23.0"),sQuery(id+"F0.wireOp",EDGE,"E4.25.0"),sQuery(id+"F0.wireOp",EDGE,"E4.26.0"),sQuery(id+"F0.wireOp",EDGE,"E4.27.0"),sQuery(id+"F0.wireOp",EDGE,"E4.29.0"),sQuery(id+"F0.wireOp",EDGE,"E4.30.0"),sQuery(id+"F0.wireOp",EDGE,"E4.31.0"),sQuery(id+"F0.wireOp",EDGE,"E4.33.0"),sQuery(id+"F0.wireOp",EDGE,"E4.34.0"),sQuery(id+"F0.wireOp",EDGE,"E4.35.0"),sQuery(id+"F0.wireOp",EDGE,"E4.37.0"),sQuery(id+"F0.wireOp",EDGE,"E4.38.0"),sQuery(id+"F0.wireOp",EDGE,"E4.39.0"),sQuery(id+"F0.wireOp",EDGE,"E4.41.0"),sQuery(id+"F0.wireOp",EDGE,"E4.42.0"),sQuery(id+"F0.wireOp",EDGE,"E4.43.0"),sQuery(id+"F0.wireOp",EDGE,"E4.45.0"),sQuery(id+"F0.wireOp",EDGE,"E4.46.0"),sQuery(id+"F0.wireOp",EDGE,"E4.47.0"),sQuery(id+"F0.wireOp",EDGE,"E4.49.0"),sQuery(id+"F0.wireOp",EDGE,"E4.50.0"),sQuery(id+"F0.wireOp",EDGE,"E4.51.0"),sQuery(id+"F0.wireOp",EDGE,"E4.53.0"),sQuery(id+"F0.wireOp",EDGE,"E4.54.0"),sQuery(id+"F0.wireOp",EDGE,"E4.55.0"),sQuery(id+"F0.wireOp",EDGE,"E4.57.0"),sQuery(id+"F0.wireOp",EDGE,"E4.58.0"),sQuery(id+"F0.wireOp",EDGE,"E4.59.0"),sQuery(id+"F0.wireOp",EDGE,"E4.61.0"),sQuery(id+"F0.wireOp",EDGE,"E4.62.0"),sQuery(id+"F0.wireOp",EDGE,"E4.63.0"),sQuery(id+"F0.wireOp",EDGE,"E4.65.0"),sQuery(id+"F0.wireOp",EDGE,"E4.66.0"),sQuery(id+"F0.wireOp",EDGE,"E4.67.0"),sQuery(id+"F0.wireOp",EDGE,"E4.69.0"),sQuery(id+"F0.wireOp",EDGE,"E4.70.0"),sQuery(id+"F0.wireOp",EDGE,"E4.71.0"),sQuery(id+"F0.wireOp",EDGE,"E4.73.0"),sQuery(id+"F0.wireOp",EDGE,"E4.74.0"),sQuery(id+"F0.wireOp",EDGE,"E4.75.0"),sQuery(id+"F0.wireOp",EDGE,"E4.77.0"),sQuery(id+"F0.wireOp",EDGE,"E4.78.0"),sQuery(id+"F0.wireOp",EDGE,"E4.79.0"),sQuery(id+"F0.wireOp",EDGE,"E4.81.0"),sQuery(id+"F0.wireOp",EDGE,"E4.82.0"),sQuery(id+"F0.wireOp",EDGE,"E4.83.0"),sQuery(id+"F0.wireOp",EDGE,"E4.85.0"),sQuery(id+"F0.wireOp",EDGE,"E4.86.0"),sQuery(id+"F0.wireOp",EDGE,"E4.87.0"),sQuery(id+"F0.wireOp",EDGE,"E4.89.0"),sQuery(id+"F0.wireOp",EDGE,"E4.90.0"),sQuery(id+"F0.wireOp",EDGE,"E4.91.0"),sQuery(id+"F0.wireOp",EDGE,"E4.93.0"),sQuery(id+"F0.wireOp",EDGE,"E4.94.0"),sQuery(id+"F0.wireOp",EDGE,"E4.95.0"),sQuery(id+"F0.wireOp",EDGE,"E4.97.0"),sQuery(id+"F0.wireOp",EDGE,"E4.98.0"),sQuery(id+"F0.wireOp",EDGE,"E4.99.0"),sQuery(id+"F0.wireOp",EDGE,"E4.101.0"),sQuery(id+"F0.wireOp",EDGE,"E4.102.0"),sQuery(id+"F0.wireOp",EDGE,"E4.103.0"),sQuery(id+"F0.wireOp",EDGE,"E4.105.0"),sQuery(id+"F0.wireOp",EDGE,"E4.106.0"),sQuery(id+"F0.wireOp",EDGE,"E4.107.0"),sQuery(id+"F0.wireOp",EDGE,"E4.109.0"),sQuery(id+"F0.wireOp",EDGE,"E4.110.0"),sQuery(id+"F0.wireOp",EDGE,"E4.111.0"),sQuery(id+"F0.wireOp",EDGE,"E4.113.0"),sQuery(id+"F0.wireOp",EDGE,"E4.114.0"),sQuery(id+"F0.wireOp",EDGE,"E4.115.0"),sQuery(id+"F0.wireOp",EDGE,"E4.117.0"),sQuery(id+"F0.wireOp",EDGE,"E4.118.0"),sQuery(id+"F0.wireOp",EDGE,"E4.119.0"),sQuery(id+"F0.wireOp",EDGE,"E4.121.0"),sQuery(id+"F0.wireOp",EDGE,"E4.122.0"),sQuery(id+"F0.wireOp",EDGE,"E4.123.0"),sQuery(id+"F0.wireOp",EDGE,"E4.125.0"),sQuery(id+"F0.wireOp",EDGE,"E4.126.0"),sQuery(id+"F0.wireOp",EDGE,"E4.127.0"),sQuery(id+"F0.wireOp",EDGE,"E4.129.0"),sQuery(id+"F0.wireOp",EDGE,"E4.130.0"),sQuery(id+"F0.wireOp",EDGE,"E4.131.0"),sQuery(id+"F0.wireOp",EDGE,"E4.133.0"),sQuery(id+"F0.wireOp",EDGE,"E4.134.0"),sQuery(id+"F0.wireOp",EDGE,"E4.135.0"),sQuery(id+"F0.wireOp",EDGE,"E4.137.0"),sQuery(id+"F0.wireOp",EDGE,"E4.138.0"),sQuery(id+"F0.wireOp",EDGE,"E4.139.0"),sQuery(id+"F0.wireOp",EDGE,"E4.141.0"),sQuery(id+"F0.wireOp",EDGE,"E4.142.0"),sQuery(id+"F0.wireOp",EDGE,"E4.143.0"),sQuery(id+"F0.wireOp",EDGE,"E4.145.0"),sQuery(id+"F0.wireOp",EDGE,"E4.146.0"),sQuery(id+"F0.wireOp",EDGE,"E4.147.0"),sQuery(id+"F0.wireOp",EDGE,"E4.149.0"),sQuery(id+"F0.wireOp",EDGE,"E4.150.0"),sQuery(id+"F0.wireOp",EDGE,"E4.151.0"),sQuery(id+"F0.wireOp",EDGE,"E4.153.0"),sQuery(id+"F0.wireOp",EDGE,"E4.154.0"),sQuery(id+"F0.wireOp",EDGE,"E4.155.0"),sQuery(id+"F0.wireOp",EDGE,"E4.157.0"),sQuery(id+"F0.wireOp",EDGE,"E4.158.0"),sQuery(id+"F0.wireOp",EDGE,"E4.159.0"),sQuery(id+"F0.wireOp",EDGE,"E4.161.0"),sQuery(id+"F0.wireOp",EDGE,"E4.162.0"),sQuery(id+"F0.wireOp",EDGE,"E4.163.0"),sQuery(id+"F0.wireOp",EDGE,"E4.165.0"),sQuery(id+"F0.wireOp",EDGE,"E4.166.0"),sQuery(id+"F0.wireOp",EDGE,"E4.167.0"),sQuery(id+"F0.wireOp",EDGE,"E4.169.0"),sQuery(id+"F0.wireOp",EDGE,"E4.170.0"),sQuery(id+"F0.wireOp",EDGE,"E4.171.0"),sQuery(id+"F0.wireOp",EDGE,"E4.173.0"),sQuery(id+"F0.wireOp",EDGE,"E4.174.0"),sQuery(id+"F0.wireOp",EDGE,"E4.175.0"),sQuery(id+"F0.wireOp",EDGE,"E4.177.0"),sQuery(id+"F0.wireOp",EDGE,"E4.178.0"),sQuery(id+"F0.wireOp",EDGE,"E4.179.0"),sQuery(id+"F0.wireOp",EDGE,"E5"),sQuery(id+"F0.wireOp",EDGE,"E6.1.0"),sQuery(id+"F0.wireOp",EDGE,"E6.2.0"),sQuery(id+"F0.wireOp",EDGE,"E6.3.0"),sQuery(id+"F0.wireOp",EDGE,"E6.4.0"),sQuery(id+"F0.wireOp",EDGE,"E6.5.0"),sQuery(id+"F0.wireOp",EDGE,"E6.6.0"),sQuery(id+"F0.wireOp",EDGE,"E6.7.0"),sQuery(id+"F0.wireOp",EDGE,"E6.8.0"),sQuery(id+"F0.wireOp",EDGE,"E6.9.0"),sQuery(id+"F0.wireOp",EDGE,"E6.10.0"),sQuery(id+"F0.wireOp",EDGE,"E6.11.0"),sQuery(id+"F0.wireOp",EDGE,"E6.12.0"),sQuery(id+"F0.wireOp",EDGE,"E6.13.0"),sQuery(id+"F0.wireOp",EDGE,"E6.14.0"),sQuery(id+"F0.wireOp",EDGE,"E6.15.0"),sQuery(id+"F0.wireOp",EDGE,"E6.16.0"),sQuery(id+"F0.wireOp",EDGE,"E6.17.0"),sQuery(id+"F0.wireOp",EDGE,"E6.18.0"),sQuery(id+"F0.wireOp",EDGE,"E6.19.0"),sQuery(id+"F0.wireOp",EDGE,"E6.20.0"),sQuery(id+"F0.wireOp",EDGE,"E6.21.0"),sQuery(id+"F0.wireOp",EDGE,"E6.22.0"),sQuery(id+"F0.wireOp",EDGE,"E6.23.0"),sQuery(id+"F0.wireOp",EDGE,"E6.24.0"),sQuery(id+"F0.wireOp",EDGE,"E6.25.0"),sQuery(id+"F0.wireOp",EDGE,"E6.26.0"),sQuery(id+"F0.wireOp",EDGE,"E6.27.0"),sQuery(id+"F0.wireOp",EDGE,"E6.28.0"),sQuery(id+"F0.wireOp",EDGE,"E6.29.0"),sQuery(id+"F0.wireOp",EDGE,"E6.30.0"),sQuery(id+"F0.wireOp",EDGE,"E6.31.0"),sQuery(id+"F0.wireOp",EDGE,"E6.32.0"),sQuery(id+"F0.wireOp",EDGE,"E6.33.0"),sQuery(id+"F0.wireOp",EDGE,"E6.34.0"),sQuery(id+"F0.wireOp",EDGE,"E6.35.0"),sQuery(id+"F0.wireOp",EDGE,"E6.36.0"),sQuery(id+"F0.wireOp",EDGE,"E6.37.0"),sQuery(id+"F0.wireOp",EDGE,"E6.38.0"),sQuery(id+"F0.wireOp",EDGE,"E6.39.0"),sQuery(id+"F0.wireOp",EDGE,"E6.40.0"),sQuery(id+"F0.wireOp",EDGE,"E6.41.0"),sQuery(id+"F0.wireOp",EDGE,"E6.42.0"),sQuery(id+"F0.wireOp",EDGE,"E6.43.0"),sQuery(id+"F0.wireOp",EDGE,"E6.44.0"),sQuery(id+"F0.wireOp",EDGE,"E7")])]});
            var Q1;
            Q1=makeQuery(id+"F12.opExtrude","CAP_EDGE",EDGE,{"disambiguationData":[OSD([sQuery(id+"F11.wireOp",EDGE,"E36")])],"isStart":false});
            transform(context, id + "F13", {"entities" : qUnion([Q0]), "transformType" : TransformType.ROTATION, "transformAxis" : qUnion([Q1]), "angle" : 180 * degree, "makeCopy" : true});
        }
        {
            var Q0;
            Q0=makeQuery(id+"F2.opExtrude","CAP_FACE",FACE,{"disambiguationData":[OSD([sQuery(id+"F0.wireOp",EDGE,"E3"),sQuery(id+"F0.wireOp",EDGE,"E4.1.0"),sQuery(id+"F0.wireOp",EDGE,"E4.2.0"),sQuery(id+"F0.wireOp",EDGE,"E4.3.0"),sQuery(id+"F0.wireOp",EDGE,"E4.4.0"),sQuery(id+"F0.wireOp",EDGE,"E4.5.0"),sQuery(id+"F0.wireOp",EDGE,"E4.6.0"),sQuery(id+"F0.wireOp",EDGE,"E4.7.0"),sQuery(id+"F0.wireOp",EDGE,"E4.8.0"),sQuery(id+"F0.wireOp",EDGE,"E4.9.0"),sQuery(id+"F0.wireOp",EDGE,"E4.10.0"),sQuery(id+"F0.wireOp",EDGE,"E4.11.0"),sQuery(id+"F0.wireOp",EDGE,"E4.12.0"),sQuery(id+"F0.wireOp",EDGE,"E4.13.0"),sQuery(id+"F0.wireOp",EDGE,"E4.14.0"),sQuery(id+"F0.wireOp",EDGE,"E4.15.0"),sQuery(id+"F0.wireOp",EDGE,"E4.16.0"),sQuery(id+"F0.wireOp",EDGE,"E4.17.0"),sQuery(id+"F0.wireOp",EDGE,"E4.18.0"),sQuery(id+"F0.wireOp",EDGE,"E4.19.0"),sQuery(id+"F0.wireOp",EDGE,"E4.20.0"),sQuery(id+"F0.wireOp",EDGE,"E4.21.0"),sQuery(id+"F0.wireOp",EDGE,"E4.22.0"),sQuery(id+"F0.wireOp",EDGE,"E4.23.0"),sQuery(id+"F0.wireOp",EDGE,"E4.24.0"),sQuery(id+"F0.wireOp",EDGE,"E4.25.0"),sQuery(id+"F0.wireOp",EDGE,"E4.26.0"),sQuery(id+"F0.wireOp",EDGE,"E4.27.0"),sQuery(id+"F0.wireOp",EDGE,"E4.28.0"),sQuery(id+"F0.wireOp",EDGE,"E4.29.0"),sQuery(id+"F0.wireOp",EDGE,"E4.30.0"),sQuery(id+"F0.wireOp",EDGE,"E4.31.0"),sQuery(id+"F0.wireOp",EDGE,"E4.32.0"),sQuery(id+"F0.wireOp",EDGE,"E4.33.0"),sQuery(id+"F0.wireOp",EDGE,"E4.34.0"),sQuery(id+"F0.wireOp",EDGE,"E4.35.0"),sQuery(id+"F0.wireOp",EDGE,"E4.36.0"),sQuery(id+"F0.wireOp",EDGE,"E4.37.0"),sQuery(id+"F0.wireOp",EDGE,"E4.38.0"),sQuery(id+"F0.wireOp",EDGE,"E4.39.0"),sQuery(id+"F0.wireOp",EDGE,"E4.40.0"),sQuery(id+"F0.wireOp",EDGE,"E4.41.0"),sQuery(id+"F0.wireOp",EDGE,"E4.42.0"),sQuery(id+"F0.wireOp",EDGE,"E4.43.0"),sQuery(id+"F0.wireOp",EDGE,"E4.44.0"),sQuery(id+"F0.wireOp",EDGE,"E4.45.0"),sQuery(id+"F0.wireOp",EDGE,"E4.46.0"),sQuery(id+"F0.wireOp",EDGE,"E4.47.0"),sQuery(id+"F0.wireOp",EDGE,"E4.48.0"),sQuery(id+"F0.wireOp",EDGE,"E4.49.0"),sQuery(id+"F0.wireOp",EDGE,"E4.50.0"),sQuery(id+"F0.wireOp",EDGE,"E4.51.0"),sQuery(id+"F0.wireOp",EDGE,"E4.52.0"),sQuery(id+"F0.wireOp",EDGE,"E4.53.0"),sQuery(id+"F0.wireOp",EDGE,"E4.54.0"),sQuery(id+"F0.wireOp",EDGE,"E4.55.0"),sQuery(id+"F0.wireOp",EDGE,"E4.56.0"),sQuery(id+"F0.wireOp",EDGE,"E4.57.0"),sQuery(id+"F0.wireOp",EDGE,"E4.58.0"),sQuery(id+"F0.wireOp",EDGE,"E4.59.0"),sQuery(id+"F0.wireOp",EDGE,"E4.60.0"),sQuery(id+"F0.wireOp",EDGE,"E4.61.0"),sQuery(id+"F0.wireOp",EDGE,"E4.62.0"),sQuery(id+"F0.wireOp",EDGE,"E4.63.0"),sQuery(id+"F0.wireOp",EDGE,"E4.64.0"),sQuery(id+"F0.wireOp",EDGE,"E4.65.0"),sQuery(id+"F0.wireOp",EDGE,"E4.66.0"),sQuery(id+"F0.wireOp",EDGE,"E4.67.0"),sQuery(id+"F0.wireOp",EDGE,"E4.68.0"),sQuery(id+"F0.wireOp",EDGE,"E4.69.0"),sQuery(id+"F0.wireOp",EDGE,"E4.70.0"),sQuery(id+"F0.wireOp",EDGE,"E4.71.0"),sQuery(id+"F0.wireOp",EDGE,"E4.72.0"),sQuery(id+"F0.wireOp",EDGE,"E4.73.0"),sQuery(id+"F0.wireOp",EDGE,"E4.74.0"),sQuery(id+"F0.wireOp",EDGE,"E4.75.0"),sQuery(id+"F0.wireOp",EDGE,"E4.76.0"),sQuery(id+"F0.wireOp",EDGE,"E4.77.0"),sQuery(id+"F0.wireOp",EDGE,"E4.78.0"),sQuery(id+"F0.wireOp",EDGE,"E4.79.0"),sQuery(id+"F0.wireOp",EDGE,"E4.80.0"),sQuery(id+"F0.wireOp",EDGE,"E4.81.0"),sQuery(id+"F0.wireOp",EDGE,"E4.82.0"),sQuery(id+"F0.wireOp",EDGE,"E4.83.0"),sQuery(id+"F0.wireOp",EDGE,"E4.84.0"),sQuery(id+"F0.wireOp",EDGE,"E4.85.0"),sQuery(id+"F0.wireOp",EDGE,"E4.86.0"),sQuery(id+"F0.wireOp",EDGE,"E4.87.0"),sQuery(id+"F0.wireOp",EDGE,"E4.88.0"),sQuery(id+"F0.wireOp",EDGE,"E4.89.0"),sQuery(id+"F0.wireOp",EDGE,"E4.90.0"),sQuery(id+"F0.wireOp",EDGE,"E4.91.0"),sQuery(id+"F0.wireOp",EDGE,"E4.92.0"),sQuery(id+"F0.wireOp",EDGE,"E4.93.0"),sQuery(id+"F0.wireOp",EDGE,"E4.94.0"),sQuery(id+"F0.wireOp",EDGE,"E4.95.0"),sQuery(id+"F0.wireOp",EDGE,"E4.96.0"),sQuery(id+"F0.wireOp",EDGE,"E4.97.0"),sQuery(id+"F0.wireOp",EDGE,"E4.98.0"),sQuery(id+"F0.wireOp",EDGE,"E4.99.0"),sQuery(id+"F0.wireOp",EDGE,"E4.100.0"),sQuery(id+"F0.wireOp",EDGE,"E4.101.0"),sQuery(id+"F0.wireOp",EDGE,"E4.102.0"),sQuery(id+"F0.wireOp",EDGE,"E4.103.0"),sQuery(id+"F0.wireOp",EDGE,"E4.104.0"),sQuery(id+"F0.wireOp",EDGE,"E4.105.0"),sQuery(id+"F0.wireOp",EDGE,"E4.106.0"),sQuery(id+"F0.wireOp",EDGE,"E4.107.0"),sQuery(id+"F0.wireOp",EDGE,"E4.108.0"),sQuery(id+"F0.wireOp",EDGE,"E4.109.0"),sQuery(id+"F0.wireOp",EDGE,"E4.110.0"),sQuery(id+"F0.wireOp",EDGE,"E4.111.0"),sQuery(id+"F0.wireOp",EDGE,"E4.112.0"),sQuery(id+"F0.wireOp",EDGE,"E4.113.0"),sQuery(id+"F0.wireOp",EDGE,"E4.114.0"),sQuery(id+"F0.wireOp",EDGE,"E4.115.0"),sQuery(id+"F0.wireOp",EDGE,"E4.116.0"),sQuery(id+"F0.wireOp",EDGE,"E4.117.0"),sQuery(id+"F0.wireOp",EDGE,"E4.118.0"),sQuery(id+"F0.wireOp",EDGE,"E4.119.0"),sQuery(id+"F0.wireOp",EDGE,"E4.120.0"),sQuery(id+"F0.wireOp",EDGE,"E4.121.0"),sQuery(id+"F0.wireOp",EDGE,"E4.122.0"),sQuery(id+"F0.wireOp",EDGE,"E4.123.0"),sQuery(id+"F0.wireOp",EDGE,"E4.124.0"),sQuery(id+"F0.wireOp",EDGE,"E4.125.0"),sQuery(id+"F0.wireOp",EDGE,"E4.126.0"),sQuery(id+"F0.wireOp",EDGE,"E4.127.0"),sQuery(id+"F0.wireOp",EDGE,"E4.128.0"),sQuery(id+"F0.wireOp",EDGE,"E4.129.0"),sQuery(id+"F0.wireOp",EDGE,"E4.130.0"),sQuery(id+"F0.wireOp",EDGE,"E4.131.0"),sQuery(id+"F0.wireOp",EDGE,"E4.132.0"),sQuery(id+"F0.wireOp",EDGE,"E4.133.0"),sQuery(id+"F0.wireOp",EDGE,"E4.134.0"),sQuery(id+"F0.wireOp",EDGE,"E4.135.0"),sQuery(id+"F0.wireOp",EDGE,"E4.136.0"),sQuery(id+"F0.wireOp",EDGE,"E4.137.0"),sQuery(id+"F0.wireOp",EDGE,"E4.138.0"),sQuery(id+"F0.wireOp",EDGE,"E4.139.0"),sQuery(id+"F0.wireOp",EDGE,"E4.140.0"),sQuery(id+"F0.wireOp",EDGE,"E4.141.0"),sQuery(id+"F0.wireOp",EDGE,"E4.142.0"),sQuery(id+"F0.wireOp",EDGE,"E4.143.0"),sQuery(id+"F0.wireOp",EDGE,"E4.144.0"),sQuery(id+"F0.wireOp",EDGE,"E4.145.0"),sQuery(id+"F0.wireOp",EDGE,"E4.146.0"),sQuery(id+"F0.wireOp",EDGE,"E4.147.0"),sQuery(id+"F0.wireOp",EDGE,"E4.148.0"),sQuery(id+"F0.wireOp",EDGE,"E4.149.0"),sQuery(id+"F0.wireOp",EDGE,"E4.150.0"),sQuery(id+"F0.wireOp",EDGE,"E4.151.0"),sQuery(id+"F0.wireOp",EDGE,"E4.152.0"),sQuery(id+"F0.wireOp",EDGE,"E4.153.0"),sQuery(id+"F0.wireOp",EDGE,"E4.154.0"),sQuery(id+"F0.wireOp",EDGE,"E4.155.0"),sQuery(id+"F0.wireOp",EDGE,"E4.156.0"),sQuery(id+"F0.wireOp",EDGE,"E4.157.0"),sQuery(id+"F0.wireOp",EDGE,"E4.158.0"),sQuery(id+"F0.wireOp",EDGE,"E4.159.0"),sQuery(id+"F0.wireOp",EDGE,"E4.160.0"),sQuery(id+"F0.wireOp",EDGE,"E4.161.0"),sQuery(id+"F0.wireOp",EDGE,"E4.162.0"),sQuery(id+"F0.wireOp",EDGE,"E4.163.0"),sQuery(id+"F0.wireOp",EDGE,"E4.164.0"),sQuery(id+"F0.wireOp",EDGE,"E4.165.0"),sQuery(id+"F0.wireOp",EDGE,"E4.166.0"),sQuery(id+"F0.wireOp",EDGE,"E4.167.0"),sQuery(id+"F0.wireOp",EDGE,"E4.168.0"),sQuery(id+"F0.wireOp",EDGE,"E4.169.0"),sQuery(id+"F0.wireOp",EDGE,"E4.170.0"),sQuery(id+"F0.wireOp",EDGE,"E4.171.0"),sQuery(id+"F0.wireOp",EDGE,"E4.172.0"),sQuery(id+"F0.wireOp",EDGE,"E4.173.0"),sQuery(id+"F0.wireOp",EDGE,"E4.174.0"),sQuery(id+"F0.wireOp",EDGE,"E4.175.0"),sQuery(id+"F0.wireOp",EDGE,"E4.176.0"),sQuery(id+"F0.wireOp",EDGE,"E4.177.0"),sQuery(id+"F0.wireOp",EDGE,"E4.178.0"),sQuery(id+"F0.wireOp",EDGE,"E4.179.0"),sQuery(id+"F0.wireOp",EDGE,"E7")])],"isStart":false});
            var sketch = newSketch(context, id + "F14", { "sketchPlane" : qUnion([Q0])});
            skCircle(sketch, "E37", {"center": v(0, 0) * mm, "radius": 12.7 * mm});
            skSolve(sketch);
        }
        {
            var Q0;
            Q0=makeQuery(id+"F10.opPattern","COPY",BODY,{"derivedFrom":makeQuery(id+"F5.opExtrude","SWEPT_BODY",BODY,{"disambiguationData":[OSD([sQuery(id+"F4.wireOp",EDGE,"E10"),sQuery(id+"F4.wireOp",EDGE,"E11.5.0"),sQuery(id+"F4.wireOp",EDGE,"E11.10.0"),sQuery(id+"F4.wireOp",EDGE,"E11.20.0"),sQuery(id+"F4.wireOp",EDGE,"E11.25.0"),sQuery(id+"F4.wireOp",EDGE,"E11.30.0"),sQuery(id+"F4.wireOp",EDGE,"E11.35.0"),sQuery(id+"F4.wireOp",EDGE,"E11.40.0"),sQuery(id+"F4.wireOp",EDGE,"E13.2.0"),sQuery(id+"F4.wireOp",EDGE,"E13.3.0"),sQuery(id+"F4.wireOp",EDGE,"E13.7.0"),sQuery(id+"F4.wireOp",EDGE,"E13.8.0"),sQuery(id+"F4.wireOp",EDGE,"E13.12.0"),sQuery(id+"F4.wireOp",EDGE,"E13.13.0"),sQuery(id+"F4.wireOp",EDGE,"E14.1.17.0"),sQuery(id+"F4.wireOp",EDGE,"E14.1.18.0"),sQuery(id+"F4.wireOp",EDGE,"E14.1.22.0"),sQuery(id+"F4.wireOp",EDGE,"E14.1.23.0"),sQuery(id+"F4.wireOp",EDGE,"E14.1.27.0"),sQuery(id+"F4.wireOp",EDGE,"E14.1.28.0"),sQuery(id+"F4.wireOp",EDGE,"E15.1.32.0"),sQuery(id+"F4.wireOp",EDGE,"E15.1.33.0"),sQuery(id+"F4.wireOp",EDGE,"E15.1.37.0"),sQuery(id+"F4.wireOp",EDGE,"E15.1.38.0"),sQuery(id+"F4.wireOp",EDGE,"E15.1.42.0"),sQuery(id+"F4.wireOp",EDGE,"E15.1.43.0"),sQuery(id+"F4.wireOp",EDGE,"E16"),sQuery(id+"F4.wireOp",EDGE,"E17"),sQuery(id+"F4.wireOp",EDGE,"E18"),sQuery(id+"F4.wireOp",EDGE,"E19"),sQuery(id+"F4.wireOp",EDGE,"E20"),sQuery(id+"F4.wireOp",EDGE,"E21"),sQuery(id+"F4.wireOp",EDGE,"E22"),sQuery(id+"F4.wireOp",EDGE,"E23"),sQuery(id+"F4.wireOp",EDGE,"E24"),sQuery(id+"F4.wireOp",EDGE,"E25"),sQuery(id+"F4.wireOp",EDGE,"E26"),sQuery(id+"F4.wireOp",EDGE,"E27"),sQuery(id+"F4.wireOp",EDGE,"E28"),sQuery(id+"F4.wireOp",EDGE,"E29"),sQuery(id+"F4.wireOp",EDGE,"E30"),sQuery(id+"F4.wireOp",EDGE,"E31"),sQuery(id+"F4.wireOp",EDGE,"E32"),sQuery(id+"F4.wireOp",EDGE,"E33"),sQuery(id+"F4.wireOp",EDGE,"E34")])]}),"instanceName":"1"});
            var Q1;
            Q1=makeQuery(id+"F12.opExtrude","SWEPT_BODY",BODY,{"disambiguationData":[OSD([sQuery(id+"F11.wireOp",EDGE,"E36")])]});
            var Q2;
            Q2=makeQuery(id+"F5.opExtrude","SWEPT_BODY",BODY,{"disambiguationData":[OSD([sQuery(id+"F4.wireOp",EDGE,"E10"),sQuery(id+"F4.wireOp",EDGE,"E11.5.0"),sQuery(id+"F4.wireOp",EDGE,"E11.10.0"),sQuery(id+"F4.wireOp",EDGE,"E11.20.0"),sQuery(id+"F4.wireOp",EDGE,"E11.25.0"),sQuery(id+"F4.wireOp",EDGE,"E11.30.0"),sQuery(id+"F4.wireOp",EDGE,"E11.35.0"),sQuery(id+"F4.wireOp",EDGE,"E11.40.0"),sQuery(id+"F4.wireOp",EDGE,"E13.2.0"),sQuery(id+"F4.wireOp",EDGE,"E13.3.0"),sQuery(id+"F4.wireOp",EDGE,"E13.7.0"),sQuery(id+"F4.wireOp",EDGE,"E13.8.0"),sQuery(id+"F4.wireOp",EDGE,"E13.12.0"),sQuery(id+"F4.wireOp",EDGE,"E13.13.0"),sQuery(id+"F4.wireOp",EDGE,"E14.1.17.0"),sQuery(id+"F4.wireOp",EDGE,"E14.1.18.0"),sQuery(id+"F4.wireOp",EDGE,"E14.1.22.0"),sQuery(id+"F4.wireOp",EDGE,"E14.1.23.0"),sQuery(id+"F4.wireOp",EDGE,"E14.1.27.0"),sQuery(id+"F4.wireOp",EDGE,"E14.1.28.0"),sQuery(id+"F4.wireOp",EDGE,"E15.1.32.0"),sQuery(id+"F4.wireOp",EDGE,"E15.1.33.0"),sQuery(id+"F4.wireOp",EDGE,"E15.1.37.0"),sQuery(id+"F4.wireOp",EDGE,"E15.1.38.0"),sQuery(id+"F4.wireOp",EDGE,"E15.1.42.0"),sQuery(id+"F4.wireOp",EDGE,"E15.1.43.0"),sQuery(id+"F4.wireOp",EDGE,"E16"),sQuery(id+"F4.wireOp",EDGE,"E17"),sQuery(id+"F4.wireOp",EDGE,"E18"),sQuery(id+"F4.wireOp",EDGE,"E19"),sQuery(id+"F4.wireOp",EDGE,"E20"),sQuery(id+"F4.wireOp",EDGE,"E21"),sQuery(id+"F4.wireOp",EDGE,"E22"),sQuery(id+"F4.wireOp",EDGE,"E23"),sQuery(id+"F4.wireOp",EDGE,"E24"),sQuery(id+"F4.wireOp",EDGE,"E25"),sQuery(id+"F4.wireOp",EDGE,"E26"),sQuery(id+"F4.wireOp",EDGE,"E27"),sQuery(id+"F4.wireOp",EDGE,"E28"),sQuery(id+"F4.wireOp",EDGE,"E29"),sQuery(id+"F4.wireOp",EDGE,"E30"),sQuery(id+"F4.wireOp",EDGE,"E31"),sQuery(id+"F4.wireOp",EDGE,"E32"),sQuery(id+"F4.wireOp",EDGE,"E33"),sQuery(id+"F4.wireOp",EDGE,"E34")])]});
            var Q3;
            Q3=sQuery(id+"F14.wireOp",EDGE,"E37");
            transform(context, id + "F15", {"entities" : qUnion([Q0, Q1, Q2]), "transformType" : TransformType.ROTATION, "transformAxis" : qUnion([Q3]), "angle" : 90 * degree, "makeCopy" : true});
        }
        {
            var Q0;
            Q0=makeQuery(id+"F12.opExtrude","SWEPT_BODY",BODY,{"disambiguationData":[OSD([sQuery(id+"F11.wireOp",EDGE,"E36")])]});
            var Q1;
            Q1=makeQuery(id+"F15.opPattern","COPY",BODY,{"derivedFrom":makeQuery(id+"F12.opExtrude","SWEPT_BODY",BODY,{"disambiguationData":[OSD([sQuery(id+"F11.wireOp",EDGE,"E36")])]}),"instanceName":"1"});
            booleanBodies(context, id + "F16", {"operationType" : BooleanOperationType.UNION, "tools" : qUnion([Q0, Q1])});
        }
        {
            var Q0;
            Q0 = qSketchRegion(id + "F14", true);
            var Q1;
            Q1=makeQuery(id+"F13.opPattern","COPY",FACE,{"derivedFrom":makeQuery(id+"F2.opExtrude","CAP_FACE",FACE,{"disambiguationData":[OSD([sQuery(id+"F0.wireOp",EDGE,"E3"),sQuery(id+"F0.wireOp",EDGE,"E4.1.0"),sQuery(id+"F0.wireOp",EDGE,"E4.2.0"),sQuery(id+"F0.wireOp",EDGE,"E4.3.0"),sQuery(id+"F0.wireOp",EDGE,"E4.4.0"),sQuery(id+"F0.wireOp",EDGE,"E4.5.0"),sQuery(id+"F0.wireOp",EDGE,"E4.6.0"),sQuery(id+"F0.wireOp",EDGE,"E4.7.0"),sQuery(id+"F0.wireOp",EDGE,"E4.8.0"),sQuery(id+"F0.wireOp",EDGE,"E4.9.0"),sQuery(id+"F0.wireOp",EDGE,"E4.10.0"),sQuery(id+"F0.wireOp",EDGE,"E4.11.0"),sQuery(id+"F0.wireOp",EDGE,"E4.12.0"),sQuery(id+"F0.wireOp",EDGE,"E4.13.0"),sQuery(id+"F0.wireOp",EDGE,"E4.14.0"),sQuery(id+"F0.wireOp",EDGE,"E4.15.0"),sQuery(id+"F0.wireOp",EDGE,"E4.16.0"),sQuery(id+"F0.wireOp",EDGE,"E4.17.0"),sQuery(id+"F0.wireOp",EDGE,"E4.18.0"),sQuery(id+"F0.wireOp",EDGE,"E4.19.0"),sQuery(id+"F0.wireOp",EDGE,"E4.20.0"),sQuery(id+"F0.wireOp",EDGE,"E4.21.0"),sQuery(id+"F0.wireOp",EDGE,"E4.22.0"),sQuery(id+"F0.wireOp",EDGE,"E4.23.0"),sQuery(id+"F0.wireOp",EDGE,"E4.24.0"),sQuery(id+"F0.wireOp",EDGE,"E4.25.0"),sQuery(id+"F0.wireOp",EDGE,"E4.26.0"),sQuery(id+"F0.wireOp",EDGE,"E4.27.0"),sQuery(id+"F0.wireOp",EDGE,"E4.28.0"),sQuery(id+"F0.wireOp",EDGE,"E4.29.0"),sQuery(id+"F0.wireOp",EDGE,"E4.30.0"),sQuery(id+"F0.wireOp",EDGE,"E4.31.0"),sQuery(id+"F0.wireOp",EDGE,"E4.32.0"),sQuery(id+"F0.wireOp",EDGE,"E4.33.0"),sQuery(id+"F0.wireOp",EDGE,"E4.34.0"),sQuery(id+"F0.wireOp",EDGE,"E4.35.0"),sQuery(id+"F0.wireOp",EDGE,"E4.36.0"),sQuery(id+"F0.wireOp",EDGE,"E4.37.0"),sQuery(id+"F0.wireOp",EDGE,"E4.38.0"),sQuery(id+"F0.wireOp",EDGE,"E4.39.0"),sQuery(id+"F0.wireOp",EDGE,"E4.40.0"),sQuery(id+"F0.wireOp",EDGE,"E4.41.0"),sQuery(id+"F0.wireOp",EDGE,"E4.42.0"),sQuery(id+"F0.wireOp",EDGE,"E4.43.0"),sQuery(id+"F0.wireOp",EDGE,"E4.44.0"),sQuery(id+"F0.wireOp",EDGE,"E4.45.0"),sQuery(id+"F0.wireOp",EDGE,"E4.46.0"),sQuery(id+"F0.wireOp",EDGE,"E4.47.0"),sQuery(id+"F0.wireOp",EDGE,"E4.48.0"),sQuery(id+"F0.wireOp",EDGE,"E4.49.0"),sQuery(id+"F0.wireOp",EDGE,"E4.50.0"),sQuery(id+"F0.wireOp",EDGE,"E4.51.0"),sQuery(id+"F0.wireOp",EDGE,"E4.52.0"),sQuery(id+"F0.wireOp",EDGE,"E4.53.0"),sQuery(id+"F0.wireOp",EDGE,"E4.54.0"),sQuery(id+"F0.wireOp",EDGE,"E4.55.0"),sQuery(id+"F0.wireOp",EDGE,"E4.56.0"),sQuery(id+"F0.wireOp",EDGE,"E4.57.0"),sQuery(id+"F0.wireOp",EDGE,"E4.58.0"),sQuery(id+"F0.wireOp",EDGE,"E4.59.0"),sQuery(id+"F0.wireOp",EDGE,"E4.60.0"),sQuery(id+"F0.wireOp",EDGE,"E4.61.0"),sQuery(id+"F0.wireOp",EDGE,"E4.62.0"),sQuery(id+"F0.wireOp",EDGE,"E4.63.0"),sQuery(id+"F0.wireOp",EDGE,"E4.64.0"),sQuery(id+"F0.wireOp",EDGE,"E4.65.0"),sQuery(id+"F0.wireOp",EDGE,"E4.66.0"),sQuery(id+"F0.wireOp",EDGE,"E4.67.0"),sQuery(id+"F0.wireOp",EDGE,"E4.68.0"),sQuery(id+"F0.wireOp",EDGE,"E4.69.0"),sQuery(id+"F0.wireOp",EDGE,"E4.70.0"),sQuery(id+"F0.wireOp",EDGE,"E4.71.0"),sQuery(id+"F0.wireOp",EDGE,"E4.72.0"),sQuery(id+"F0.wireOp",EDGE,"E4.73.0"),sQuery(id+"F0.wireOp",EDGE,"E4.74.0"),sQuery(id+"F0.wireOp",EDGE,"E4.75.0"),sQuery(id+"F0.wireOp",EDGE,"E4.76.0"),sQuery(id+"F0.wireOp",EDGE,"E4.77.0"),sQuery(id+"F0.wireOp",EDGE,"E4.78.0"),sQuery(id+"F0.wireOp",EDGE,"E4.79.0"),sQuery(id+"F0.wireOp",EDGE,"E4.80.0"),sQuery(id+"F0.wireOp",EDGE,"E4.81.0"),sQuery(id+"F0.wireOp",EDGE,"E4.82.0"),sQuery(id+"F0.wireOp",EDGE,"E4.83.0"),sQuery(id+"F0.wireOp",EDGE,"E4.84.0"),sQuery(id+"F0.wireOp",EDGE,"E4.85.0"),sQuery(id+"F0.wireOp",EDGE,"E4.86.0"),sQuery(id+"F0.wireOp",EDGE,"E4.87.0"),sQuery(id+"F0.wireOp",EDGE,"E4.88.0"),sQuery(id+"F0.wireOp",EDGE,"E4.89.0"),sQuery(id+"F0.wireOp",EDGE,"E4.90.0"),sQuery(id+"F0.wireOp",EDGE,"E4.91.0"),sQuery(id+"F0.wireOp",EDGE,"E4.92.0"),sQuery(id+"F0.wireOp",EDGE,"E4.93.0"),sQuery(id+"F0.wireOp",EDGE,"E4.94.0"),sQuery(id+"F0.wireOp",EDGE,"E4.95.0"),sQuery(id+"F0.wireOp",EDGE,"E4.96.0"),sQuery(id+"F0.wireOp",EDGE,"E4.97.0"),sQuery(id+"F0.wireOp",EDGE,"E4.98.0"),sQuery(id+"F0.wireOp",EDGE,"E4.99.0"),sQuery(id+"F0.wireOp",EDGE,"E4.100.0"),sQuery(id+"F0.wireOp",EDGE,"E4.101.0"),sQuery(id+"F0.wireOp",EDGE,"E4.102.0"),sQuery(id+"F0.wireOp",EDGE,"E4.103.0"),sQuery(id+"F0.wireOp",EDGE,"E4.104.0"),sQuery(id+"F0.wireOp",EDGE,"E4.105.0"),sQuery(id+"F0.wireOp",EDGE,"E4.106.0"),sQuery(id+"F0.wireOp",EDGE,"E4.107.0"),sQuery(id+"F0.wireOp",EDGE,"E4.108.0"),sQuery(id+"F0.wireOp",EDGE,"E4.109.0"),sQuery(id+"F0.wireOp",EDGE,"E4.110.0"),sQuery(id+"F0.wireOp",EDGE,"E4.111.0"),sQuery(id+"F0.wireOp",EDGE,"E4.112.0"),sQuery(id+"F0.wireOp",EDGE,"E4.113.0"),sQuery(id+"F0.wireOp",EDGE,"E4.114.0"),sQuery(id+"F0.wireOp",EDGE,"E4.115.0"),sQuery(id+"F0.wireOp",EDGE,"E4.116.0"),sQuery(id+"F0.wireOp",EDGE,"E4.117.0"),sQuery(id+"F0.wireOp",EDGE,"E4.118.0"),sQuery(id+"F0.wireOp",EDGE,"E4.119.0"),sQuery(id+"F0.wireOp",EDGE,"E4.120.0"),sQuery(id+"F0.wireOp",EDGE,"E4.121.0"),sQuery(id+"F0.wireOp",EDGE,"E4.122.0"),sQuery(id+"F0.wireOp",EDGE,"E4.123.0"),sQuery(id+"F0.wireOp",EDGE,"E4.124.0"),sQuery(id+"F0.wireOp",EDGE,"E4.125.0"),sQuery(id+"F0.wireOp",EDGE,"E4.126.0"),sQuery(id+"F0.wireOp",EDGE,"E4.127.0"),sQuery(id+"F0.wireOp",EDGE,"E4.128.0"),sQuery(id+"F0.wireOp",EDGE,"E4.129.0"),sQuery(id+"F0.wireOp",EDGE,"E4.130.0"),sQuery(id+"F0.wireOp",EDGE,"E4.131.0"),sQuery(id+"F0.wireOp",EDGE,"E4.132.0"),sQuery(id+"F0.wireOp",EDGE,"E4.133.0"),sQuery(id+"F0.wireOp",EDGE,"E4.134.0"),sQuery(id+"F0.wireOp",EDGE,"E4.135.0"),sQuery(id+"F0.wireOp",EDGE,"E4.136.0"),sQuery(id+"F0.wireOp",EDGE,"E4.137.0"),sQuery(id+"F0.wireOp",EDGE,"E4.138.0"),sQuery(id+"F0.wireOp",EDGE,"E4.139.0"),sQuery(id+"F0.wireOp",EDGE,"E4.140.0"),sQuery(id+"F0.wireOp",EDGE,"E4.141.0"),sQuery(id+"F0.wireOp",EDGE,"E4.142.0"),sQuery(id+"F0.wireOp",EDGE,"E4.143.0"),sQuery(id+"F0.wireOp",EDGE,"E4.144.0"),sQuery(id+"F0.wireOp",EDGE,"E4.145.0"),sQuery(id+"F0.wireOp",EDGE,"E4.146.0"),sQuery(id+"F0.wireOp",EDGE,"E4.147.0"),sQuery(id+"F0.wireOp",EDGE,"E4.148.0"),sQuery(id+"F0.wireOp",EDGE,"E4.149.0"),sQuery(id+"F0.wireOp",EDGE,"E4.150.0"),sQuery(id+"F0.wireOp",EDGE,"E4.151.0"),sQuery(id+"F0.wireOp",EDGE,"E4.152.0"),sQuery(id+"F0.wireOp",EDGE,"E4.153.0"),sQuery(id+"F0.wireOp",EDGE,"E4.154.0"),sQuery(id+"F0.wireOp",EDGE,"E4.155.0"),sQuery(id+"F0.wireOp",EDGE,"E4.156.0"),sQuery(id+"F0.wireOp",EDGE,"E4.157.0"),sQuery(id+"F0.wireOp",EDGE,"E4.158.0"),sQuery(id+"F0.wireOp",EDGE,"E4.159.0"),sQuery(id+"F0.wireOp",EDGE,"E4.160.0"),sQuery(id+"F0.wireOp",EDGE,"E4.161.0"),sQuery(id+"F0.wireOp",EDGE,"E4.162.0"),sQuery(id+"F0.wireOp",EDGE,"E4.163.0"),sQuery(id+"F0.wireOp",EDGE,"E4.164.0"),sQuery(id+"F0.wireOp",EDGE,"E4.165.0"),sQuery(id+"F0.wireOp",EDGE,"E4.166.0"),sQuery(id+"F0.wireOp",EDGE,"E4.167.0"),sQuery(id+"F0.wireOp",EDGE,"E4.168.0"),sQuery(id+"F0.wireOp",EDGE,"E4.169.0"),sQuery(id+"F0.wireOp",EDGE,"E4.170.0"),sQuery(id+"F0.wireOp",EDGE,"E4.171.0"),sQuery(id+"F0.wireOp",EDGE,"E4.172.0"),sQuery(id+"F0.wireOp",EDGE,"E4.173.0"),sQuery(id+"F0.wireOp",EDGE,"E4.174.0"),sQuery(id+"F0.wireOp",EDGE,"E4.175.0"),sQuery(id+"F0.wireOp",EDGE,"E4.176.0"),sQuery(id+"F0.wireOp",EDGE,"E4.177.0"),sQuery(id+"F0.wireOp",EDGE,"E4.178.0"),sQuery(id+"F0.wireOp",EDGE,"E4.179.0"),sQuery(id+"F0.wireOp",EDGE,"E7")])],"isStart":false}),"instanceName":"1"});
            extrude(context, id + "F17", {"entities" : qUnion([Q0]), "operationType" : NewBodyOperationType.ADD, "endBound" : BoundingType.UP_TO_SURFACE, "oppositeDirection" : true, "endBoundEntityFace" : qUnion([Q1]), "depth" : 25.4 * mm});
        }
        {
            var Q0;
            Q0=qCreatedBy(id+"F9.planeOp",FACE);
            var sketch = newSketch(context, id + "F18", { "sketchPlane" : qUnion([Q0])});
            skCircle(sketch, "E38", {"center": v(0, 0) * mm, "radius": 228.6 * mm});
            skCircle(sketch, "E39", {"center": v(0, 0) * mm, "radius": 279.4 * mm});
            skSolve(sketch);
        }
        {
            var Q0;
            Q0=makeQuery(id+"F18.imprint","IMPRINT",FACE,{"disambiguationData":[TD([[makeQuery(id+"F18.imprint","IMPRINT",EDGE,{"derivedFrom":sQuery(id+"F18.wireOp",EDGE,"E38")}),-1.0]])]});
            extrude(context, id + "F19", {"entities" : qUnion([Q0]), "operationType" : NewBodyOperationType.ADD, "endBound" : BoundingType.SYMMETRIC, "depth" : 25.4 * mm});
        }
        {
            var Q0;
            Q0=makeQuery(id+"F19.opExtrude","CAP_EDGE",EDGE,{"disambiguationData":[OSD([sQuery(id+"F18.wireOp",EDGE,"E39")])],"isStart":true});
            var Q1;
            Q1=makeQuery(id+"F19.opExtrude","CAP_EDGE",EDGE,{"disambiguationData":[OSD([sQuery(id+"F18.wireOp",EDGE,"E39")])],"isStart":false});
            var Q2;
            Q2=makeQuery(id+"F19.boolean.opBoolean","SPLIT",EDGE,{"disambiguationData":[OD(2.0)],"derivedFrom":makeQuery(id+"F19.opExtrude","CAP_EDGE",EDGE,{"disambiguationData":[OSD([sQuery(id+"F18.wireOp",EDGE,"E38")])],"isStart":true})});
            var Q3;
            Q3=makeQuery(id+"F19.boolean.opBoolean","SPLIT",EDGE,{"disambiguationData":[OD(0.0)],"derivedFrom":makeQuery(id+"F19.opExtrude","CAP_EDGE",EDGE,{"disambiguationData":[OSD([sQuery(id+"F18.wireOp",EDGE,"E38")])],"isStart":false})});
            fillet(context, id + "F20", {"entities" : qUnion([Q0, Q1, Q2, Q3]), "radius" : 12.7 * mm, "tangentPropagation" : true, "allowEdgeOverflow" : false});
        }
        {
            var Q0;
            Q0=makeQuery(id+"F1.opExtrude","SWEPT_BODY",BODY,{"disambiguationData":[OSD([sQuery(id+"F0.wireOp",EDGE,"E1"),sQuery(id+"F0.wireOp",EDGE,"E2.3.0"),sQuery(id+"F0.wireOp",EDGE,"E2.4.0"),sQuery(id+"F0.wireOp",EDGE,"E2.7.0"),sQuery(id+"F0.wireOp",EDGE,"E2.8.0"),sQuery(id+"F0.wireOp",EDGE,"E2.11.0"),sQuery(id+"F0.wireOp",EDGE,"E2.12.0"),sQuery(id+"F0.wireOp",EDGE,"E2.15.0"),sQuery(id+"F0.wireOp",EDGE,"E2.16.0"),sQuery(id+"F0.wireOp",EDGE,"E2.19.0"),sQuery(id+"F0.wireOp",EDGE,"E2.20.0"),sQuery(id+"F0.wireOp",EDGE,"E2.23.0"),sQuery(id+"F0.wireOp",EDGE,"E2.24.0"),sQuery(id+"F0.wireOp",EDGE,"E2.27.0"),sQuery(id+"F0.wireOp",EDGE,"E2.28.0"),sQuery(id+"F0.wireOp",EDGE,"E2.31.0"),sQuery(id+"F0.wireOp",EDGE,"E2.32.0"),sQuery(id+"F0.wireOp",EDGE,"E2.35.0"),sQuery(id+"F0.wireOp",EDGE,"E2.36.0"),sQuery(id+"F0.wireOp",EDGE,"E2.39.0"),sQuery(id+"F0.wireOp",EDGE,"E2.40.0"),sQuery(id+"F0.wireOp",EDGE,"E2.43.0"),sQuery(id+"F0.wireOp",EDGE,"E2.44.0"),sQuery(id+"F0.wireOp",EDGE,"E2.47.0"),sQuery(id+"F0.wireOp",EDGE,"E2.48.0"),sQuery(id+"F0.wireOp",EDGE,"E2.51.0"),sQuery(id+"F0.wireOp",EDGE,"E2.52.0"),sQuery(id+"F0.wireOp",EDGE,"E2.55.0"),sQuery(id+"F0.wireOp",EDGE,"E2.56.0"),sQuery(id+"F0.wireOp",EDGE,"E2.59.0"),sQuery(id+"F0.wireOp",EDGE,"E2.60.0"),sQuery(id+"F0.wireOp",EDGE,"E2.63.0"),sQuery(id+"F0.wireOp",EDGE,"E2.64.0"),sQuery(id+"F0.wireOp",EDGE,"E2.67.0"),sQuery(id+"F0.wireOp",EDGE,"E2.68.0"),sQuery(id+"F0.wireOp",EDGE,"E2.71.0"),sQuery(id+"F0.wireOp",EDGE,"E2.72.0"),sQuery(id+"F0.wireOp",EDGE,"E2.75.0"),sQuery(id+"F0.wireOp",EDGE,"E2.76.0"),sQuery(id+"F0.wireOp",EDGE,"E2.79.0"),sQuery(id+"F0.wireOp",EDGE,"E2.80.0"),sQuery(id+"F0.wireOp",EDGE,"E2.83.0"),sQuery(id+"F0.wireOp",EDGE,"E2.84.0"),sQuery(id+"F0.wireOp",EDGE,"E2.87.0"),sQuery(id+"F0.wireOp",EDGE,"E2.88.0"),sQuery(id+"F0.wireOp",EDGE,"E2.91.0"),sQuery(id+"F0.wireOp",EDGE,"E2.92.0"),sQuery(id+"F0.wireOp",EDGE,"E2.95.0"),sQuery(id+"F0.wireOp",EDGE,"E2.96.0"),sQuery(id+"F0.wireOp",EDGE,"E2.99.0"),sQuery(id+"F0.wireOp",EDGE,"E2.100.0"),sQuery(id+"F0.wireOp",EDGE,"E2.103.0"),sQuery(id+"F0.wireOp",EDGE,"E2.104.0"),sQuery(id+"F0.wireOp",EDGE,"E2.107.0"),sQuery(id+"F0.wireOp",EDGE,"E2.108.0"),sQuery(id+"F0.wireOp",EDGE,"E2.111.0"),sQuery(id+"F0.wireOp",EDGE,"E2.112.0"),sQuery(id+"F0.wireOp",EDGE,"E2.115.0"),sQuery(id+"F0.wireOp",EDGE,"E2.116.0"),sQuery(id+"F0.wireOp",EDGE,"E2.119.0"),sQuery(id+"F0.wireOp",EDGE,"E2.120.0"),sQuery(id+"F0.wireOp",EDGE,"E2.123.0"),sQuery(id+"F0.wireOp",EDGE,"E2.124.0"),sQuery(id+"F0.wireOp",EDGE,"E2.127.0"),sQuery(id+"F0.wireOp",EDGE,"E2.128.0"),sQuery(id+"F0.wireOp",EDGE,"E2.131.0"),sQuery(id+"F0.wireOp",EDGE,"E2.132.0"),sQuery(id+"F0.wireOp",EDGE,"E2.135.0"),sQuery(id+"F0.wireOp",EDGE,"E2.136.0"),sQuery(id+"F0.wireOp",EDGE,"E2.139.0"),sQuery(id+"F0.wireOp",EDGE,"E2.140.0"),sQuery(id+"F0.wireOp",EDGE,"E2.143.0"),sQuery(id+"F0.wireOp",EDGE,"E2.144.0"),sQuery(id+"F0.wireOp",EDGE,"E2.147.0"),sQuery(id+"F0.wireOp",EDGE,"E2.148.0"),sQuery(id+"F0.wireOp",EDGE,"E2.151.0"),sQuery(id+"F0.wireOp",EDGE,"E2.152.0"),sQuery(id+"F0.wireOp",EDGE,"E2.155.0"),sQuery(id+"F0.wireOp",EDGE,"E2.156.0"),sQuery(id+"F0.wireOp",EDGE,"E2.159.0"),sQuery(id+"F0.wireOp",EDGE,"E2.160.0"),sQuery(id+"F0.wireOp",EDGE,"E2.163.0"),sQuery(id+"F0.wireOp",EDGE,"E2.164.0"),sQuery(id+"F0.wireOp",EDGE,"E2.167.0"),sQuery(id+"F0.wireOp",EDGE,"E2.168.0"),sQuery(id+"F0.wireOp",EDGE,"E2.171.0"),sQuery(id+"F0.wireOp",EDGE,"E2.172.0"),sQuery(id+"F0.wireOp",EDGE,"E2.175.0"),sQuery(id+"F0.wireOp",EDGE,"E2.176.0"),sQuery(id+"F0.wireOp",EDGE,"E2.179.0"),sQuery(id+"F0.wireOp",EDGE,"E4.1.0"),sQuery(id+"F0.wireOp",EDGE,"E4.2.0"),sQuery(id+"F0.wireOp",EDGE,"E4.3.0"),sQuery(id+"F0.wireOp",EDGE,"E4.5.0"),sQuery(id+"F0.wireOp",EDGE,"E4.6.0"),sQuery(id+"F0.wireOp",EDGE,"E4.7.0"),sQuery(id+"F0.wireOp",EDGE,"E4.9.0"),sQuery(id+"F0.wireOp",EDGE,"E4.10.0"),sQuery(id+"F0.wireOp",EDGE,"E4.11.0"),sQuery(id+"F0.wireOp",EDGE,"E4.13.0"),sQuery(id+"F0.wireOp",EDGE,"E4.14.0"),sQuery(id+"F0.wireOp",EDGE,"E4.15.0"),sQuery(id+"F0.wireOp",EDGE,"E4.17.0"),sQuery(id+"F0.wireOp",EDGE,"E4.18.0"),sQuery(id+"F0.wireOp",EDGE,"E4.19.0"),sQuery(id+"F0.wireOp",EDGE,"E4.21.0"),sQuery(id+"F0.wireOp",EDGE,"E4.22.0"),sQuery(id+"F0.wireOp",EDGE,"E4.23.0"),sQuery(id+"F0.wireOp",EDGE,"E4.25.0"),sQuery(id+"F0.wireOp",EDGE,"E4.26.0"),sQuery(id+"F0.wireOp",EDGE,"E4.27.0"),sQuery(id+"F0.wireOp",EDGE,"E4.29.0"),sQuery(id+"F0.wireOp",EDGE,"E4.30.0"),sQuery(id+"F0.wireOp",EDGE,"E4.31.0"),sQuery(id+"F0.wireOp",EDGE,"E4.33.0"),sQuery(id+"F0.wireOp",EDGE,"E4.34.0"),sQuery(id+"F0.wireOp",EDGE,"E4.35.0"),sQuery(id+"F0.wireOp",EDGE,"E4.37.0"),sQuery(id+"F0.wireOp",EDGE,"E4.38.0"),sQuery(id+"F0.wireOp",EDGE,"E4.39.0"),sQuery(id+"F0.wireOp",EDGE,"E4.41.0"),sQuery(id+"F0.wireOp",EDGE,"E4.42.0"),sQuery(id+"F0.wireOp",EDGE,"E4.43.0"),sQuery(id+"F0.wireOp",EDGE,"E4.45.0"),sQuery(id+"F0.wireOp",EDGE,"E4.46.0"),sQuery(id+"F0.wireOp",EDGE,"E4.47.0"),sQuery(id+"F0.wireOp",EDGE,"E4.49.0"),sQuery(id+"F0.wireOp",EDGE,"E4.50.0"),sQuery(id+"F0.wireOp",EDGE,"E4.51.0"),sQuery(id+"F0.wireOp",EDGE,"E4.53.0"),sQuery(id+"F0.wireOp",EDGE,"E4.54.0"),sQuery(id+"F0.wireOp",EDGE,"E4.55.0"),sQuery(id+"F0.wireOp",EDGE,"E4.57.0"),sQuery(id+"F0.wireOp",EDGE,"E4.58.0"),sQuery(id+"F0.wireOp",EDGE,"E4.59.0"),sQuery(id+"F0.wireOp",EDGE,"E4.61.0"),sQuery(id+"F0.wireOp",EDGE,"E4.62.0"),sQuery(id+"F0.wireOp",EDGE,"E4.63.0"),sQuery(id+"F0.wireOp",EDGE,"E4.65.0"),sQuery(id+"F0.wireOp",EDGE,"E4.66.0"),sQuery(id+"F0.wireOp",EDGE,"E4.67.0"),sQuery(id+"F0.wireOp",EDGE,"E4.69.0"),sQuery(id+"F0.wireOp",EDGE,"E4.70.0"),sQuery(id+"F0.wireOp",EDGE,"E4.71.0"),sQuery(id+"F0.wireOp",EDGE,"E4.73.0"),sQuery(id+"F0.wireOp",EDGE,"E4.74.0"),sQuery(id+"F0.wireOp",EDGE,"E4.75.0"),sQuery(id+"F0.wireOp",EDGE,"E4.77.0"),sQuery(id+"F0.wireOp",EDGE,"E4.78.0"),sQuery(id+"F0.wireOp",EDGE,"E4.79.0"),sQuery(id+"F0.wireOp",EDGE,"E4.81.0"),sQuery(id+"F0.wireOp",EDGE,"E4.82.0"),sQuery(id+"F0.wireOp",EDGE,"E4.83.0"),sQuery(id+"F0.wireOp",EDGE,"E4.85.0"),sQuery(id+"F0.wireOp",EDGE,"E4.86.0"),sQuery(id+"F0.wireOp",EDGE,"E4.87.0"),sQuery(id+"F0.wireOp",EDGE,"E4.89.0"),sQuery(id+"F0.wireOp",EDGE,"E4.90.0"),sQuery(id+"F0.wireOp",EDGE,"E4.91.0"),sQuery(id+"F0.wireOp",EDGE,"E4.93.0"),sQuery(id+"F0.wireOp",EDGE,"E4.94.0"),sQuery(id+"F0.wireOp",EDGE,"E4.95.0"),sQuery(id+"F0.wireOp",EDGE,"E4.97.0"),sQuery(id+"F0.wireOp",EDGE,"E4.98.0"),sQuery(id+"F0.wireOp",EDGE,"E4.99.0"),sQuery(id+"F0.wireOp",EDGE,"E4.101.0"),sQuery(id+"F0.wireOp",EDGE,"E4.102.0"),sQuery(id+"F0.wireOp",EDGE,"E4.103.0"),sQuery(id+"F0.wireOp",EDGE,"E4.105.0"),sQuery(id+"F0.wireOp",EDGE,"E4.106.0"),sQuery(id+"F0.wireOp",EDGE,"E4.107.0"),sQuery(id+"F0.wireOp",EDGE,"E4.109.0"),sQuery(id+"F0.wireOp",EDGE,"E4.110.0"),sQuery(id+"F0.wireOp",EDGE,"E4.111.0"),sQuery(id+"F0.wireOp",EDGE,"E4.113.0"),sQuery(id+"F0.wireOp",EDGE,"E4.114.0"),sQuery(id+"F0.wireOp",EDGE,"E4.115.0"),sQuery(id+"F0.wireOp",EDGE,"E4.117.0"),sQuery(id+"F0.wireOp",EDGE,"E4.118.0"),sQuery(id+"F0.wireOp",EDGE,"E4.119.0"),sQuery(id+"F0.wireOp",EDGE,"E4.121.0"),sQuery(id+"F0.wireOp",EDGE,"E4.122.0"),sQuery(id+"F0.wireOp",EDGE,"E4.123.0"),sQuery(id+"F0.wireOp",EDGE,"E4.125.0"),sQuery(id+"F0.wireOp",EDGE,"E4.126.0"),sQuery(id+"F0.wireOp",EDGE,"E4.127.0"),sQuery(id+"F0.wireOp",EDGE,"E4.129.0"),sQuery(id+"F0.wireOp",EDGE,"E4.130.0"),sQuery(id+"F0.wireOp",EDGE,"E4.131.0"),sQuery(id+"F0.wireOp",EDGE,"E4.133.0"),sQuery(id+"F0.wireOp",EDGE,"E4.134.0"),sQuery(id+"F0.wireOp",EDGE,"E4.135.0"),sQuery(id+"F0.wireOp",EDGE,"E4.137.0"),sQuery(id+"F0.wireOp",EDGE,"E4.138.0"),sQuery(id+"F0.wireOp",EDGE,"E4.139.0"),sQuery(id+"F0.wireOp",EDGE,"E4.141.0"),sQuery(id+"F0.wireOp",EDGE,"E4.142.0"),sQuery(id+"F0.wireOp",EDGE,"E4.143.0"),sQuery(id+"F0.wireOp",EDGE,"E4.145.0"),sQuery(id+"F0.wireOp",EDGE,"E4.146.0"),sQuery(id+"F0.wireOp",EDGE,"E4.147.0"),sQuery(id+"F0.wireOp",EDGE,"E4.149.0"),sQuery(id+"F0.wireOp",EDGE,"E4.150.0"),sQuery(id+"F0.wireOp",EDGE,"E4.151.0"),sQuery(id+"F0.wireOp",EDGE,"E4.153.0"),sQuery(id+"F0.wireOp",EDGE,"E4.154.0"),sQuery(id+"F0.wireOp",EDGE,"E4.155.0"),sQuery(id+"F0.wireOp",EDGE,"E4.157.0"),sQuery(id+"F0.wireOp",EDGE,"E4.158.0"),sQuery(id+"F0.wireOp",EDGE,"E4.159.0"),sQuery(id+"F0.wireOp",EDGE,"E4.161.0"),sQuery(id+"F0.wireOp",EDGE,"E4.162.0"),sQuery(id+"F0.wireOp",EDGE,"E4.163.0"),sQuery(id+"F0.wireOp",EDGE,"E4.165.0"),sQuery(id+"F0.wireOp",EDGE,"E4.166.0"),sQuery(id+"F0.wireOp",EDGE,"E4.167.0"),sQuery(id+"F0.wireOp",EDGE,"E4.169.0"),sQuery(id+"F0.wireOp",EDGE,"E4.170.0"),sQuery(id+"F0.wireOp",EDGE,"E4.171.0"),sQuery(id+"F0.wireOp",EDGE,"E4.173.0"),sQuery(id+"F0.wireOp",EDGE,"E4.174.0"),sQuery(id+"F0.wireOp",EDGE,"E4.175.0"),sQuery(id+"F0.wireOp",EDGE,"E4.177.0"),sQuery(id+"F0.wireOp",EDGE,"E4.178.0"),sQuery(id+"F0.wireOp",EDGE,"E4.179.0"),sQuery(id+"F0.wireOp",EDGE,"E5"),sQuery(id+"F0.wireOp",EDGE,"E6.1.0"),sQuery(id+"F0.wireOp",EDGE,"E6.2.0"),sQuery(id+"F0.wireOp",EDGE,"E6.3.0"),sQuery(id+"F0.wireOp",EDGE,"E6.4.0"),sQuery(id+"F0.wireOp",EDGE,"E6.5.0"),sQuery(id+"F0.wireOp",EDGE,"E6.6.0"),sQuery(id+"F0.wireOp",EDGE,"E6.7.0"),sQuery(id+"F0.wireOp",EDGE,"E6.8.0"),sQuery(id+"F0.wireOp",EDGE,"E6.9.0"),sQuery(id+"F0.wireOp",EDGE,"E6.10.0"),sQuery(id+"F0.wireOp",EDGE,"E6.11.0"),sQuery(id+"F0.wireOp",EDGE,"E6.12.0"),sQuery(id+"F0.wireOp",EDGE,"E6.13.0"),sQuery(id+"F0.wireOp",EDGE,"E6.14.0"),sQuery(id+"F0.wireOp",EDGE,"E6.15.0"),sQuery(id+"F0.wireOp",EDGE,"E6.16.0"),sQuery(id+"F0.wireOp",EDGE,"E6.17.0"),sQuery(id+"F0.wireOp",EDGE,"E6.18.0"),sQuery(id+"F0.wireOp",EDGE,"E6.19.0"),sQuery(id+"F0.wireOp",EDGE,"E6.20.0"),sQuery(id+"F0.wireOp",EDGE,"E6.21.0"),sQuery(id+"F0.wireOp",EDGE,"E6.22.0"),sQuery(id+"F0.wireOp",EDGE,"E6.23.0"),sQuery(id+"F0.wireOp",EDGE,"E6.24.0"),sQuery(id+"F0.wireOp",EDGE,"E6.25.0"),sQuery(id+"F0.wireOp",EDGE,"E6.26.0"),sQuery(id+"F0.wireOp",EDGE,"E6.27.0"),sQuery(id+"F0.wireOp",EDGE,"E6.28.0"),sQuery(id+"F0.wireOp",EDGE,"E6.29.0"),sQuery(id+"F0.wireOp",EDGE,"E6.30.0"),sQuery(id+"F0.wireOp",EDGE,"E6.31.0"),sQuery(id+"F0.wireOp",EDGE,"E6.32.0"),sQuery(id+"F0.wireOp",EDGE,"E6.33.0"),sQuery(id+"F0.wireOp",EDGE,"E6.34.0"),sQuery(id+"F0.wireOp",EDGE,"E6.35.0"),sQuery(id+"F0.wireOp",EDGE,"E6.36.0"),sQuery(id+"F0.wireOp",EDGE,"E6.37.0"),sQuery(id+"F0.wireOp",EDGE,"E6.38.0"),sQuery(id+"F0.wireOp",EDGE,"E6.39.0"),sQuery(id+"F0.wireOp",EDGE,"E6.40.0"),sQuery(id+"F0.wireOp",EDGE,"E6.41.0"),sQuery(id+"F0.wireOp",EDGE,"E6.42.0"),sQuery(id+"F0.wireOp",EDGE,"E6.43.0"),sQuery(id+"F0.wireOp",EDGE,"E6.44.0"),sQuery(id+"F0.wireOp",EDGE,"E7")])]});
            var Q1;
            Q1=makeQuery(id+"F5.opExtrude","SWEPT_BODY",BODY,{"disambiguationData":[OSD([sQuery(id+"F4.wireOp",EDGE,"E10"),sQuery(id+"F4.wireOp",EDGE,"E11.5.0"),sQuery(id+"F4.wireOp",EDGE,"E11.10.0"),sQuery(id+"F4.wireOp",EDGE,"E11.20.0"),sQuery(id+"F4.wireOp",EDGE,"E11.25.0"),sQuery(id+"F4.wireOp",EDGE,"E11.30.0"),sQuery(id+"F4.wireOp",EDGE,"E11.35.0"),sQuery(id+"F4.wireOp",EDGE,"E11.40.0"),sQuery(id+"F4.wireOp",EDGE,"E13.2.0"),sQuery(id+"F4.wireOp",EDGE,"E13.3.0"),sQuery(id+"F4.wireOp",EDGE,"E13.7.0"),sQuery(id+"F4.wireOp",EDGE,"E13.8.0"),sQuery(id+"F4.wireOp",EDGE,"E13.12.0"),sQuery(id+"F4.wireOp",EDGE,"E13.13.0"),sQuery(id+"F4.wireOp",EDGE,"E14.1.17.0"),sQuery(id+"F4.wireOp",EDGE,"E14.1.18.0"),sQuery(id+"F4.wireOp",EDGE,"E14.1.22.0"),sQuery(id+"F4.wireOp",EDGE,"E14.1.23.0"),sQuery(id+"F4.wireOp",EDGE,"E14.1.27.0"),sQuery(id+"F4.wireOp",EDGE,"E14.1.28.0"),sQuery(id+"F4.wireOp",EDGE,"E15.1.32.0"),sQuery(id+"F4.wireOp",EDGE,"E15.1.33.0"),sQuery(id+"F4.wireOp",EDGE,"E15.1.37.0"),sQuery(id+"F4.wireOp",EDGE,"E15.1.38.0"),sQuery(id+"F4.wireOp",EDGE,"E15.1.42.0"),sQuery(id+"F4.wireOp",EDGE,"E15.1.43.0"),sQuery(id+"F4.wireOp",EDGE,"E16"),sQuery(id+"F4.wireOp",EDGE,"E17"),sQuery(id+"F4.wireOp",EDGE,"E18"),sQuery(id+"F4.wireOp",EDGE,"E19"),sQuery(id+"F4.wireOp",EDGE,"E20"),sQuery(id+"F4.wireOp",EDGE,"E21"),sQuery(id+"F4.wireOp",EDGE,"E22"),sQuery(id+"F4.wireOp",EDGE,"E23"),sQuery(id+"F4.wireOp",EDGE,"E24"),sQuery(id+"F4.wireOp",EDGE,"E25"),sQuery(id+"F4.wireOp",EDGE,"E26"),sQuery(id+"F4.wireOp",EDGE,"E27"),sQuery(id+"F4.wireOp",EDGE,"E28"),sQuery(id+"F4.wireOp",EDGE,"E29"),sQuery(id+"F4.wireOp",EDGE,"E30"),sQuery(id+"F4.wireOp",EDGE,"E31"),sQuery(id+"F4.wireOp",EDGE,"E32"),sQuery(id+"F4.wireOp",EDGE,"E33"),sQuery(id+"F4.wireOp",EDGE,"E34")])]});
            var Q2;
            Q2=makeQuery(id+"F13.opPattern","COPY",BODY,{"derivedFrom":makeQuery(id+"F1.opExtrude","SWEPT_BODY",BODY,{"disambiguationData":[OSD([sQuery(id+"F0.wireOp",EDGE,"E1"),sQuery(id+"F0.wireOp",EDGE,"E2.3.0"),sQuery(id+"F0.wireOp",EDGE,"E2.4.0"),sQuery(id+"F0.wireOp",EDGE,"E2.7.0"),sQuery(id+"F0.wireOp",EDGE,"E2.8.0"),sQuery(id+"F0.wireOp",EDGE,"E2.11.0"),sQuery(id+"F0.wireOp",EDGE,"E2.12.0"),sQuery(id+"F0.wireOp",EDGE,"E2.15.0"),sQuery(id+"F0.wireOp",EDGE,"E2.16.0"),sQuery(id+"F0.wireOp",EDGE,"E2.19.0"),sQuery(id+"F0.wireOp",EDGE,"E2.20.0"),sQuery(id+"F0.wireOp",EDGE,"E2.23.0"),sQuery(id+"F0.wireOp",EDGE,"E2.24.0"),sQuery(id+"F0.wireOp",EDGE,"E2.27.0"),sQuery(id+"F0.wireOp",EDGE,"E2.28.0"),sQuery(id+"F0.wireOp",EDGE,"E2.31.0"),sQuery(id+"F0.wireOp",EDGE,"E2.32.0"),sQuery(id+"F0.wireOp",EDGE,"E2.35.0"),sQuery(id+"F0.wireOp",EDGE,"E2.36.0"),sQuery(id+"F0.wireOp",EDGE,"E2.39.0"),sQuery(id+"F0.wireOp",EDGE,"E2.40.0"),sQuery(id+"F0.wireOp",EDGE,"E2.43.0"),sQuery(id+"F0.wireOp",EDGE,"E2.44.0"),sQuery(id+"F0.wireOp",EDGE,"E2.47.0"),sQuery(id+"F0.wireOp",EDGE,"E2.48.0"),sQuery(id+"F0.wireOp",EDGE,"E2.51.0"),sQuery(id+"F0.wireOp",EDGE,"E2.52.0"),sQuery(id+"F0.wireOp",EDGE,"E2.55.0"),sQuery(id+"F0.wireOp",EDGE,"E2.56.0"),sQuery(id+"F0.wireOp",EDGE,"E2.59.0"),sQuery(id+"F0.wireOp",EDGE,"E2.60.0"),sQuery(id+"F0.wireOp",EDGE,"E2.63.0"),sQuery(id+"F0.wireOp",EDGE,"E2.64.0"),sQuery(id+"F0.wireOp",EDGE,"E2.67.0"),sQuery(id+"F0.wireOp",EDGE,"E2.68.0"),sQuery(id+"F0.wireOp",EDGE,"E2.71.0"),sQuery(id+"F0.wireOp",EDGE,"E2.72.0"),sQuery(id+"F0.wireOp",EDGE,"E2.75.0"),sQuery(id+"F0.wireOp",EDGE,"E2.76.0"),sQuery(id+"F0.wireOp",EDGE,"E2.79.0"),sQuery(id+"F0.wireOp",EDGE,"E2.80.0"),sQuery(id+"F0.wireOp",EDGE,"E2.83.0"),sQuery(id+"F0.wireOp",EDGE,"E2.84.0"),sQuery(id+"F0.wireOp",EDGE,"E2.87.0"),sQuery(id+"F0.wireOp",EDGE,"E2.88.0"),sQuery(id+"F0.wireOp",EDGE,"E2.91.0"),sQuery(id+"F0.wireOp",EDGE,"E2.92.0"),sQuery(id+"F0.wireOp",EDGE,"E2.95.0"),sQuery(id+"F0.wireOp",EDGE,"E2.96.0"),sQuery(id+"F0.wireOp",EDGE,"E2.99.0"),sQuery(id+"F0.wireOp",EDGE,"E2.100.0"),sQuery(id+"F0.wireOp",EDGE,"E2.103.0"),sQuery(id+"F0.wireOp",EDGE,"E2.104.0"),sQuery(id+"F0.wireOp",EDGE,"E2.107.0"),sQuery(id+"F0.wireOp",EDGE,"E2.108.0"),sQuery(id+"F0.wireOp",EDGE,"E2.111.0"),sQuery(id+"F0.wireOp",EDGE,"E2.112.0"),sQuery(id+"F0.wireOp",EDGE,"E2.115.0"),sQuery(id+"F0.wireOp",EDGE,"E2.116.0"),sQuery(id+"F0.wireOp",EDGE,"E2.119.0"),sQuery(id+"F0.wireOp",EDGE,"E2.120.0"),sQuery(id+"F0.wireOp",EDGE,"E2.123.0"),sQuery(id+"F0.wireOp",EDGE,"E2.124.0"),sQuery(id+"F0.wireOp",EDGE,"E2.127.0"),sQuery(id+"F0.wireOp",EDGE,"E2.128.0"),sQuery(id+"F0.wireOp",EDGE,"E2.131.0"),sQuery(id+"F0.wireOp",EDGE,"E2.132.0"),sQuery(id+"F0.wireOp",EDGE,"E2.135.0"),sQuery(id+"F0.wireOp",EDGE,"E2.136.0"),sQuery(id+"F0.wireOp",EDGE,"E2.139.0"),sQuery(id+"F0.wireOp",EDGE,"E2.140.0"),sQuery(id+"F0.wireOp",EDGE,"E2.143.0"),sQuery(id+"F0.wireOp",EDGE,"E2.144.0"),sQuery(id+"F0.wireOp",EDGE,"E2.147.0"),sQuery(id+"F0.wireOp",EDGE,"E2.148.0"),sQuery(id+"F0.wireOp",EDGE,"E2.151.0"),sQuery(id+"F0.wireOp",EDGE,"E2.152.0"),sQuery(id+"F0.wireOp",EDGE,"E2.155.0"),sQuery(id+"F0.wireOp",EDGE,"E2.156.0"),sQuery(id+"F0.wireOp",EDGE,"E2.159.0"),sQuery(id+"F0.wireOp",EDGE,"E2.160.0"),sQuery(id+"F0.wireOp",EDGE,"E2.163.0"),sQuery(id+"F0.wireOp",EDGE,"E2.164.0"),sQuery(id+"F0.wireOp",EDGE,"E2.167.0"),sQuery(id+"F0.wireOp",EDGE,"E2.168.0"),sQuery(id+"F0.wireOp",EDGE,"E2.171.0"),sQuery(id+"F0.wireOp",EDGE,"E2.172.0"),sQuery(id+"F0.wireOp",EDGE,"E2.175.0"),sQuery(id+"F0.wireOp",EDGE,"E2.176.0"),sQuery(id+"F0.wireOp",EDGE,"E2.179.0"),sQuery(id+"F0.wireOp",EDGE,"E4.1.0"),sQuery(id+"F0.wireOp",EDGE,"E4.2.0"),sQuery(id+"F0.wireOp",EDGE,"E4.3.0"),sQuery(id+"F0.wireOp",EDGE,"E4.5.0"),sQuery(id+"F0.wireOp",EDGE,"E4.6.0"),sQuery(id+"F0.wireOp",EDGE,"E4.7.0"),sQuery(id+"F0.wireOp",EDGE,"E4.9.0"),sQuery(id+"F0.wireOp",EDGE,"E4.10.0"),sQuery(id+"F0.wireOp",EDGE,"E4.11.0"),sQuery(id+"F0.wireOp",EDGE,"E4.13.0"),sQuery(id+"F0.wireOp",EDGE,"E4.14.0"),sQuery(id+"F0.wireOp",EDGE,"E4.15.0"),sQuery(id+"F0.wireOp",EDGE,"E4.17.0"),sQuery(id+"F0.wireOp",EDGE,"E4.18.0"),sQuery(id+"F0.wireOp",EDGE,"E4.19.0"),sQuery(id+"F0.wireOp",EDGE,"E4.21.0"),sQuery(id+"F0.wireOp",EDGE,"E4.22.0"),sQuery(id+"F0.wireOp",EDGE,"E4.23.0"),sQuery(id+"F0.wireOp",EDGE,"E4.25.0"),sQuery(id+"F0.wireOp",EDGE,"E4.26.0"),sQuery(id+"F0.wireOp",EDGE,"E4.27.0"),sQuery(id+"F0.wireOp",EDGE,"E4.29.0"),sQuery(id+"F0.wireOp",EDGE,"E4.30.0"),sQuery(id+"F0.wireOp",EDGE,"E4.31.0"),sQuery(id+"F0.wireOp",EDGE,"E4.33.0"),sQuery(id+"F0.wireOp",EDGE,"E4.34.0"),sQuery(id+"F0.wireOp",EDGE,"E4.35.0"),sQuery(id+"F0.wireOp",EDGE,"E4.37.0"),sQuery(id+"F0.wireOp",EDGE,"E4.38.0"),sQuery(id+"F0.wireOp",EDGE,"E4.39.0"),sQuery(id+"F0.wireOp",EDGE,"E4.41.0"),sQuery(id+"F0.wireOp",EDGE,"E4.42.0"),sQuery(id+"F0.wireOp",EDGE,"E4.43.0"),sQuery(id+"F0.wireOp",EDGE,"E4.45.0"),sQuery(id+"F0.wireOp",EDGE,"E4.46.0"),sQuery(id+"F0.wireOp",EDGE,"E4.47.0"),sQuery(id+"F0.wireOp",EDGE,"E4.49.0"),sQuery(id+"F0.wireOp",EDGE,"E4.50.0"),sQuery(id+"F0.wireOp",EDGE,"E4.51.0"),sQuery(id+"F0.wireOp",EDGE,"E4.53.0"),sQuery(id+"F0.wireOp",EDGE,"E4.54.0"),sQuery(id+"F0.wireOp",EDGE,"E4.55.0"),sQuery(id+"F0.wireOp",EDGE,"E4.57.0"),sQuery(id+"F0.wireOp",EDGE,"E4.58.0"),sQuery(id+"F0.wireOp",EDGE,"E4.59.0"),sQuery(id+"F0.wireOp",EDGE,"E4.61.0"),sQuery(id+"F0.wireOp",EDGE,"E4.62.0"),sQuery(id+"F0.wireOp",EDGE,"E4.63.0"),sQuery(id+"F0.wireOp",EDGE,"E4.65.0"),sQuery(id+"F0.wireOp",EDGE,"E4.66.0"),sQuery(id+"F0.wireOp",EDGE,"E4.67.0"),sQuery(id+"F0.wireOp",EDGE,"E4.69.0"),sQuery(id+"F0.wireOp",EDGE,"E4.70.0"),sQuery(id+"F0.wireOp",EDGE,"E4.71.0"),sQuery(id+"F0.wireOp",EDGE,"E4.73.0"),sQuery(id+"F0.wireOp",EDGE,"E4.74.0"),sQuery(id+"F0.wireOp",EDGE,"E4.75.0"),sQuery(id+"F0.wireOp",EDGE,"E4.77.0"),sQuery(id+"F0.wireOp",EDGE,"E4.78.0"),sQuery(id+"F0.wireOp",EDGE,"E4.79.0"),sQuery(id+"F0.wireOp",EDGE,"E4.81.0"),sQuery(id+"F0.wireOp",EDGE,"E4.82.0"),sQuery(id+"F0.wireOp",EDGE,"E4.83.0"),sQuery(id+"F0.wireOp",EDGE,"E4.85.0"),sQuery(id+"F0.wireOp",EDGE,"E4.86.0"),sQuery(id+"F0.wireOp",EDGE,"E4.87.0"),sQuery(id+"F0.wireOp",EDGE,"E4.89.0"),sQuery(id+"F0.wireOp",EDGE,"E4.90.0"),sQuery(id+"F0.wireOp",EDGE,"E4.91.0"),sQuery(id+"F0.wireOp",EDGE,"E4.93.0"),sQuery(id+"F0.wireOp",EDGE,"E4.94.0"),sQuery(id+"F0.wireOp",EDGE,"E4.95.0"),sQuery(id+"F0.wireOp",EDGE,"E4.97.0"),sQuery(id+"F0.wireOp",EDGE,"E4.98.0"),sQuery(id+"F0.wireOp",EDGE,"E4.99.0"),sQuery(id+"F0.wireOp",EDGE,"E4.101.0"),sQuery(id+"F0.wireOp",EDGE,"E4.102.0"),sQuery(id+"F0.wireOp",EDGE,"E4.103.0"),sQuery(id+"F0.wireOp",EDGE,"E4.105.0"),sQuery(id+"F0.wireOp",EDGE,"E4.106.0"),sQuery(id+"F0.wireOp",EDGE,"E4.107.0"),sQuery(id+"F0.wireOp",EDGE,"E4.109.0"),sQuery(id+"F0.wireOp",EDGE,"E4.110.0"),sQuery(id+"F0.wireOp",EDGE,"E4.111.0"),sQuery(id+"F0.wireOp",EDGE,"E4.113.0"),sQuery(id+"F0.wireOp",EDGE,"E4.114.0"),sQuery(id+"F0.wireOp",EDGE,"E4.115.0"),sQuery(id+"F0.wireOp",EDGE,"E4.117.0"),sQuery(id+"F0.wireOp",EDGE,"E4.118.0"),sQuery(id+"F0.wireOp",EDGE,"E4.119.0"),sQuery(id+"F0.wireOp",EDGE,"E4.121.0"),sQuery(id+"F0.wireOp",EDGE,"E4.122.0"),sQuery(id+"F0.wireOp",EDGE,"E4.123.0"),sQuery(id+"F0.wireOp",EDGE,"E4.125.0"),sQuery(id+"F0.wireOp",EDGE,"E4.126.0"),sQuery(id+"F0.wireOp",EDGE,"E4.127.0"),sQuery(id+"F0.wireOp",EDGE,"E4.129.0"),sQuery(id+"F0.wireOp",EDGE,"E4.130.0"),sQuery(id+"F0.wireOp",EDGE,"E4.131.0"),sQuery(id+"F0.wireOp",EDGE,"E4.133.0"),sQuery(id+"F0.wireOp",EDGE,"E4.134.0"),sQuery(id+"F0.wireOp",EDGE,"E4.135.0"),sQuery(id+"F0.wireOp",EDGE,"E4.137.0"),sQuery(id+"F0.wireOp",EDGE,"E4.138.0"),sQuery(id+"F0.wireOp",EDGE,"E4.139.0"),sQuery(id+"F0.wireOp",EDGE,"E4.141.0"),sQuery(id+"F0.wireOp",EDGE,"E4.142.0"),sQuery(id+"F0.wireOp",EDGE,"E4.143.0"),sQuery(id+"F0.wireOp",EDGE,"E4.145.0"),sQuery(id+"F0.wireOp",EDGE,"E4.146.0"),sQuery(id+"F0.wireOp",EDGE,"E4.147.0"),sQuery(id+"F0.wireOp",EDGE,"E4.149.0"),sQuery(id+"F0.wireOp",EDGE,"E4.150.0"),sQuery(id+"F0.wireOp",EDGE,"E4.151.0"),sQuery(id+"F0.wireOp",EDGE,"E4.153.0"),sQuery(id+"F0.wireOp",EDGE,"E4.154.0"),sQuery(id+"F0.wireOp",EDGE,"E4.155.0"),sQuery(id+"F0.wireOp",EDGE,"E4.157.0"),sQuery(id+"F0.wireOp",EDGE,"E4.158.0"),sQuery(id+"F0.wireOp",EDGE,"E4.159.0"),sQuery(id+"F0.wireOp",EDGE,"E4.161.0"),sQuery(id+"F0.wireOp",EDGE,"E4.162.0"),sQuery(id+"F0.wireOp",EDGE,"E4.163.0"),sQuery(id+"F0.wireOp",EDGE,"E4.165.0"),sQuery(id+"F0.wireOp",EDGE,"E4.166.0"),sQuery(id+"F0.wireOp",EDGE,"E4.167.0"),sQuery(id+"F0.wireOp",EDGE,"E4.169.0"),sQuery(id+"F0.wireOp",EDGE,"E4.170.0"),sQuery(id+"F0.wireOp",EDGE,"E4.171.0"),sQuery(id+"F0.wireOp",EDGE,"E4.173.0"),sQuery(id+"F0.wireOp",EDGE,"E4.174.0"),sQuery(id+"F0.wireOp",EDGE,"E4.175.0"),sQuery(id+"F0.wireOp",EDGE,"E4.177.0"),sQuery(id+"F0.wireOp",EDGE,"E4.178.0"),sQuery(id+"F0.wireOp",EDGE,"E4.179.0"),sQuery(id+"F0.wireOp",EDGE,"E5"),sQuery(id+"F0.wireOp",EDGE,"E6.1.0"),sQuery(id+"F0.wireOp",EDGE,"E6.2.0"),sQuery(id+"F0.wireOp",EDGE,"E6.3.0"),sQuery(id+"F0.wireOp",EDGE,"E6.4.0"),sQuery(id+"F0.wireOp",EDGE,"E6.5.0"),sQuery(id+"F0.wireOp",EDGE,"E6.6.0"),sQuery(id+"F0.wireOp",EDGE,"E6.7.0"),sQuery(id+"F0.wireOp",EDGE,"E6.8.0"),sQuery(id+"F0.wireOp",EDGE,"E6.9.0"),sQuery(id+"F0.wireOp",EDGE,"E6.10.0"),sQuery(id+"F0.wireOp",EDGE,"E6.11.0"),sQuery(id+"F0.wireOp",EDGE,"E6.12.0"),sQuery(id+"F0.wireOp",EDGE,"E6.13.0"),sQuery(id+"F0.wireOp",EDGE,"E6.14.0"),sQuery(id+"F0.wireOp",EDGE,"E6.15.0"),sQuery(id+"F0.wireOp",EDGE,"E6.16.0"),sQuery(id+"F0.wireOp",EDGE,"E6.17.0"),sQuery(id+"F0.wireOp",EDGE,"E6.18.0"),sQuery(id+"F0.wireOp",EDGE,"E6.19.0"),sQuery(id+"F0.wireOp",EDGE,"E6.20.0"),sQuery(id+"F0.wireOp",EDGE,"E6.21.0"),sQuery(id+"F0.wireOp",EDGE,"E6.22.0"),sQuery(id+"F0.wireOp",EDGE,"E6.23.0"),sQuery(id+"F0.wireOp",EDGE,"E6.24.0"),sQuery(id+"F0.wireOp",EDGE,"E6.25.0"),sQuery(id+"F0.wireOp",EDGE,"E6.26.0"),sQuery(id+"F0.wireOp",EDGE,"E6.27.0"),sQuery(id+"F0.wireOp",EDGE,"E6.28.0"),sQuery(id+"F0.wireOp",EDGE,"E6.29.0"),sQuery(id+"F0.wireOp",EDGE,"E6.30.0"),sQuery(id+"F0.wireOp",EDGE,"E6.31.0"),sQuery(id+"F0.wireOp",EDGE,"E6.32.0"),sQuery(id+"F0.wireOp",EDGE,"E6.33.0"),sQuery(id+"F0.wireOp",EDGE,"E6.34.0"),sQuery(id+"F0.wireOp",EDGE,"E6.35.0"),sQuery(id+"F0.wireOp",EDGE,"E6.36.0"),sQuery(id+"F0.wireOp",EDGE,"E6.37.0"),sQuery(id+"F0.wireOp",EDGE,"E6.38.0"),sQuery(id+"F0.wireOp",EDGE,"E6.39.0"),sQuery(id+"F0.wireOp",EDGE,"E6.40.0"),sQuery(id+"F0.wireOp",EDGE,"E6.41.0"),sQuery(id+"F0.wireOp",EDGE,"E6.42.0"),sQuery(id+"F0.wireOp",EDGE,"E6.43.0"),sQuery(id+"F0.wireOp",EDGE,"E6.44.0"),sQuery(id+"F0.wireOp",EDGE,"E7")])]}),"instanceName":"1"});
            var Q3;
            Q3=makeQuery(id+"F12.opExtrude","SWEPT_BODY",BODY,{"disambiguationData":[OSD([sQuery(id+"F11.wireOp",EDGE,"E36")])]});
            var Q4;
            Q4=makeQuery(id+"F15.opPattern","COPY",BODY,{"derivedFrom":makeQuery(id+"F10.opPattern","COPY",BODY,{"derivedFrom":makeQuery(id+"F5.opExtrude","SWEPT_BODY",BODY,{"disambiguationData":[OSD([sQuery(id+"F4.wireOp",EDGE,"E10"),sQuery(id+"F4.wireOp",EDGE,"E11.5.0"),sQuery(id+"F4.wireOp",EDGE,"E11.10.0"),sQuery(id+"F4.wireOp",EDGE,"E11.20.0"),sQuery(id+"F4.wireOp",EDGE,"E11.25.0"),sQuery(id+"F4.wireOp",EDGE,"E11.30.0"),sQuery(id+"F4.wireOp",EDGE,"E11.35.0"),sQuery(id+"F4.wireOp",EDGE,"E11.40.0"),sQuery(id+"F4.wireOp",EDGE,"E13.2.0"),sQuery(id+"F4.wireOp",EDGE,"E13.3.0"),sQuery(id+"F4.wireOp",EDGE,"E13.7.0"),sQuery(id+"F4.wireOp",EDGE,"E13.8.0"),sQuery(id+"F4.wireOp",EDGE,"E13.12.0"),sQuery(id+"F4.wireOp",EDGE,"E13.13.0"),sQuery(id+"F4.wireOp",EDGE,"E14.1.17.0"),sQuery(id+"F4.wireOp",EDGE,"E14.1.18.0"),sQuery(id+"F4.wireOp",EDGE,"E14.1.22.0"),sQuery(id+"F4.wireOp",EDGE,"E14.1.23.0"),sQuery(id+"F4.wireOp",EDGE,"E14.1.27.0"),sQuery(id+"F4.wireOp",EDGE,"E14.1.28.0"),sQuery(id+"F4.wireOp",EDGE,"E15.1.32.0"),sQuery(id+"F4.wireOp",EDGE,"E15.1.33.0"),sQuery(id+"F4.wireOp",EDGE,"E15.1.37.0"),sQuery(id+"F4.wireOp",EDGE,"E15.1.38.0"),sQuery(id+"F4.wireOp",EDGE,"E15.1.42.0"),sQuery(id+"F4.wireOp",EDGE,"E15.1.43.0"),sQuery(id+"F4.wireOp",EDGE,"E16"),sQuery(id+"F4.wireOp",EDGE,"E17"),sQuery(id+"F4.wireOp",EDGE,"E18"),sQuery(id+"F4.wireOp",EDGE,"E19"),sQuery(id+"F4.wireOp",EDGE,"E20"),sQuery(id+"F4.wireOp",EDGE,"E21"),sQuery(id+"F4.wireOp",EDGE,"E22"),sQuery(id+"F4.wireOp",EDGE,"E23"),sQuery(id+"F4.wireOp",EDGE,"E24"),sQuery(id+"F4.wireOp",EDGE,"E25"),sQuery(id+"F4.wireOp",EDGE,"E26"),sQuery(id+"F4.wireOp",EDGE,"E27"),sQuery(id+"F4.wireOp",EDGE,"E28"),sQuery(id+"F4.wireOp",EDGE,"E29"),sQuery(id+"F4.wireOp",EDGE,"E30"),sQuery(id+"F4.wireOp",EDGE,"E31"),sQuery(id+"F4.wireOp",EDGE,"E32"),sQuery(id+"F4.wireOp",EDGE,"E33"),sQuery(id+"F4.wireOp",EDGE,"E34")])]}),"instanceName":"1"}),"instanceName":"1"});
            var Q5;
            Q5=makeQuery(id+"F15.opPattern","COPY",BODY,{"derivedFrom":makeQuery(id+"F5.opExtrude","SWEPT_BODY",BODY,{"disambiguationData":[OSD([sQuery(id+"F4.wireOp",EDGE,"E10"),sQuery(id+"F4.wireOp",EDGE,"E11.5.0"),sQuery(id+"F4.wireOp",EDGE,"E11.10.0"),sQuery(id+"F4.wireOp",EDGE,"E11.20.0"),sQuery(id+"F4.wireOp",EDGE,"E11.25.0"),sQuery(id+"F4.wireOp",EDGE,"E11.30.0"),sQuery(id+"F4.wireOp",EDGE,"E11.35.0"),sQuery(id+"F4.wireOp",EDGE,"E11.40.0"),sQuery(id+"F4.wireOp",EDGE,"E13.2.0"),sQuery(id+"F4.wireOp",EDGE,"E13.3.0"),sQuery(id+"F4.wireOp",EDGE,"E13.7.0"),sQuery(id+"F4.wireOp",EDGE,"E13.8.0"),sQuery(id+"F4.wireOp",EDGE,"E13.12.0"),sQuery(id+"F4.wireOp",EDGE,"E13.13.0"),sQuery(id+"F4.wireOp",EDGE,"E14.1.17.0"),sQuery(id+"F4.wireOp",EDGE,"E14.1.18.0"),sQuery(id+"F4.wireOp",EDGE,"E14.1.22.0"),sQuery(id+"F4.wireOp",EDGE,"E14.1.23.0"),sQuery(id+"F4.wireOp",EDGE,"E14.1.27.0"),sQuery(id+"F4.wireOp",EDGE,"E14.1.28.0"),sQuery(id+"F4.wireOp",EDGE,"E15.1.32.0"),sQuery(id+"F4.wireOp",EDGE,"E15.1.33.0"),sQuery(id+"F4.wireOp",EDGE,"E15.1.37.0"),sQuery(id+"F4.wireOp",EDGE,"E15.1.38.0"),sQuery(id+"F4.wireOp",EDGE,"E15.1.42.0"),sQuery(id+"F4.wireOp",EDGE,"E15.1.43.0"),sQuery(id+"F4.wireOp",EDGE,"E16"),sQuery(id+"F4.wireOp",EDGE,"E17"),sQuery(id+"F4.wireOp",EDGE,"E18"),sQuery(id+"F4.wireOp",EDGE,"E19"),sQuery(id+"F4.wireOp",EDGE,"E20"),sQuery(id+"F4.wireOp",EDGE,"E21"),sQuery(id+"F4.wireOp",EDGE,"E22"),sQuery(id+"F4.wireOp",EDGE,"E23"),sQuery(id+"F4.wireOp",EDGE,"E24"),sQuery(id+"F4.wireOp",EDGE,"E25"),sQuery(id+"F4.wireOp",EDGE,"E26"),sQuery(id+"F4.wireOp",EDGE,"E27"),sQuery(id+"F4.wireOp",EDGE,"E28"),sQuery(id+"F4.wireOp",EDGE,"E29"),sQuery(id+"F4.wireOp",EDGE,"E30"),sQuery(id+"F4.wireOp",EDGE,"E31"),sQuery(id+"F4.wireOp",EDGE,"E32"),sQuery(id+"F4.wireOp",EDGE,"E33"),sQuery(id+"F4.wireOp",EDGE,"E34")])]}),"instanceName":"1"});
            var Q6;
            Q6=makeQuery(id+"F10.opPattern","COPY",BODY,{"derivedFrom":makeQuery(id+"F5.opExtrude","SWEPT_BODY",BODY,{"disambiguationData":[OSD([sQuery(id+"F4.wireOp",EDGE,"E10"),sQuery(id+"F4.wireOp",EDGE,"E11.5.0"),sQuery(id+"F4.wireOp",EDGE,"E11.10.0"),sQuery(id+"F4.wireOp",EDGE,"E11.20.0"),sQuery(id+"F4.wireOp",EDGE,"E11.25.0"),sQuery(id+"F4.wireOp",EDGE,"E11.30.0"),sQuery(id+"F4.wireOp",EDGE,"E11.35.0"),sQuery(id+"F4.wireOp",EDGE,"E11.40.0"),sQuery(id+"F4.wireOp",EDGE,"E13.2.0"),sQuery(id+"F4.wireOp",EDGE,"E13.3.0"),sQuery(id+"F4.wireOp",EDGE,"E13.7.0"),sQuery(id+"F4.wireOp",EDGE,"E13.8.0"),sQuery(id+"F4.wireOp",EDGE,"E13.12.0"),sQuery(id+"F4.wireOp",EDGE,"E13.13.0"),sQuery(id+"F4.wireOp",EDGE,"E14.1.17.0"),sQuery(id+"F4.wireOp",EDGE,"E14.1.18.0"),sQuery(id+"F4.wireOp",EDGE,"E14.1.22.0"),sQuery(id+"F4.wireOp",EDGE,"E14.1.23.0"),sQuery(id+"F4.wireOp",EDGE,"E14.1.27.0"),sQuery(id+"F4.wireOp",EDGE,"E14.1.28.0"),sQuery(id+"F4.wireOp",EDGE,"E15.1.32.0"),sQuery(id+"F4.wireOp",EDGE,"E15.1.33.0"),sQuery(id+"F4.wireOp",EDGE,"E15.1.37.0"),sQuery(id+"F4.wireOp",EDGE,"E15.1.38.0"),sQuery(id+"F4.wireOp",EDGE,"E15.1.42.0"),sQuery(id+"F4.wireOp",EDGE,"E15.1.43.0"),sQuery(id+"F4.wireOp",EDGE,"E16"),sQuery(id+"F4.wireOp",EDGE,"E17"),sQuery(id+"F4.wireOp",EDGE,"E18"),sQuery(id+"F4.wireOp",EDGE,"E19"),sQuery(id+"F4.wireOp",EDGE,"E20"),sQuery(id+"F4.wireOp",EDGE,"E21"),sQuery(id+"F4.wireOp",EDGE,"E22"),sQuery(id+"F4.wireOp",EDGE,"E23"),sQuery(id+"F4.wireOp",EDGE,"E24"),sQuery(id+"F4.wireOp",EDGE,"E25"),sQuery(id+"F4.wireOp",EDGE,"E26"),sQuery(id+"F4.wireOp",EDGE,"E27"),sQuery(id+"F4.wireOp",EDGE,"E28"),sQuery(id+"F4.wireOp",EDGE,"E29"),sQuery(id+"F4.wireOp",EDGE,"E30"),sQuery(id+"F4.wireOp",EDGE,"E31"),sQuery(id+"F4.wireOp",EDGE,"E32"),sQuery(id+"F4.wireOp",EDGE,"E33"),sQuery(id+"F4.wireOp",EDGE,"E34")])]}),"instanceName":"1"});
            var Q7;
            Q7=makeQuery(id+"F15.opPattern","COPY",EDGE,{"derivedFrom":makeQuery(id+"F10.opPattern","COPY",EDGE,{"derivedFrom":makeQuery(id+"F7.boolean.opBoolean","COPY",EDGE,{"derivedFrom":makeQuery(id+"F7.opExtrude","CAP_EDGE",EDGE,{"disambiguationData":[OSD([sQuery(id+"F6.wireOp",EDGE,"E35")])],"isStart":true})}),"instanceName":"1"}),"instanceName":"1"});
            transform(context, id + "F21", {"entities" : qUnion([Q0, Q1, Q2, Q3, Q4, Q5, Q6]), "transformType" : TransformType.TRANSLATION_3D, "dx" : 0 * mm, "dy" : 151.66 * mm, "dz" : 0 * mm, "makeCopy" : true});
        }
    });
